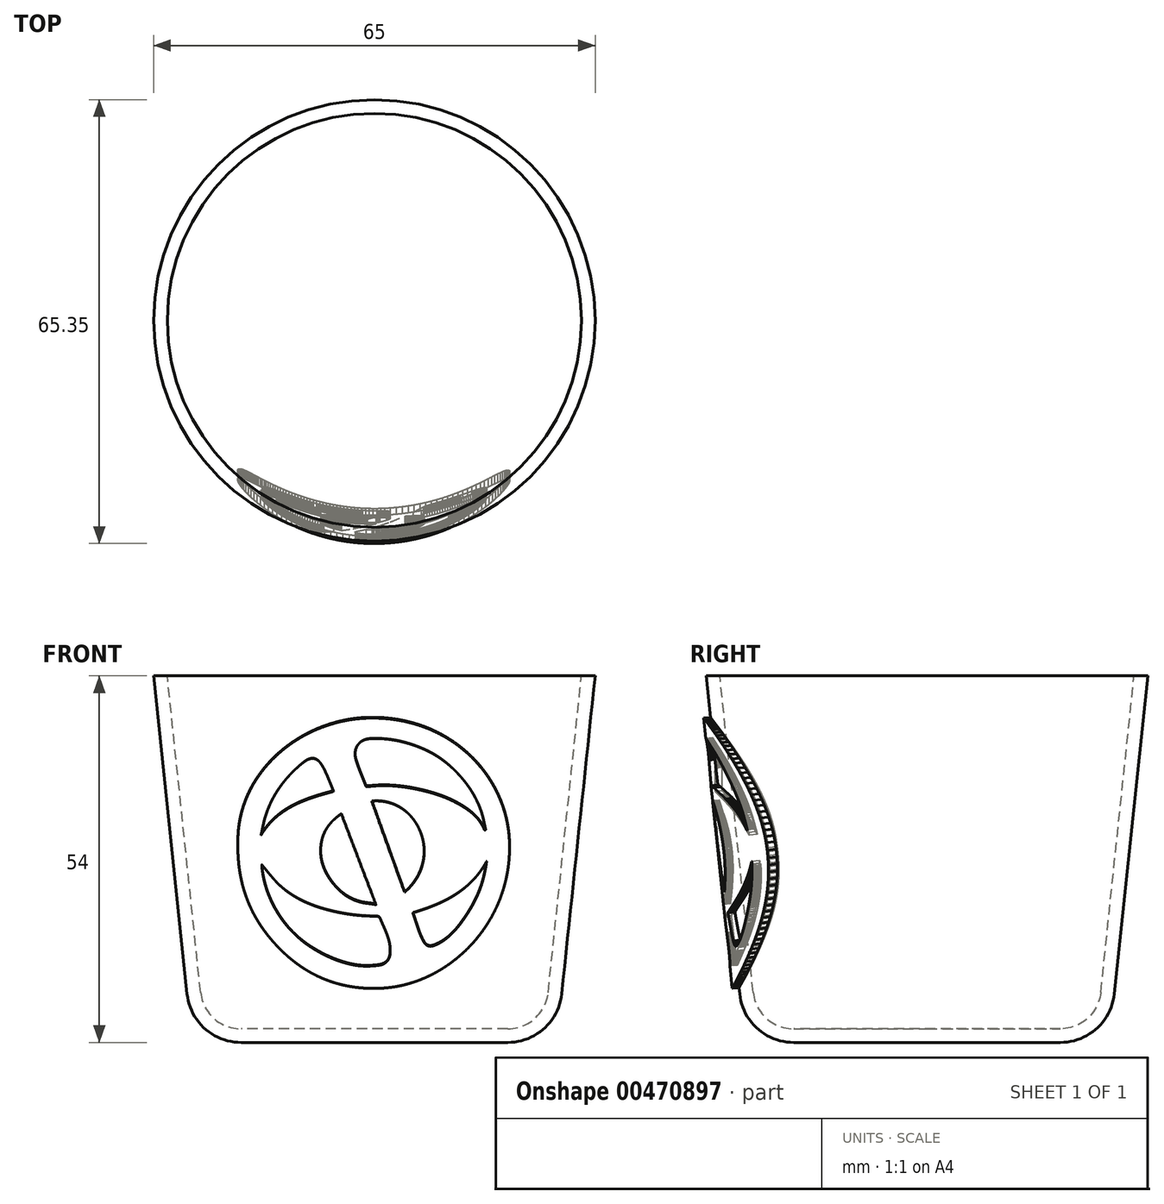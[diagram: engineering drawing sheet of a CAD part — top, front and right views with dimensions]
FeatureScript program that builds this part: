
annotation { "Feature Type Name" : "Feature", "Feature Type Description" : "" }
export const myFeature = defineFeature(function(context is Context, id is Id, definition is map)
    precondition{}
    {
        {
            var Q0;
            Q0=qCreatedBy(makeId("Front.planeOp"),FACE);
            var sketch = newSketch(context, id + "F0", { "sketchPlane" : qUnion([Q0])});
            skLineSegment(sketch, "E0", {"start": v(0, 0) * mm, "end": v(19.62, 0) * mm});
            skArc(sketch, "E1", {"start": v(19.62, 0) * mm, "mid": v(24.97, 2.05) * mm, "end": v(27.58, 7.16) * mm});
            skLineSegment(sketch, "E2", {"start": v(27.58, 7.16) * mm, "end": v(32.5, 54) * mm});
            skLineSegment(sketch, "E3.0", {"start": v(25.59, 7.37) * mm, "end": v(30.49, 54) * mm});
            skArc(sketch, "E3.1", {"start": v(19.62, 2) * mm, "mid": v(23.64, 3.54) * mm, "end": v(25.59, 7.37) * mm});
            skLineSegment(sketch, "E3.2", {"start": v(0, 2) * mm, "end": v(19.62, 2) * mm});
            skLineSegment(sketch, "E4", {"start": v(32.5, 54) * mm, "end": v(30.49, 54) * mm});
            skLineSegment(sketch, "E5", {"start": v(0, 2) * mm, "end": v(0, 0) * mm});
            skSolve(sketch);
        }
        {
            var Q0;
            Q0=makeQuery(id+"F0.imprint","IMPRINT",FACE,{"disambiguationData":[TD([[makeQuery(id+"F0.imprint","IMPRINT",EDGE,{"derivedFrom":sQuery(id+"F0.wireOp",EDGE,"E0")}),1.0]])]});
            var Q1;
            Q1=sQuery(id+"F0.wireOp",EDGE,"E5");
            revolve(context, id + "F1", {"entities" : qUnion([Q0]), "axis" : qUnion([Q1]), "revolveType" : RevolveType.FULL});
        }
        {
            var Q0;
            Q0=makeQuery(id+"F1.opRevolve","SWEPT_FACE",FACE,{"disambiguationData":[OSD([sQuery(id+"F0.wireOp",EDGE,"E4")])]});
            var sketch = newSketch(context, id + "F2", { "sketchPlane" : qUnion([Q0])});
            skCircle(sketch, "E6.0", {"center": v(0, 0) * mm, "radius": 30.49 * mm});
            skSolve(sketch);
        }
        {
            var Q0;
            Q0 = qSketchRegion(id + "F2", true);
            var Q1;
            Q1=makeQuery(id+"F1.opRevolve","SWEPT_FACE",FACE,{"disambiguationData":[OSD([sQuery(id+"F0.wireOp",EDGE,"E3.2")])]});
            extrude(context, id + "F3", {"entities" : qUnion([Q0]), "endBound" : BoundingType.UP_TO_SURFACE, "oppositeDirection" : true, "endBoundEntityFace" : qUnion([Q1]), "depth" : 10.6 * mm});
        }
        {
            var Q0;
            Q0=makeQuery(id+"F1.opRevolve","SWEPT_BODY",BODY,{"disambiguationData":[OSD([sQuery(id+"F0.wireOp",EDGE,"E0"),sQuery(id+"F0.wireOp",EDGE,"E1"),sQuery(id+"F0.wireOp",EDGE,"E2"),sQuery(id+"F0.wireOp",EDGE,"E3.0"),sQuery(id+"F0.wireOp",EDGE,"E3.1"),sQuery(id+"F0.wireOp",EDGE,"E3.2"),sQuery(id+"F0.wireOp",EDGE,"E4"),sQuery(id+"F0.wireOp",EDGE,"E5")])]});
            var Q1;
            Q1=makeQuery(id+"F3.opExtrude","SWEPT_BODY",BODY,{"disambiguationData":[OSD([sQuery(id+"F2.wireOp",EDGE,"E6.0")])]});
            booleanBodies(context, id + "F4", {"operationType" : BooleanOperationType.SUBTRACTION, "tools" : qUnion([Q0]), "targets" : qUnion([Q1]), "keepTools" : true});
        }
        {
            var Q0;
            Q0=makeQuery(id+"F4.opBoolean","SPLIT",BODY,{"disambiguationData":[OD(1.0)],"derivedFrom":makeQuery(id+"F3.opExtrude","SWEPT_BODY",BODY,{"disambiguationData":[OSD([sQuery(id+"F2.wireOp",EDGE,"E6.0")])]})});
            deleteBodies(context, id + "F5", {"entities" : qUnion([Q0])});
        }
        {
            var Q0;
            Q0=makeQuery(id+"F1.opRevolve","SWEPT_FACE",FACE,{"disambiguationData":[OSD([sQuery(id+"F0.wireOp",EDGE,"E4")])]});
            var sketch = newSketch(context, id + "F6", { "sketchPlane" : qUnion([Q0])});
            skPoint(sketch, "E7", {"position": v(0, -32.5) * mm});
            skLineSegment(sketch, "E8", {"start": v(36.98, -32.5) * mm, "end": v(-73.34, -32.5) * mm, "construction": true});
            skSolve(sketch);
        }
        {
            var Q0;
            Q0=qCreatedBy(makeId("Front.planeOp"),FACE);
            var Q1;
            Q1=sQuery(id+"F6.wireOp",VERTEX,"E7");
            cPlane(context, id + "F7", {"entities" : qUnion([Q0, Q1]), "cplaneType" : CPlaneType.PLANE_POINT, "offset" : 25 * mm, "width" : 150 * mm, "height" : 150 * mm});
        }
        {
            var Q0;
            Q0=qCreatedBy(id+"F7.planeOp",FACE);
            var Q1;
            Q1=sQuery(id+"F6.wireOp",EDGE,"E8");
            cPlane(context, id + "F8", {"entities" : qUnion([Q0, Q1]), "cplaneType" : CPlaneType.LINE_ANGLE, "offset" : 25 * mm, "angle" : 6 * degree, "oppositeDirection" : true, "width" : 150 * mm, "height" : 150 * mm});
        }
        {
            var Q0;
            Q0=qCreatedBy(id+"F8.planeOp",FACE);
            var sketch = newSketch(context, id + "F9", { "sketchPlane" : qUnion([Q0])});
            skLineSegment(sketch, "E9", {"start": v(20.1, 31.51) * mm, "end": v(20.1, 32.5) * mm});
            skLineSegment(sketch, "E10", {"start": v(20.1, 32.5) * mm, "end": v(20.03, 33.47) * mm});
            skLineSegment(sketch, "E11", {"start": v(20.03, 33.47) * mm, "end": v(19.91, 34.43) * mm});
            skLineSegment(sketch, "E12", {"start": v(19.91, 34.43) * mm, "end": v(19.75, 35.37) * mm});
            skLineSegment(sketch, "E13", {"start": v(19.75, 35.37) * mm, "end": v(19.53, 36.3) * mm});
            skLineSegment(sketch, "E14", {"start": v(19.53, 36.3) * mm, "end": v(19.27, 37.21) * mm});
            skLineSegment(sketch, "E15", {"start": v(19.27, 37.21) * mm, "end": v(18.96, 38.1) * mm});
            skLineSegment(sketch, "E16", {"start": v(18.96, 38.1) * mm, "end": v(18.6, 38.97) * mm});
            skLineSegment(sketch, "E17", {"start": v(18.6, 38.97) * mm, "end": v(18.21, 39.82) * mm});
            skLineSegment(sketch, "E18", {"start": v(18.21, 39.82) * mm, "end": v(17.78, 40.65) * mm});
            skLineSegment(sketch, "E19", {"start": v(17.78, 40.65) * mm, "end": v(17.3, 41.45) * mm});
            skLineSegment(sketch, "E20", {"start": v(17.3, 41.45) * mm, "end": v(16.79, 42.23) * mm});
            skLineSegment(sketch, "E21", {"start": v(16.79, 42.23) * mm, "end": v(16.23, 42.98) * mm});
            skLineSegment(sketch, "E22", {"start": v(16.23, 42.98) * mm, "end": v(15.65, 43.71) * mm});
            skLineSegment(sketch, "E23", {"start": v(15.65, 43.71) * mm, "end": v(15.03, 44.41) * mm});
            skLineSegment(sketch, "E24", {"start": v(15.03, 44.41) * mm, "end": v(14.38, 45.08) * mm});
            skLineSegment(sketch, "E25", {"start": v(14.38, 45.08) * mm, "end": v(13.7, 45.72) * mm});
            skLineSegment(sketch, "E26", {"start": v(13.7, 45.72) * mm, "end": v(12.99, 46.33) * mm});
            skLineSegment(sketch, "E27", {"start": v(12.99, 46.33) * mm, "end": v(12.25, 46.9) * mm});
            skLineSegment(sketch, "E28", {"start": v(12.25, 46.9) * mm, "end": v(11.49, 47.45) * mm});
            skLineSegment(sketch, "E29", {"start": v(11.49, 47.45) * mm, "end": v(10.7, 47.96) * mm});
            skLineSegment(sketch, "E30", {"start": v(10.7, 47.96) * mm, "end": v(9.9, 48.43) * mm});
            skLineSegment(sketch, "E31", {"start": v(9.9, 48.43) * mm, "end": v(9.07, 48.87) * mm});
            skLineSegment(sketch, "E32", {"start": v(9.07, 48.87) * mm, "end": v(8.22, 49.26) * mm});
            skLineSegment(sketch, "E33", {"start": v(8.22, 49.26) * mm, "end": v(7.35, 49.62) * mm});
            skLineSegment(sketch, "E34", {"start": v(7.35, 49.62) * mm, "end": v(6.47, 49.94) * mm});
            skLineSegment(sketch, "E35", {"start": v(6.47, 49.94) * mm, "end": v(5.58, 50.22) * mm});
            skLineSegment(sketch, "E36", {"start": v(5.58, 50.22) * mm, "end": v(4.67, 50.45) * mm});
            skLineSegment(sketch, "E37", {"start": v(4.67, 50.45) * mm, "end": v(3.75, 50.64) * mm});
            skLineSegment(sketch, "E38", {"start": v(3.75, 50.64) * mm, "end": v(2.82, 50.8) * mm});
            skLineSegment(sketch, "E39", {"start": v(2.82, 50.8) * mm, "end": v(1.88, 50.9) * mm});
            skLineSegment(sketch, "E40", {"start": v(1.88, 50.9) * mm, "end": v(0.94, 50.94) * mm});
            skLineSegment(sketch, "E41", {"start": v(0.94, 50.94) * mm, "end": v(-0.18, 50.95) * mm});
            skLineSegment(sketch, "E42", {"start": v(-0.18, 50.95) * mm, "end": v(-1.27, 50.9) * mm});
            skLineSegment(sketch, "E43", {"start": v(-1.27, 50.9) * mm, "end": v(-2.35, 50.8) * mm});
            skLineSegment(sketch, "E44", {"start": v(-2.35, 50.8) * mm, "end": v(-3.4, 50.64) * mm});
            skLineSegment(sketch, "E45", {"start": v(-3.4, 50.64) * mm, "end": v(-4.42, 50.43) * mm});
            skLineSegment(sketch, "E46", {"start": v(-4.42, 50.43) * mm, "end": v(-5.42, 50.17) * mm});
            skLineSegment(sketch, "E47", {"start": v(-5.42, 50.17) * mm, "end": v(-6.4, 49.86) * mm});
            skLineSegment(sketch, "E48", {"start": v(-6.4, 49.86) * mm, "end": v(-7.34, 49.51) * mm});
            skLineSegment(sketch, "E49", {"start": v(-7.34, 49.51) * mm, "end": v(-8.26, 49.12) * mm});
            skLineSegment(sketch, "E50", {"start": v(-8.26, 49.12) * mm, "end": v(-9.16, 48.68) * mm});
            skLineSegment(sketch, "E51", {"start": v(-9.16, 48.68) * mm, "end": v(-10.02, 48.2) * mm});
            skLineSegment(sketch, "E52", {"start": v(-10.02, 48.2) * mm, "end": v(-10.85, 47.68) * mm});
            skLineSegment(sketch, "E53", {"start": v(-10.85, 47.68) * mm, "end": v(-11.65, 47.12) * mm});
            skLineSegment(sketch, "E54", {"start": v(-11.65, 47.12) * mm, "end": v(-12.42, 46.53) * mm});
            skLineSegment(sketch, "E55", {"start": v(-12.42, 46.53) * mm, "end": v(-13.16, 45.9) * mm});
            skLineSegment(sketch, "E56", {"start": v(-13.16, 45.9) * mm, "end": v(-13.86, 45.24) * mm});
            skLineSegment(sketch, "E57", {"start": v(-13.86, 45.24) * mm, "end": v(-14.53, 44.56) * mm});
            skLineSegment(sketch, "E58", {"start": v(-14.53, 44.56) * mm, "end": v(-15.17, 43.84) * mm});
            skLineSegment(sketch, "E59", {"start": v(-15.17, 43.84) * mm, "end": v(-15.77, 43.1) * mm});
            skLineSegment(sketch, "E60", {"start": v(-15.77, 43.1) * mm, "end": v(-16.33, 42.32) * mm});
            skLineSegment(sketch, "E61", {"start": v(-16.33, 42.32) * mm, "end": v(-16.85, 41.53) * mm});
            skLineSegment(sketch, "E62", {"start": v(-16.85, 41.53) * mm, "end": v(-17.34, 40.72) * mm});
            skLineSegment(sketch, "E63", {"start": v(-17.34, 40.72) * mm, "end": v(-17.78, 39.88) * mm});
            skLineSegment(sketch, "E64", {"start": v(-17.78, 39.88) * mm, "end": v(-18.19, 39.03) * mm});
            skLineSegment(sketch, "E65", {"start": v(-18.19, 39.03) * mm, "end": v(-18.55, 38.16) * mm});
            skLineSegment(sketch, "E66", {"start": v(-18.55, 38.16) * mm, "end": v(-18.88, 37.27) * mm});
            skLineSegment(sketch, "E67", {"start": v(-18.88, 37.27) * mm, "end": v(-19.16, 36.37) * mm});
            skLineSegment(sketch, "E68", {"start": v(-19.16, 36.37) * mm, "end": v(-19.4, 35.47) * mm});
            skLineSegment(sketch, "E69", {"start": v(-19.4, 35.47) * mm, "end": v(-19.59, 34.55) * mm});
            skLineSegment(sketch, "E70", {"start": v(-19.59, 34.55) * mm, "end": v(-19.73, 33.62) * mm});
            skLineSegment(sketch, "E71", {"start": v(-19.73, 33.62) * mm, "end": v(-19.84, 32.69) * mm});
            skLineSegment(sketch, "E72", {"start": v(-19.84, 32.69) * mm, "end": v(-19.89, 31.75) * mm});
            skLineSegment(sketch, "E73", {"start": v(-19.89, 31.75) * mm, "end": v(-19.9, 30.63) * mm});
            skLineSegment(sketch, "E74", {"start": v(-19.9, 30.63) * mm, "end": v(-19.85, 29.53) * mm});
            skLineSegment(sketch, "E75", {"start": v(-19.85, 29.53) * mm, "end": v(-19.75, 28.46) * mm});
            skLineSegment(sketch, "E76", {"start": v(-19.75, 28.46) * mm, "end": v(-19.6, 27.4) * mm});
            skLineSegment(sketch, "E77", {"start": v(-19.6, 27.4) * mm, "end": v(-19.39, 26.39) * mm});
            skLineSegment(sketch, "E78", {"start": v(-19.39, 26.39) * mm, "end": v(-19.13, 25.4) * mm});
            skLineSegment(sketch, "E79", {"start": v(-19.13, 25.4) * mm, "end": v(-18.83, 24.42) * mm});
            skLineSegment(sketch, "E80", {"start": v(-18.83, 24.42) * mm, "end": v(-18.49, 23.49) * mm});
            skLineSegment(sketch, "E81", {"start": v(-18.49, 23.49) * mm, "end": v(-18.1, 22.57) * mm});
            skLineSegment(sketch, "E82", {"start": v(-18.1, 22.57) * mm, "end": v(-17.67, 21.7) * mm});
            skLineSegment(sketch, "E83", {"start": v(-17.67, 21.7) * mm, "end": v(-17.2, 20.84) * mm});
            skLineSegment(sketch, "E84", {"start": v(-17.2, 20.84) * mm, "end": v(-16.7, 20.02) * mm});
            skLineSegment(sketch, "E85", {"start": v(-16.7, 20.02) * mm, "end": v(-16.15, 19.23) * mm});
            skLineSegment(sketch, "E86", {"start": v(-16.15, 19.23) * mm, "end": v(-15.58, 18.47) * mm});
            skLineSegment(sketch, "E87", {"start": v(-15.58, 18.47) * mm, "end": v(-14.97, 17.74) * mm});
            skLineSegment(sketch, "E88", {"start": v(-14.97, 17.74) * mm, "end": v(-14.33, 17.05) * mm});
            skLineSegment(sketch, "E89", {"start": v(-14.33, 17.05) * mm, "end": v(-13.66, 16.4) * mm});
            skLineSegment(sketch, "E90", {"start": v(-13.66, 16.4) * mm, "end": v(-12.97, 15.77) * mm});
            skLineSegment(sketch, "E91", {"start": v(-12.97, 15.77) * mm, "end": v(-12.25, 15.18) * mm});
            skLineSegment(sketch, "E92", {"start": v(-12.25, 15.18) * mm, "end": v(-11.5, 14.62) * mm});
            skLineSegment(sketch, "E93", {"start": v(-11.5, 14.62) * mm, "end": v(-10.74, 14.1) * mm});
            skLineSegment(sketch, "E94", {"start": v(-10.74, 14.1) * mm, "end": v(-9.96, 13.62) * mm});
            skLineSegment(sketch, "E95", {"start": v(-9.96, 13.62) * mm, "end": v(-9.16, 13.18) * mm});
            skLineSegment(sketch, "E96", {"start": v(-9.16, 13.18) * mm, "end": v(-8.34, 12.77) * mm});
            skLineSegment(sketch, "E97", {"start": v(-8.34, 12.77) * mm, "end": v(-7.51, 12.4) * mm});
            skLineSegment(sketch, "E98", {"start": v(-7.51, 12.4) * mm, "end": v(-6.67, 12.07) * mm});
            skLineSegment(sketch, "E99", {"start": v(-6.67, 12.07) * mm, "end": v(-5.82, 11.78) * mm});
            skLineSegment(sketch, "E100", {"start": v(-5.82, 11.78) * mm, "end": v(-4.96, 11.53) * mm});
            skLineSegment(sketch, "E101", {"start": v(-4.96, 11.53) * mm, "end": v(-4.09, 11.33) * mm});
            skLineSegment(sketch, "E102", {"start": v(-4.09, 11.33) * mm, "end": v(-3.22, 11.16) * mm});
            skLineSegment(sketch, "E103", {"start": v(-3.22, 11.16) * mm, "end": v(-2.34, 11.04) * mm});
            skLineSegment(sketch, "E104", {"start": v(-2.34, 11.04) * mm, "end": v(-1.46, 10.96) * mm});
            skLineSegment(sketch, "E105", {"start": v(-1.46, 10.96) * mm, "end": v(-0.9, 10.93) * mm});
            skLineSegment(sketch, "E106", {"start": v(-0.9, 10.93) * mm, "end": v(-0.33, 10.91) * mm});
            skLineSegment(sketch, "E107", {"start": v(-0.33, 10.91) * mm, "end": v(0.23, 10.9) * mm});
            skLineSegment(sketch, "E108", {"start": v(0.23, 10.9) * mm, "end": v(0.79, 10.92) * mm});
            skLineSegment(sketch, "E109", {"start": v(0.79, 10.92) * mm, "end": v(1.34, 10.94) * mm});
            skLineSegment(sketch, "E110", {"start": v(1.34, 10.94) * mm, "end": v(1.89, 10.97) * mm});
            skLineSegment(sketch, "E111", {"start": v(1.89, 10.97) * mm, "end": v(2.43, 11.02) * mm});
            skLineSegment(sketch, "E112", {"start": v(2.43, 11.02) * mm, "end": v(2.97, 11.09) * mm});
            skLineSegment(sketch, "E113", {"start": v(2.97, 11.09) * mm, "end": v(3.5, 11.16) * mm});
            skLineSegment(sketch, "E114", {"start": v(3.5, 11.16) * mm, "end": v(4.03, 11.25) * mm});
            skLineSegment(sketch, "E115", {"start": v(4.03, 11.25) * mm, "end": v(4.55, 11.36) * mm});
            skLineSegment(sketch, "E116", {"start": v(4.55, 11.36) * mm, "end": v(5.07, 11.47) * mm});
            skLineSegment(sketch, "E117", {"start": v(5.07, 11.47) * mm, "end": v(5.58, 11.6) * mm});
            skLineSegment(sketch, "E118", {"start": v(5.58, 11.6) * mm, "end": v(6.09, 11.75) * mm});
            skLineSegment(sketch, "E119", {"start": v(6.09, 11.75) * mm, "end": v(6.59, 11.9) * mm});
            skLineSegment(sketch, "E120", {"start": v(6.59, 11.9) * mm, "end": v(7.08, 12.08) * mm});
            skLineSegment(sketch, "E121", {"start": v(7.08, 12.08) * mm, "end": v(7.58, 12.27) * mm});
            skLineSegment(sketch, "E122", {"start": v(7.58, 12.27) * mm, "end": v(8.06, 12.47) * mm});
            skLineSegment(sketch, "E123", {"start": v(8.06, 12.47) * mm, "end": v(8.54, 12.68) * mm});
            skLineSegment(sketch, "E124", {"start": v(8.54, 12.68) * mm, "end": v(9.02, 12.9) * mm});
            skLineSegment(sketch, "E125", {"start": v(9.02, 12.9) * mm, "end": v(9.49, 13.15) * mm});
            skLineSegment(sketch, "E126", {"start": v(9.49, 13.15) * mm, "end": v(9.95, 13.4) * mm});
            skLineSegment(sketch, "E127", {"start": v(9.95, 13.4) * mm, "end": v(10.41, 13.68) * mm});
            skLineSegment(sketch, "E128", {"start": v(10.41, 13.68) * mm, "end": v(10.87, 13.96) * mm});
            skLineSegment(sketch, "E129", {"start": v(10.87, 13.96) * mm, "end": v(11.31, 14.26) * mm});
            skLineSegment(sketch, "E130", {"start": v(11.31, 14.26) * mm, "end": v(11.76, 14.57) * mm});
            skLineSegment(sketch, "E131", {"start": v(11.76, 14.57) * mm, "end": v(12.2, 14.9) * mm});
            skLineSegment(sketch, "E132", {"start": v(12.2, 14.9) * mm, "end": v(12.62, 15.24) * mm});
            skLineSegment(sketch, "E133", {"start": v(12.62, 15.24) * mm, "end": v(13.05, 15.6) * mm});
            skLineSegment(sketch, "E134", {"start": v(13.05, 15.6) * mm, "end": v(13.47, 15.96) * mm});
            skLineSegment(sketch, "E135", {"start": v(13.47, 15.96) * mm, "end": v(13.88, 16.34) * mm});
            skLineSegment(sketch, "E136", {"start": v(13.88, 16.34) * mm, "end": v(14.29, 16.74) * mm});
            skLineSegment(sketch, "E137", {"start": v(14.29, 16.74) * mm, "end": v(14.64, 17.1) * mm});
            skLineSegment(sketch, "E138", {"start": v(14.64, 17.1) * mm, "end": v(14.99, 17.47) * mm});
            skLineSegment(sketch, "E139", {"start": v(14.99, 17.47) * mm, "end": v(15.32, 17.85) * mm});
            skLineSegment(sketch, "E140", {"start": v(15.32, 17.85) * mm, "end": v(15.65, 18.23) * mm});
            skLineSegment(sketch, "E141", {"start": v(15.65, 18.23) * mm, "end": v(15.96, 18.61) * mm});
            skLineSegment(sketch, "E142", {"start": v(15.96, 18.61) * mm, "end": v(16.26, 19) * mm});
            skLineSegment(sketch, "E143", {"start": v(16.26, 19) * mm, "end": v(16.55, 19.4) * mm});
            skLineSegment(sketch, "E144", {"start": v(16.55, 19.4) * mm, "end": v(16.83, 19.8) * mm});
            skLineSegment(sketch, "E145", {"start": v(16.83, 19.8) * mm, "end": v(17.1, 20.22) * mm});
            skLineSegment(sketch, "E146", {"start": v(17.1, 20.22) * mm, "end": v(17.36, 20.63) * mm});
            skLineSegment(sketch, "E147", {"start": v(17.36, 20.63) * mm, "end": v(17.6, 21.05) * mm});
            skLineSegment(sketch, "E148", {"start": v(17.6, 21.05) * mm, "end": v(17.84, 21.48) * mm});
            skLineSegment(sketch, "E149", {"start": v(17.84, 21.48) * mm, "end": v(18.07, 21.91) * mm});
            skLineSegment(sketch, "E150", {"start": v(18.07, 21.91) * mm, "end": v(18.28, 22.35) * mm});
            skLineSegment(sketch, "E151", {"start": v(18.28, 22.35) * mm, "end": v(18.48, 22.8) * mm});
            skLineSegment(sketch, "E152", {"start": v(18.48, 22.8) * mm, "end": v(18.67, 23.26) * mm});
            skLineSegment(sketch, "E153", {"start": v(18.67, 23.26) * mm, "end": v(18.85, 23.72) * mm});
            skLineSegment(sketch, "E154", {"start": v(18.85, 23.72) * mm, "end": v(19.02, 24.18) * mm});
            skLineSegment(sketch, "E155", {"start": v(19.02, 24.18) * mm, "end": v(19.17, 24.66) * mm});
            skLineSegment(sketch, "E156", {"start": v(19.17, 24.66) * mm, "end": v(19.32, 25.14) * mm});
            skLineSegment(sketch, "E157", {"start": v(19.32, 25.14) * mm, "end": v(19.45, 25.63) * mm});
            skLineSegment(sketch, "E158", {"start": v(19.45, 25.63) * mm, "end": v(19.57, 26.12) * mm});
            skLineSegment(sketch, "E159", {"start": v(19.57, 26.12) * mm, "end": v(19.68, 26.63) * mm});
            skLineSegment(sketch, "E160", {"start": v(19.68, 26.63) * mm, "end": v(19.77, 27.14) * mm});
            skLineSegment(sketch, "E161", {"start": v(19.77, 27.14) * mm, "end": v(19.86, 27.66) * mm});
            skLineSegment(sketch, "E162", {"start": v(19.86, 27.66) * mm, "end": v(19.93, 28.18) * mm});
            skLineSegment(sketch, "E163", {"start": v(19.93, 28.18) * mm, "end": v(19.99, 28.72) * mm});
            skLineSegment(sketch, "E164", {"start": v(19.99, 28.72) * mm, "end": v(20.04, 29.26) * mm});
            skLineSegment(sketch, "E165", {"start": v(20.04, 29.26) * mm, "end": v(20.07, 29.81) * mm});
            skLineSegment(sketch, "E166", {"start": v(20.07, 29.81) * mm, "end": v(20.1, 30.37) * mm});
            skLineSegment(sketch, "E167", {"start": v(20.1, 30.37) * mm, "end": v(20.1, 30.94) * mm});
            skLineSegment(sketch, "E168", {"start": v(20.1, 30.94) * mm, "end": v(20.1, 31.51) * mm});
            skLineSegment(sketch, "E169", {"start": v(18.1, 31.51) * mm, "end": v(18.1, 30.94) * mm});
            skLineSegment(sketch, "E170", {"start": v(20.1, 30.94) * mm, "end": v(20.1, 30.37) * mm});
            skLineSegment(sketch, "E171", {"start": v(20.1, 30.37) * mm, "end": v(20.07, 29.81) * mm});
            skLineSegment(sketch, "E172", {"start": v(20.07, 29.81) * mm, "end": v(20.04, 29.26) * mm});
            skLineSegment(sketch, "E173", {"start": v(20.04, 29.26) * mm, "end": v(19.99, 28.72) * mm});
            skLineSegment(sketch, "E174", {"start": v(19.99, 28.72) * mm, "end": v(19.93, 28.18) * mm});
            skLineSegment(sketch, "E175", {"start": v(19.93, 28.18) * mm, "end": v(19.86, 27.66) * mm});
            skLineSegment(sketch, "E176", {"start": v(19.86, 27.66) * mm, "end": v(19.77, 27.14) * mm});
            skLineSegment(sketch, "E177", {"start": v(19.77, 27.14) * mm, "end": v(19.68, 26.63) * mm});
            skLineSegment(sketch, "E178", {"start": v(19.68, 26.63) * mm, "end": v(19.57, 26.12) * mm});
            skLineSegment(sketch, "E179", {"start": v(19.57, 26.12) * mm, "end": v(19.45, 25.63) * mm});
            skLineSegment(sketch, "E180", {"start": v(19.45, 25.63) * mm, "end": v(19.32, 25.14) * mm});
            skLineSegment(sketch, "E181", {"start": v(19.32, 25.14) * mm, "end": v(19.17, 24.66) * mm});
            skLineSegment(sketch, "E182", {"start": v(19.17, 24.66) * mm, "end": v(19.02, 24.18) * mm});
            skLineSegment(sketch, "E183", {"start": v(19.02, 24.18) * mm, "end": v(18.85, 23.72) * mm});
            skLineSegment(sketch, "E184", {"start": v(18.85, 23.72) * mm, "end": v(18.67, 23.26) * mm});
            skLineSegment(sketch, "E185", {"start": v(18.67, 23.26) * mm, "end": v(18.48, 22.8) * mm});
            skLineSegment(sketch, "E186", {"start": v(18.48, 22.8) * mm, "end": v(18.28, 22.35) * mm});
            skLineSegment(sketch, "E187", {"start": v(18.28, 22.35) * mm, "end": v(18.07, 21.91) * mm});
            skLineSegment(sketch, "E188", {"start": v(18.07, 21.91) * mm, "end": v(17.84, 21.48) * mm});
            skLineSegment(sketch, "E189", {"start": v(17.84, 21.48) * mm, "end": v(17.6, 21.05) * mm});
            skLineSegment(sketch, "E190", {"start": v(17.6, 21.05) * mm, "end": v(17.36, 20.63) * mm});
            skLineSegment(sketch, "E191", {"start": v(17.36, 20.63) * mm, "end": v(17.1, 20.22) * mm});
            skLineSegment(sketch, "E192", {"start": v(17.1, 20.22) * mm, "end": v(16.83, 19.8) * mm});
            skLineSegment(sketch, "E193", {"start": v(16.83, 19.8) * mm, "end": v(16.55, 19.4) * mm});
            skLineSegment(sketch, "E194", {"start": v(16.55, 19.4) * mm, "end": v(16.26, 19) * mm});
            skLineSegment(sketch, "E195", {"start": v(16.26, 19) * mm, "end": v(15.96, 18.61) * mm});
            skLineSegment(sketch, "E196", {"start": v(15.96, 18.61) * mm, "end": v(15.65, 18.23) * mm});
            skLineSegment(sketch, "E197", {"start": v(15.65, 18.23) * mm, "end": v(15.32, 17.85) * mm});
            skLineSegment(sketch, "E198", {"start": v(15.32, 17.85) * mm, "end": v(14.99, 17.47) * mm});
            skLineSegment(sketch, "E199", {"start": v(14.99, 17.47) * mm, "end": v(14.64, 17.1) * mm});
            skLineSegment(sketch, "E200", {"start": v(14.64, 17.1) * mm, "end": v(14.29, 16.74) * mm});
            skLineSegment(sketch, "E201", {"start": v(14.29, 16.74) * mm, "end": v(13.88, 16.34) * mm});
            skLineSegment(sketch, "E202", {"start": v(13.88, 16.34) * mm, "end": v(13.47, 15.96) * mm});
            skLineSegment(sketch, "E203", {"start": v(13.47, 15.96) * mm, "end": v(13.05, 15.6) * mm});
            skLineSegment(sketch, "E204", {"start": v(13.05, 15.6) * mm, "end": v(12.62, 15.24) * mm});
            skLineSegment(sketch, "E205", {"start": v(12.62, 15.24) * mm, "end": v(12.2, 14.9) * mm});
            skLineSegment(sketch, "E206", {"start": v(12.2, 14.9) * mm, "end": v(11.76, 14.57) * mm});
            skLineSegment(sketch, "E207", {"start": v(11.76, 14.57) * mm, "end": v(11.31, 14.26) * mm});
            skLineSegment(sketch, "E208", {"start": v(11.31, 14.26) * mm, "end": v(10.87, 13.96) * mm});
            skLineSegment(sketch, "E209", {"start": v(10.87, 13.96) * mm, "end": v(10.41, 13.68) * mm});
            skLineSegment(sketch, "E210", {"start": v(10.41, 13.68) * mm, "end": v(9.95, 13.4) * mm});
            skLineSegment(sketch, "E211", {"start": v(9.95, 13.4) * mm, "end": v(9.49, 13.15) * mm});
            skLineSegment(sketch, "E212", {"start": v(9.49, 13.15) * mm, "end": v(9.02, 12.9) * mm});
            skLineSegment(sketch, "E213", {"start": v(9.02, 12.9) * mm, "end": v(8.54, 12.68) * mm});
            skLineSegment(sketch, "E214", {"start": v(8.54, 12.68) * mm, "end": v(8.06, 12.47) * mm});
            skLineSegment(sketch, "E215", {"start": v(8.06, 12.47) * mm, "end": v(7.58, 12.27) * mm});
            skLineSegment(sketch, "E216", {"start": v(7.58, 12.27) * mm, "end": v(7.08, 12.08) * mm});
            skLineSegment(sketch, "E217", {"start": v(7.08, 12.08) * mm, "end": v(6.59, 11.9) * mm});
            skLineSegment(sketch, "E218", {"start": v(6.59, 11.9) * mm, "end": v(6.09, 11.75) * mm});
            skLineSegment(sketch, "E219", {"start": v(6.09, 11.75) * mm, "end": v(5.58, 11.6) * mm});
            skLineSegment(sketch, "E220", {"start": v(5.58, 11.6) * mm, "end": v(5.07, 11.47) * mm});
            skLineSegment(sketch, "E221", {"start": v(5.07, 11.47) * mm, "end": v(4.55, 11.36) * mm});
            skLineSegment(sketch, "E222", {"start": v(4.55, 11.36) * mm, "end": v(4.03, 11.25) * mm});
            skLineSegment(sketch, "E223", {"start": v(4.03, 11.25) * mm, "end": v(3.5, 11.16) * mm});
            skLineSegment(sketch, "E224", {"start": v(3.5, 11.16) * mm, "end": v(2.97, 11.09) * mm});
            skLineSegment(sketch, "E225", {"start": v(2.97, 11.09) * mm, "end": v(2.43, 11.02) * mm});
            skLineSegment(sketch, "E226", {"start": v(2.43, 11.02) * mm, "end": v(1.89, 10.97) * mm});
            skLineSegment(sketch, "E227", {"start": v(1.89, 10.97) * mm, "end": v(1.34, 10.94) * mm});
            skLineSegment(sketch, "E228", {"start": v(1.34, 10.94) * mm, "end": v(0.79, 10.92) * mm});
            skLineSegment(sketch, "E229", {"start": v(0.79, 10.92) * mm, "end": v(0.23, 10.9) * mm});
            skLineSegment(sketch, "E230", {"start": v(0.23, 10.9) * mm, "end": v(-0.33, 10.91) * mm});
            skLineSegment(sketch, "E231", {"start": v(-0.33, 10.91) * mm, "end": v(-0.9, 10.93) * mm});
            skLineSegment(sketch, "E232", {"start": v(-0.9, 10.93) * mm, "end": v(-1.46, 10.96) * mm});
            skLineSegment(sketch, "E233", {"start": v(-1.46, 10.96) * mm, "end": v(-2.34, 11.04) * mm});
            skLineSegment(sketch, "E234", {"start": v(-2.34, 11.04) * mm, "end": v(-3.22, 11.16) * mm});
            skLineSegment(sketch, "E235", {"start": v(-3.22, 11.16) * mm, "end": v(-4.09, 11.33) * mm});
            skLineSegment(sketch, "E236", {"start": v(-4.09, 11.33) * mm, "end": v(-4.96, 11.53) * mm});
            skLineSegment(sketch, "E237", {"start": v(-4.96, 11.53) * mm, "end": v(-5.82, 11.78) * mm});
            skLineSegment(sketch, "E238", {"start": v(-5.82, 11.78) * mm, "end": v(-6.67, 12.07) * mm});
            skLineSegment(sketch, "E239", {"start": v(-6.67, 12.07) * mm, "end": v(-7.51, 12.4) * mm});
            skLineSegment(sketch, "E240", {"start": v(-7.51, 12.4) * mm, "end": v(-8.34, 12.77) * mm});
            skLineSegment(sketch, "E241", {"start": v(-8.34, 12.77) * mm, "end": v(-9.16, 13.18) * mm});
            skLineSegment(sketch, "E242", {"start": v(-9.16, 13.18) * mm, "end": v(-9.96, 13.62) * mm});
            skLineSegment(sketch, "E243", {"start": v(-9.96, 13.62) * mm, "end": v(-10.74, 14.1) * mm});
            skLineSegment(sketch, "E244", {"start": v(-10.74, 14.1) * mm, "end": v(-11.5, 14.62) * mm});
            skLineSegment(sketch, "E245", {"start": v(-11.5, 14.62) * mm, "end": v(-12.25, 15.18) * mm});
            skLineSegment(sketch, "E246", {"start": v(-12.25, 15.18) * mm, "end": v(-12.97, 15.77) * mm});
            skLineSegment(sketch, "E247", {"start": v(-12.97, 15.77) * mm, "end": v(-13.66, 16.4) * mm});
            skLineSegment(sketch, "E248", {"start": v(-13.66, 16.4) * mm, "end": v(-14.33, 17.05) * mm});
            skLineSegment(sketch, "E249", {"start": v(-14.33, 17.05) * mm, "end": v(-14.97, 17.74) * mm});
            skLineSegment(sketch, "E250", {"start": v(-14.97, 17.74) * mm, "end": v(-15.58, 18.47) * mm});
            skLineSegment(sketch, "E251", {"start": v(-15.58, 18.47) * mm, "end": v(-16.15, 19.23) * mm});
            skLineSegment(sketch, "E252", {"start": v(-16.15, 19.23) * mm, "end": v(-16.7, 20.02) * mm});
            skLineSegment(sketch, "E253", {"start": v(-16.7, 20.02) * mm, "end": v(-17.2, 20.84) * mm});
            skLineSegment(sketch, "E254", {"start": v(-17.2, 20.84) * mm, "end": v(-17.67, 21.7) * mm});
            skLineSegment(sketch, "E255", {"start": v(-17.67, 21.7) * mm, "end": v(-18.1, 22.57) * mm});
            skLineSegment(sketch, "E256", {"start": v(-18.1, 22.57) * mm, "end": v(-18.49, 23.49) * mm});
            skLineSegment(sketch, "E257", {"start": v(-18.49, 23.49) * mm, "end": v(-18.83, 24.42) * mm});
            skLineSegment(sketch, "E258", {"start": v(-18.83, 24.42) * mm, "end": v(-19.13, 25.4) * mm});
            skLineSegment(sketch, "E259", {"start": v(-19.13, 25.4) * mm, "end": v(-19.39, 26.39) * mm});
            skLineSegment(sketch, "E260", {"start": v(-19.39, 26.39) * mm, "end": v(-19.6, 27.4) * mm});
            skLineSegment(sketch, "E261", {"start": v(-19.6, 27.4) * mm, "end": v(-19.75, 28.46) * mm});
            skLineSegment(sketch, "E262", {"start": v(-19.75, 28.46) * mm, "end": v(-19.85, 29.53) * mm});
            skLineSegment(sketch, "E263", {"start": v(-19.85, 29.53) * mm, "end": v(-19.9, 30.63) * mm});
            skLineSegment(sketch, "E264", {"start": v(-19.9, 30.63) * mm, "end": v(-19.89, 31.75) * mm});
            skLineSegment(sketch, "E265", {"start": v(-19.89, 31.75) * mm, "end": v(-19.84, 32.69) * mm});
            skLineSegment(sketch, "E266", {"start": v(-19.84, 32.69) * mm, "end": v(-19.73, 33.62) * mm});
            skLineSegment(sketch, "E267", {"start": v(-19.73, 33.62) * mm, "end": v(-19.59, 34.55) * mm});
            skLineSegment(sketch, "E268", {"start": v(-19.59, 34.55) * mm, "end": v(-19.4, 35.47) * mm});
            skLineSegment(sketch, "E269", {"start": v(-19.4, 35.47) * mm, "end": v(-19.16, 36.37) * mm});
            skLineSegment(sketch, "E270", {"start": v(-19.16, 36.37) * mm, "end": v(-18.88, 37.27) * mm});
            skLineSegment(sketch, "E271", {"start": v(-18.88, 37.27) * mm, "end": v(-18.55, 38.16) * mm});
            skLineSegment(sketch, "E272", {"start": v(-18.55, 38.16) * mm, "end": v(-18.19, 39.03) * mm});
            skLineSegment(sketch, "E273", {"start": v(-18.19, 39.03) * mm, "end": v(-17.78, 39.88) * mm});
            skLineSegment(sketch, "E274", {"start": v(-17.78, 39.88) * mm, "end": v(-17.34, 40.72) * mm});
            skLineSegment(sketch, "E275", {"start": v(-17.34, 40.72) * mm, "end": v(-16.85, 41.53) * mm});
            skLineSegment(sketch, "E276", {"start": v(-16.85, 41.53) * mm, "end": v(-16.33, 42.32) * mm});
            skLineSegment(sketch, "E277", {"start": v(-16.33, 42.32) * mm, "end": v(-15.77, 43.1) * mm});
            skLineSegment(sketch, "E278", {"start": v(-15.77, 43.1) * mm, "end": v(-15.17, 43.84) * mm});
            skLineSegment(sketch, "E279", {"start": v(-15.17, 43.84) * mm, "end": v(-14.53, 44.56) * mm});
            skLineSegment(sketch, "E280", {"start": v(-14.53, 44.56) * mm, "end": v(-13.86, 45.24) * mm});
            skLineSegment(sketch, "E281", {"start": v(-13.86, 45.24) * mm, "end": v(-13.16, 45.9) * mm});
            skLineSegment(sketch, "E282", {"start": v(-13.16, 45.9) * mm, "end": v(-12.42, 46.53) * mm});
            skLineSegment(sketch, "E283", {"start": v(-12.42, 46.53) * mm, "end": v(-11.65, 47.12) * mm});
            skLineSegment(sketch, "E284", {"start": v(-11.65, 47.12) * mm, "end": v(-10.85, 47.68) * mm});
            skLineSegment(sketch, "E285", {"start": v(-10.85, 47.68) * mm, "end": v(-10.02, 48.2) * mm});
            skLineSegment(sketch, "E286", {"start": v(-10.02, 48.2) * mm, "end": v(-9.16, 48.68) * mm});
            skLineSegment(sketch, "E287", {"start": v(-9.16, 48.68) * mm, "end": v(-8.26, 49.12) * mm});
            skLineSegment(sketch, "E288", {"start": v(-8.26, 49.12) * mm, "end": v(-7.34, 49.51) * mm});
            skLineSegment(sketch, "E289", {"start": v(-7.34, 49.51) * mm, "end": v(-6.4, 49.86) * mm});
            skLineSegment(sketch, "E290", {"start": v(-6.4, 49.86) * mm, "end": v(-5.42, 50.17) * mm});
            skLineSegment(sketch, "E291", {"start": v(-5.42, 50.17) * mm, "end": v(-4.42, 50.43) * mm});
            skLineSegment(sketch, "E292", {"start": v(-4.42, 50.43) * mm, "end": v(-3.4, 50.64) * mm});
            skLineSegment(sketch, "E293", {"start": v(-3.4, 50.64) * mm, "end": v(-2.35, 50.8) * mm});
            skLineSegment(sketch, "E294", {"start": v(-2.35, 50.8) * mm, "end": v(-1.27, 50.9) * mm});
            skLineSegment(sketch, "E295", {"start": v(-1.27, 50.9) * mm, "end": v(-0.18, 50.95) * mm});
            skLineSegment(sketch, "E296", {"start": v(-0.18, 50.95) * mm, "end": v(0.94, 50.94) * mm});
            skLineSegment(sketch, "E297", {"start": v(0.94, 50.94) * mm, "end": v(1.88, 50.9) * mm});
            skLineSegment(sketch, "E298", {"start": v(1.88, 50.9) * mm, "end": v(2.82, 50.8) * mm});
            skLineSegment(sketch, "E299", {"start": v(2.82, 50.8) * mm, "end": v(3.75, 50.64) * mm});
            skLineSegment(sketch, "E300", {"start": v(3.75, 50.64) * mm, "end": v(4.67, 50.45) * mm});
            skLineSegment(sketch, "E301", {"start": v(4.67, 50.45) * mm, "end": v(5.58, 50.22) * mm});
            skLineSegment(sketch, "E302", {"start": v(5.58, 50.22) * mm, "end": v(6.47, 49.94) * mm});
            skLineSegment(sketch, "E303", {"start": v(6.47, 49.94) * mm, "end": v(7.35, 49.62) * mm});
            skLineSegment(sketch, "E304", {"start": v(7.35, 49.62) * mm, "end": v(8.22, 49.26) * mm});
            skLineSegment(sketch, "E305", {"start": v(8.22, 49.26) * mm, "end": v(9.07, 48.87) * mm});
            skLineSegment(sketch, "E306", {"start": v(9.07, 48.87) * mm, "end": v(9.9, 48.43) * mm});
            skLineSegment(sketch, "E307", {"start": v(9.9, 48.43) * mm, "end": v(10.7, 47.96) * mm});
            skLineSegment(sketch, "E308", {"start": v(10.7, 47.96) * mm, "end": v(11.49, 47.45) * mm});
            skLineSegment(sketch, "E309", {"start": v(11.49, 47.45) * mm, "end": v(12.25, 46.9) * mm});
            skLineSegment(sketch, "E310", {"start": v(12.25, 46.9) * mm, "end": v(12.99, 46.33) * mm});
            skLineSegment(sketch, "E311", {"start": v(12.99, 46.33) * mm, "end": v(13.7, 45.72) * mm});
            skLineSegment(sketch, "E312", {"start": v(13.7, 45.72) * mm, "end": v(14.38, 45.08) * mm});
            skLineSegment(sketch, "E313", {"start": v(14.38, 45.08) * mm, "end": v(15.03, 44.41) * mm});
            skLineSegment(sketch, "E314", {"start": v(15.03, 44.41) * mm, "end": v(15.65, 43.71) * mm});
            skLineSegment(sketch, "E315", {"start": v(15.65, 43.71) * mm, "end": v(16.23, 42.98) * mm});
            skLineSegment(sketch, "E316", {"start": v(16.23, 42.98) * mm, "end": v(16.79, 42.23) * mm});
            skLineSegment(sketch, "E317", {"start": v(16.79, 42.23) * mm, "end": v(17.3, 41.45) * mm});
            skLineSegment(sketch, "E318", {"start": v(17.3, 41.45) * mm, "end": v(17.78, 40.65) * mm});
            skLineSegment(sketch, "E319", {"start": v(17.78, 40.65) * mm, "end": v(18.21, 39.82) * mm});
            skLineSegment(sketch, "E320", {"start": v(18.21, 39.82) * mm, "end": v(18.6, 38.97) * mm});
            skLineSegment(sketch, "E321", {"start": v(18.6, 38.97) * mm, "end": v(18.96, 38.1) * mm});
            skLineSegment(sketch, "E322", {"start": v(18.96, 38.1) * mm, "end": v(19.27, 37.21) * mm});
            skLineSegment(sketch, "E323", {"start": v(19.27, 37.21) * mm, "end": v(19.53, 36.3) * mm});
            skLineSegment(sketch, "E324", {"start": v(19.53, 36.3) * mm, "end": v(19.75, 35.37) * mm});
            skLineSegment(sketch, "E325", {"start": v(19.75, 35.37) * mm, "end": v(19.91, 34.43) * mm});
            skLineSegment(sketch, "E326", {"start": v(19.91, 34.43) * mm, "end": v(20.03, 33.47) * mm});
            skLineSegment(sketch, "E327", {"start": v(20.03, 33.47) * mm, "end": v(20.1, 32.5) * mm});
            skLineSegment(sketch, "E328", {"start": v(20.1, 32.5) * mm, "end": v(20.1, 31.51) * mm});
            skLineSegment(sketch, "E329", {"start": v(16.58, 28.71) * mm, "end": v(16.5, 28.62) * mm});
            skLineSegment(sketch, "E330", {"start": v(16.5, 28.62) * mm, "end": v(16.41, 28.52) * mm});
            skLineSegment(sketch, "E331", {"start": v(16.41, 28.52) * mm, "end": v(16.32, 28.43) * mm});
            skLineSegment(sketch, "E332", {"start": v(16.32, 28.43) * mm, "end": v(16.24, 28.33) * mm});
            skLineSegment(sketch, "E333", {"start": v(16.24, 28.33) * mm, "end": v(16.15, 28.23) * mm});
            skLineSegment(sketch, "E334", {"start": v(16.15, 28.23) * mm, "end": v(16.07, 28.13) * mm});
            skLineSegment(sketch, "E335", {"start": v(16.07, 28.13) * mm, "end": v(15.98, 28.03) * mm});
            skLineSegment(sketch, "E336", {"start": v(15.98, 28.03) * mm, "end": v(15.9, 27.93) * mm});
            skLineSegment(sketch, "E337", {"start": v(15.9, 27.93) * mm, "end": v(15.8, 27.83) * mm});
            skLineSegment(sketch, "E338", {"start": v(15.8, 27.83) * mm, "end": v(15.72, 27.73) * mm});
            skLineSegment(sketch, "E339", {"start": v(15.72, 27.73) * mm, "end": v(15.63, 27.62) * mm});
            skLineSegment(sketch, "E340", {"start": v(15.63, 27.62) * mm, "end": v(15.55, 27.52) * mm});
            skLineSegment(sketch, "E341", {"start": v(15.55, 27.52) * mm, "end": v(15.46, 27.42) * mm});
            skLineSegment(sketch, "E342", {"start": v(15.46, 27.42) * mm, "end": v(15.37, 27.32) * mm});
            skLineSegment(sketch, "E343", {"start": v(15.37, 27.32) * mm, "end": v(15.28, 27.22) * mm});
            skLineSegment(sketch, "E344", {"start": v(15.28, 27.22) * mm, "end": v(15.2, 27.11) * mm});
            skLineSegment(sketch, "E345", {"start": v(15.2, 27.11) * mm, "end": v(15.1, 27.01) * mm});
            skLineSegment(sketch, "E346", {"start": v(15.1, 27.01) * mm, "end": v(15.02, 26.91) * mm});
            skLineSegment(sketch, "E347", {"start": v(15.02, 26.91) * mm, "end": v(14.93, 26.81) * mm});
            skLineSegment(sketch, "E348", {"start": v(14.93, 26.81) * mm, "end": v(14.83, 26.71) * mm});
            skLineSegment(sketch, "E349", {"start": v(14.83, 26.71) * mm, "end": v(14.74, 26.61) * mm});
            skLineSegment(sketch, "E350", {"start": v(14.74, 26.61) * mm, "end": v(14.65, 26.51) * mm});
            skLineSegment(sketch, "E351", {"start": v(14.65, 26.51) * mm, "end": v(14.55, 26.41) * mm});
            skLineSegment(sketch, "E352", {"start": v(14.55, 26.41) * mm, "end": v(14.46, 26.32) * mm});
            skLineSegment(sketch, "E353", {"start": v(14.46, 26.32) * mm, "end": v(14.36, 26.22) * mm});
            skLineSegment(sketch, "E354", {"start": v(14.36, 26.22) * mm, "end": v(14.27, 26.12) * mm});
            skLineSegment(sketch, "E355", {"start": v(14.27, 26.12) * mm, "end": v(14.17, 26.03) * mm});
            skLineSegment(sketch, "E356", {"start": v(14.17, 26.03) * mm, "end": v(14.07, 25.94) * mm});
            skLineSegment(sketch, "E357", {"start": v(14.07, 25.94) * mm, "end": v(13.97, 25.85) * mm});
            skLineSegment(sketch, "E358", {"start": v(13.97, 25.85) * mm, "end": v(13.87, 25.76) * mm});
            skLineSegment(sketch, "E359", {"start": v(13.87, 25.76) * mm, "end": v(13.77, 25.67) * mm});
            skLineSegment(sketch, "E360", {"start": v(13.77, 25.67) * mm, "end": v(13.66, 25.58) * mm});
            skLineSegment(sketch, "E361", {"start": v(13.66, 25.58) * mm, "end": v(13.47, 25.43) * mm});
            skLineSegment(sketch, "E362", {"start": v(13.47, 25.43) * mm, "end": v(13.28, 25.28) * mm});
            skLineSegment(sketch, "E363", {"start": v(13.28, 25.28) * mm, "end": v(13.1, 25.14) * mm});
            skLineSegment(sketch, "E364", {"start": v(13.1, 25.14) * mm, "end": v(12.9, 25) * mm});
            skLineSegment(sketch, "E365", {"start": v(12.9, 25) * mm, "end": v(12.7, 24.86) * mm});
            skLineSegment(sketch, "E366", {"start": v(12.7, 24.86) * mm, "end": v(12.5, 24.73) * mm});
            skLineSegment(sketch, "E367", {"start": v(12.5, 24.73) * mm, "end": v(12.3, 24.6) * mm});
            skLineSegment(sketch, "E368", {"start": v(12.3, 24.6) * mm, "end": v(12.1, 24.48) * mm});
            skLineSegment(sketch, "E369", {"start": v(12.1, 24.48) * mm, "end": v(11.9, 24.36) * mm});
            skLineSegment(sketch, "E370", {"start": v(11.9, 24.36) * mm, "end": v(11.68, 24.24) * mm});
            skLineSegment(sketch, "E371", {"start": v(11.68, 24.24) * mm, "end": v(11.48, 24.13) * mm});
            skLineSegment(sketch, "E372", {"start": v(11.48, 24.13) * mm, "end": v(11.26, 24.02) * mm});
            skLineSegment(sketch, "E373", {"start": v(11.26, 24.02) * mm, "end": v(11.05, 23.91) * mm});
            skLineSegment(sketch, "E374", {"start": v(11.05, 23.91) * mm, "end": v(10.84, 23.81) * mm});
            skLineSegment(sketch, "E375", {"start": v(10.84, 23.81) * mm, "end": v(10.62, 23.71) * mm});
            skLineSegment(sketch, "E376", {"start": v(10.62, 23.71) * mm, "end": v(10.4, 23.61) * mm});
            skLineSegment(sketch, "E377", {"start": v(10.4, 23.61) * mm, "end": v(10.19, 23.52) * mm});
            skLineSegment(sketch, "E378", {"start": v(10.19, 23.52) * mm, "end": v(9.97, 23.43) * mm});
            skLineSegment(sketch, "E379", {"start": v(9.97, 23.43) * mm, "end": v(9.75, 23.34) * mm});
            skLineSegment(sketch, "E380", {"start": v(9.75, 23.34) * mm, "end": v(9.53, 23.26) * mm});
            skLineSegment(sketch, "E381", {"start": v(9.53, 23.26) * mm, "end": v(9.3, 23.18) * mm});
            skLineSegment(sketch, "E382", {"start": v(9.3, 23.18) * mm, "end": v(9.08, 23.1) * mm});
            skLineSegment(sketch, "E383", {"start": v(9.08, 23.1) * mm, "end": v(8.85, 23.02) * mm});
            skLineSegment(sketch, "E384", {"start": v(8.85, 23.02) * mm, "end": v(8.62, 22.95) * mm});
            skLineSegment(sketch, "E385", {"start": v(8.62, 22.95) * mm, "end": v(8.4, 22.87) * mm});
            skLineSegment(sketch, "E386", {"start": v(8.4, 22.87) * mm, "end": v(8.17, 22.8) * mm});
            skLineSegment(sketch, "E387", {"start": v(8.17, 22.8) * mm, "end": v(7.94, 22.74) * mm});
            skLineSegment(sketch, "E388", {"start": v(7.94, 22.74) * mm, "end": v(7.7, 22.67) * mm});
            skLineSegment(sketch, "E389", {"start": v(7.7, 22.67) * mm, "end": v(7.48, 22.61) * mm});
            skLineSegment(sketch, "E390", {"start": v(7.48, 22.61) * mm, "end": v(7.24, 22.55) * mm});
            skLineSegment(sketch, "E391", {"start": v(7.24, 22.55) * mm, "end": v(7, 22.5) * mm});
            skLineSegment(sketch, "E392", {"start": v(7, 22.5) * mm, "end": v(6.78, 22.44) * mm});
            skLineSegment(sketch, "E393", {"start": v(6.78, 22.44) * mm, "end": v(6.56, 22.39) * mm});
            skLineSegment(sketch, "E394", {"start": v(6.56, 22.39) * mm, "end": v(6.35, 22.34) * mm});
            skLineSegment(sketch, "E395", {"start": v(6.35, 22.34) * mm, "end": v(6.13, 22.3) * mm});
            skLineSegment(sketch, "E396", {"start": v(6.13, 22.3) * mm, "end": v(5.92, 22.25) * mm});
            skLineSegment(sketch, "E397", {"start": v(5.92, 22.25) * mm, "end": v(5.7, 22.2) * mm});
            skLineSegment(sketch, "E398", {"start": v(5.7, 22.2) * mm, "end": v(5.49, 22.16) * mm});
            skLineSegment(sketch, "E399", {"start": v(5.49, 22.16) * mm, "end": v(5.27, 22.12) * mm});
            skLineSegment(sketch, "E400", {"start": v(5.27, 22.12) * mm, "end": v(5.06, 22.08) * mm});
            skLineSegment(sketch, "E401", {"start": v(5.06, 22.08) * mm, "end": v(4.84, 22.04) * mm});
            skLineSegment(sketch, "E402", {"start": v(4.84, 22.04) * mm, "end": v(4.62, 22) * mm});
            skLineSegment(sketch, "E403", {"start": v(4.62, 22) * mm, "end": v(4.4, 21.97) * mm});
            skLineSegment(sketch, "E404", {"start": v(4.4, 21.97) * mm, "end": v(4.2, 21.94) * mm});
            skLineSegment(sketch, "E405", {"start": v(4.2, 21.94) * mm, "end": v(3.97, 21.9) * mm});
            skLineSegment(sketch, "E406", {"start": v(3.97, 21.9) * mm, "end": v(3.76, 21.87) * mm});
            skLineSegment(sketch, "E407", {"start": v(3.76, 21.87) * mm, "end": v(3.54, 21.85) * mm});
            skLineSegment(sketch, "E408", {"start": v(3.54, 21.85) * mm, "end": v(3.32, 21.82) * mm});
            skLineSegment(sketch, "E409", {"start": v(3.32, 21.82) * mm, "end": v(3.1, 21.8) * mm});
            skLineSegment(sketch, "E410", {"start": v(3.1, 21.8) * mm, "end": v(2.89, 21.77) * mm});
            skLineSegment(sketch, "E411", {"start": v(2.89, 21.77) * mm, "end": v(2.67, 21.75) * mm});
            skLineSegment(sketch, "E412", {"start": v(2.67, 21.75) * mm, "end": v(2.45, 21.73) * mm});
            skLineSegment(sketch, "E413", {"start": v(2.45, 21.73) * mm, "end": v(2.23, 21.7) * mm});
            skLineSegment(sketch, "E414", {"start": v(2.23, 21.7) * mm, "end": v(2.01, 21.7) * mm});
            skLineSegment(sketch, "E415", {"start": v(2.01, 21.7) * mm, "end": v(1.8, 21.67) * mm});
            skLineSegment(sketch, "E416", {"start": v(1.8, 21.67) * mm, "end": v(1.58, 21.66) * mm});
            skLineSegment(sketch, "E417", {"start": v(1.58, 21.66) * mm, "end": v(1.36, 21.65) * mm});
            skLineSegment(sketch, "E418", {"start": v(1.36, 21.65) * mm, "end": v(1.14, 21.64) * mm});
            skLineSegment(sketch, "E419", {"start": v(1.14, 21.64) * mm, "end": v(0.92, 21.63) * mm});
            skLineSegment(sketch, "E420", {"start": v(0.92, 21.63) * mm, "end": v(0.7, 21.62) * mm});
            skLineSegment(sketch, "E421", {"start": v(0.7, 21.62) * mm, "end": v(0.48, 21.62) * mm});
            skLineSegment(sketch, "E422", {"start": v(0.48, 21.62) * mm, "end": v(0.26, 21.62) * mm});
            skLineSegment(sketch, "E423", {"start": v(0.26, 21.62) * mm, "end": v(0.04, 21.61) * mm});
            skLineSegment(sketch, "E424", {"start": v(0.04, 21.61) * mm, "end": v(-0.18, 21.61) * mm});
            skLineSegment(sketch, "E425", {"start": v(-0.18, 21.61) * mm, "end": v(-0.2, 21.61) * mm});
            skLineSegment(sketch, "E426", {"start": v(-0.2, 21.61) * mm, "end": v(-0.23, 21.61) * mm});
            skLineSegment(sketch, "E427", {"start": v(-0.23, 21.61) * mm, "end": v(-0.25, 21.61) * mm});
            skLineSegment(sketch, "E428", {"start": v(-0.25, 21.61) * mm, "end": v(-0.27, 21.61) * mm});
            skLineSegment(sketch, "E429", {"start": v(-0.27, 21.61) * mm, "end": v(-0.3, 21.6) * mm});
            skLineSegment(sketch, "E430", {"start": v(-0.3, 21.6) * mm, "end": v(-0.32, 21.6) * mm});
            skLineSegment(sketch, "E431", {"start": v(-0.32, 21.6) * mm, "end": v(-0.34, 21.6) * mm});
            skLineSegment(sketch, "E432", {"start": v(-0.34, 21.6) * mm, "end": v(-0.36, 21.6) * mm});
            skLineSegment(sketch, "E433", {"start": v(-0.36, 21.6) * mm, "end": v(-0.39, 21.6) * mm});
            skLineSegment(sketch, "E434", {"start": v(-0.39, 21.6) * mm, "end": v(-0.41, 21.6) * mm});
            skLineSegment(sketch, "E435", {"start": v(-0.41, 21.6) * mm, "end": v(-0.44, 21.59) * mm});
            skLineSegment(sketch, "E436", {"start": v(-0.44, 21.59) * mm, "end": v(-0.46, 21.58) * mm});
            skLineSegment(sketch, "E437", {"start": v(-0.46, 21.58) * mm, "end": v(-0.48, 21.58) * mm});
            skLineSegment(sketch, "E438", {"start": v(-0.48, 21.58) * mm, "end": v(-0.5, 21.57) * mm});
            skLineSegment(sketch, "E439", {"start": v(-0.5, 21.57) * mm, "end": v(-0.53, 21.56) * mm});
            skLineSegment(sketch, "E440", {"start": v(-0.53, 21.56) * mm, "end": v(-0.55, 21.56) * mm});
            skLineSegment(sketch, "E441", {"start": v(-0.55, 21.56) * mm, "end": v(-0.58, 21.55) * mm});
            skLineSegment(sketch, "E442", {"start": v(-0.58, 21.55) * mm, "end": v(-0.6, 21.54) * mm});
            skLineSegment(sketch, "E443", {"start": v(-0.6, 21.54) * mm, "end": v(-0.62, 21.53) * mm});
            skLineSegment(sketch, "E444", {"start": v(-0.62, 21.53) * mm, "end": v(-0.64, 21.52) * mm});
            skLineSegment(sketch, "E445", {"start": v(-0.64, 21.52) * mm, "end": v(-0.66, 21.52) * mm});
            skLineSegment(sketch, "E446", {"start": v(-0.66, 21.52) * mm, "end": v(-0.68, 21.5) * mm});
            skLineSegment(sketch, "E447", {"start": v(-0.68, 21.5) * mm, "end": v(-0.7, 21.5) * mm});
            skLineSegment(sketch, "E448", {"start": v(-0.7, 21.5) * mm, "end": v(-0.71, 21.49) * mm});
            skLineSegment(sketch, "E449", {"start": v(-0.71, 21.49) * mm, "end": v(-0.73, 21.48) * mm});
            skLineSegment(sketch, "E450", {"start": v(-0.73, 21.48) * mm, "end": v(-0.74, 21.47) * mm});
            skLineSegment(sketch, "E451", {"start": v(-0.74, 21.47) * mm, "end": v(-0.76, 21.45) * mm});
            skLineSegment(sketch, "E452", {"start": v(-0.76, 21.45) * mm, "end": v(-0.77, 21.44) * mm});
            skLineSegment(sketch, "E453", {"start": v(-0.77, 21.44) * mm, "end": v(-0.78, 21.43) * mm});
            skLineSegment(sketch, "E454", {"start": v(-0.78, 21.43) * mm, "end": v(-0.79, 21.42) * mm});
            skLineSegment(sketch, "E455", {"start": v(-0.79, 21.42) * mm, "end": v(-0.8, 21.4) * mm});
            skLineSegment(sketch, "E456", {"start": v(-0.8, 21.4) * mm, "end": v(-0.8, 21.4) * mm});
            skLineSegment(sketch, "E457", {"start": v(-0.8, 21.4) * mm, "end": v(-0.86, 21.25) * mm});
            skLineSegment(sketch, "E458", {"start": v(-0.86, 21.25) * mm, "end": v(-0.92, 21.11) * mm});
            skLineSegment(sketch, "E459", {"start": v(-0.92, 21.11) * mm, "end": v(-0.98, 20.97) * mm});
            skLineSegment(sketch, "E460", {"start": v(-0.98, 20.97) * mm, "end": v(-1.04, 20.83) * mm});
            skLineSegment(sketch, "E461", {"start": v(-1.04, 20.83) * mm, "end": v(-1.1, 20.7) * mm});
            skLineSegment(sketch, "E462", {"start": v(-1.1, 20.7) * mm, "end": v(-1.16, 20.55) * mm});
            skLineSegment(sketch, "E463", {"start": v(-1.16, 20.55) * mm, "end": v(-1.22, 20.41) * mm});
            skLineSegment(sketch, "E464", {"start": v(-1.22, 20.41) * mm, "end": v(-1.28, 20.28) * mm});
            skLineSegment(sketch, "E465", {"start": v(-1.28, 20.28) * mm, "end": v(-1.34, 20.14) * mm});
            skLineSegment(sketch, "E466", {"start": v(-1.34, 20.14) * mm, "end": v(-1.4, 20) * mm});
            skLineSegment(sketch, "E467", {"start": v(-1.4, 20) * mm, "end": v(-1.46, 19.86) * mm});
            skLineSegment(sketch, "E468", {"start": v(-1.46, 19.86) * mm, "end": v(-1.52, 19.72) * mm});
            skLineSegment(sketch, "E469", {"start": v(-1.52, 19.72) * mm, "end": v(-1.58, 19.58) * mm});
            skLineSegment(sketch, "E470", {"start": v(-1.58, 19.58) * mm, "end": v(-1.64, 19.44) * mm});
            skLineSegment(sketch, "E471", {"start": v(-1.64, 19.44) * mm, "end": v(-1.7, 19.3) * mm});
            skLineSegment(sketch, "E472", {"start": v(-1.7, 19.3) * mm, "end": v(-1.75, 19.16) * mm});
            skLineSegment(sketch, "E473", {"start": v(-1.75, 19.16) * mm, "end": v(-1.8, 19.01) * mm});
            skLineSegment(sketch, "E474", {"start": v(-1.8, 19.01) * mm, "end": v(-1.86, 18.87) * mm});
            skLineSegment(sketch, "E475", {"start": v(-1.86, 18.87) * mm, "end": v(-1.91, 18.73) * mm});
            skLineSegment(sketch, "E476", {"start": v(-1.91, 18.73) * mm, "end": v(-1.96, 18.58) * mm});
            skLineSegment(sketch, "E477", {"start": v(-1.96, 18.58) * mm, "end": v(-2, 18.44) * mm});
            skLineSegment(sketch, "E478", {"start": v(-2, 18.44) * mm, "end": v(-2.05, 18.3) * mm});
            skLineSegment(sketch, "E479", {"start": v(-2.05, 18.3) * mm, "end": v(-2.1, 18.15) * mm});
            skLineSegment(sketch, "E480", {"start": v(-2.1, 18.15) * mm, "end": v(-2.13, 18) * mm});
            skLineSegment(sketch, "E481", {"start": v(-2.13, 18) * mm, "end": v(-2.17, 17.85) * mm});
            skLineSegment(sketch, "E482", {"start": v(-2.17, 17.85) * mm, "end": v(-2.2, 17.7) * mm});
            skLineSegment(sketch, "E483", {"start": v(-2.2, 17.7) * mm, "end": v(-2.23, 17.55) * mm});
            skLineSegment(sketch, "E484", {"start": v(-2.23, 17.55) * mm, "end": v(-2.26, 17.4) * mm});
            skLineSegment(sketch, "E485", {"start": v(-2.26, 17.4) * mm, "end": v(-2.28, 17.25) * mm});
            skLineSegment(sketch, "E486", {"start": v(-2.28, 17.25) * mm, "end": v(-2.3, 17.1) * mm});
            skLineSegment(sketch, "E487", {"start": v(-2.3, 17.1) * mm, "end": v(-2.32, 16.94) * mm});
            skLineSegment(sketch, "E488", {"start": v(-2.32, 16.94) * mm, "end": v(-2.33, 16.78) * mm});
            skLineSegment(sketch, "E489", {"start": v(-2.33, 16.78) * mm, "end": v(-2.34, 16.65) * mm});
            skLineSegment(sketch, "E490", {"start": v(-2.34, 16.65) * mm, "end": v(-2.34, 16.52) * mm});
            skLineSegment(sketch, "E491", {"start": v(-2.34, 16.52) * mm, "end": v(-2.34, 16.4) * mm});
            skLineSegment(sketch, "E492", {"start": v(-2.34, 16.4) * mm, "end": v(-2.34, 16.28) * mm});
            skLineSegment(sketch, "E493", {"start": v(-2.34, 16.28) * mm, "end": v(-2.33, 16.17) * mm});
            skLineSegment(sketch, "E494", {"start": v(-2.33, 16.17) * mm, "end": v(-2.32, 16.05) * mm});
            skLineSegment(sketch, "E495", {"start": v(-2.32, 16.05) * mm, "end": v(-2.3, 15.94) * mm});
            skLineSegment(sketch, "E496", {"start": v(-2.3, 15.94) * mm, "end": v(-2.28, 15.83) * mm});
            skLineSegment(sketch, "E497", {"start": v(-2.28, 15.83) * mm, "end": v(-2.26, 15.73) * mm});
            skLineSegment(sketch, "E498", {"start": v(-2.26, 15.73) * mm, "end": v(-2.24, 15.63) * mm});
            skLineSegment(sketch, "E499", {"start": v(-2.24, 15.63) * mm, "end": v(-2.2, 15.53) * mm});
            skLineSegment(sketch, "E500", {"start": v(-2.2, 15.53) * mm, "end": v(-2.17, 15.44) * mm});
            skLineSegment(sketch, "E501", {"start": v(-2.17, 15.44) * mm, "end": v(-2.14, 15.35) * mm});
            skLineSegment(sketch, "E502", {"start": v(-2.14, 15.35) * mm, "end": v(-2.1, 15.26) * mm});
            skLineSegment(sketch, "E503", {"start": v(-2.1, 15.26) * mm, "end": v(-2.05, 15.17) * mm});
            skLineSegment(sketch, "E504", {"start": v(-2.05, 15.17) * mm, "end": v(-2, 15.1) * mm});
            skLineSegment(sketch, "E505", {"start": v(-2, 15.1) * mm, "end": v(-1.94, 15.02) * mm});
            skLineSegment(sketch, "E506", {"start": v(-1.94, 15.02) * mm, "end": v(-1.89, 14.94) * mm});
            skLineSegment(sketch, "E507", {"start": v(-1.89, 14.94) * mm, "end": v(-1.82, 14.87) * mm});
            skLineSegment(sketch, "E508", {"start": v(-1.82, 14.87) * mm, "end": v(-1.76, 14.8) * mm});
            skLineSegment(sketch, "E509", {"start": v(-1.76, 14.8) * mm, "end": v(-1.68, 14.74) * mm});
            skLineSegment(sketch, "E510", {"start": v(-1.68, 14.74) * mm, "end": v(-1.6, 14.69) * mm});
            skLineSegment(sketch, "E511", {"start": v(-1.6, 14.69) * mm, "end": v(-1.53, 14.63) * mm});
            skLineSegment(sketch, "E512", {"start": v(-1.53, 14.63) * mm, "end": v(-1.44, 14.58) * mm});
            skLineSegment(sketch, "E513", {"start": v(-1.44, 14.58) * mm, "end": v(-1.35, 14.53) * mm});
            skLineSegment(sketch, "E514", {"start": v(-1.35, 14.53) * mm, "end": v(-1.25, 14.5) * mm});
            skLineSegment(sketch, "E515", {"start": v(-1.25, 14.5) * mm, "end": v(-1.15, 14.45) * mm});
            skLineSegment(sketch, "E516", {"start": v(-1.15, 14.45) * mm, "end": v(-1.05, 14.42) * mm});
            skLineSegment(sketch, "E517", {"start": v(-1.05, 14.42) * mm, "end": v(-0.93, 14.39) * mm});
            skLineSegment(sketch, "E518", {"start": v(-0.93, 14.39) * mm, "end": v(-0.82, 14.36) * mm});
            skLineSegment(sketch, "E519", {"start": v(-0.82, 14.36) * mm, "end": v(-0.7, 14.34) * mm});
            skLineSegment(sketch, "E520", {"start": v(-0.7, 14.34) * mm, "end": v(-0.57, 14.32) * mm});
            skLineSegment(sketch, "E521", {"start": v(-0.57, 14.32) * mm, "end": v(-0.46, 14.3) * mm});
            skLineSegment(sketch, "E522", {"start": v(-0.46, 14.3) * mm, "end": v(-0.35, 14.3) * mm});
            skLineSegment(sketch, "E523", {"start": v(-0.35, 14.3) * mm, "end": v(-0.24, 14.28) * mm});
            skLineSegment(sketch, "E524", {"start": v(-0.24, 14.28) * mm, "end": v(-0.13, 14.27) * mm});
            skLineSegment(sketch, "E525", {"start": v(-0.13, 14.27) * mm, "end": v(-0.02, 14.26) * mm});
            skLineSegment(sketch, "E526", {"start": v(-0.02, 14.26) * mm, "end": v(0.09, 14.25) * mm});
            skLineSegment(sketch, "E527", {"start": v(0.09, 14.25) * mm, "end": v(0.2, 14.24) * mm});
            skLineSegment(sketch, "E528", {"start": v(0.2, 14.24) * mm, "end": v(0.3, 14.23) * mm});
            skLineSegment(sketch, "E529", {"start": v(0.3, 14.23) * mm, "end": v(0.42, 14.23) * mm});
            skLineSegment(sketch, "E530", {"start": v(0.42, 14.23) * mm, "end": v(0.53, 14.22) * mm});
            skLineSegment(sketch, "E531", {"start": v(0.53, 14.22) * mm, "end": v(0.64, 14.22) * mm});
            skLineSegment(sketch, "E532", {"start": v(0.64, 14.22) * mm, "end": v(0.75, 14.21) * mm});
            skLineSegment(sketch, "E533", {"start": v(0.75, 14.21) * mm, "end": v(0.86, 14.2) * mm});
            skLineSegment(sketch, "E534", {"start": v(0.86, 14.2) * mm, "end": v(0.97, 14.2) * mm});
            skLineSegment(sketch, "E535", {"start": v(0.97, 14.2) * mm, "end": v(1.09, 14.2) * mm});
            skLineSegment(sketch, "E536", {"start": v(1.09, 14.2) * mm, "end": v(1.2, 14.2) * mm});
            skLineSegment(sketch, "E537", {"start": v(1.2, 14.2) * mm, "end": v(1.3, 14.2) * mm});
            skLineSegment(sketch, "E538", {"start": v(1.3, 14.2) * mm, "end": v(1.42, 14.2) * mm});
            skLineSegment(sketch, "E539", {"start": v(1.42, 14.2) * mm, "end": v(1.53, 14.21) * mm});
            skLineSegment(sketch, "E540", {"start": v(1.53, 14.21) * mm, "end": v(1.64, 14.21) * mm});
            skLineSegment(sketch, "E541", {"start": v(1.64, 14.21) * mm, "end": v(1.75, 14.22) * mm});
            skLineSegment(sketch, "E542", {"start": v(1.75, 14.22) * mm, "end": v(1.86, 14.23) * mm});
            skLineSegment(sketch, "E543", {"start": v(1.86, 14.23) * mm, "end": v(1.97, 14.23) * mm});
            skLineSegment(sketch, "E544", {"start": v(1.97, 14.23) * mm, "end": v(2.08, 14.24) * mm});
            skLineSegment(sketch, "E545", {"start": v(2.08, 14.24) * mm, "end": v(2.2, 14.25) * mm});
            skLineSegment(sketch, "E546", {"start": v(2.2, 14.25) * mm, "end": v(2.3, 14.26) * mm});
            skLineSegment(sketch, "E547", {"start": v(2.3, 14.26) * mm, "end": v(2.41, 14.27) * mm});
            skLineSegment(sketch, "E548", {"start": v(2.41, 14.27) * mm, "end": v(2.52, 14.29) * mm});
            skLineSegment(sketch, "E549", {"start": v(2.52, 14.29) * mm, "end": v(2.63, 14.3) * mm});
            skLineSegment(sketch, "E550", {"start": v(2.63, 14.3) * mm, "end": v(2.74, 14.32) * mm});
            skLineSegment(sketch, "E551", {"start": v(2.74, 14.32) * mm, "end": v(2.85, 14.33) * mm});
            skLineSegment(sketch, "E552", {"start": v(2.85, 14.33) * mm, "end": v(2.95, 14.35) * mm});
            skLineSegment(sketch, "E553", {"start": v(2.95, 14.35) * mm, "end": v(3.16, 14.4) * mm});
            skLineSegment(sketch, "E554", {"start": v(3.16, 14.4) * mm, "end": v(3.37, 14.43) * mm});
            skLineSegment(sketch, "E555", {"start": v(3.37, 14.43) * mm, "end": v(3.58, 14.48) * mm});
            skLineSegment(sketch, "E556", {"start": v(3.58, 14.48) * mm, "end": v(3.79, 14.52) * mm});
            skLineSegment(sketch, "E557", {"start": v(3.79, 14.52) * mm, "end": v(4, 14.57) * mm});
            skLineSegment(sketch, "E558", {"start": v(4, 14.57) * mm, "end": v(4.2, 14.62) * mm});
            skLineSegment(sketch, "E559", {"start": v(4.2, 14.62) * mm, "end": v(4.4, 14.68) * mm});
            skLineSegment(sketch, "E560", {"start": v(4.4, 14.68) * mm, "end": v(4.6, 14.73) * mm});
            skLineSegment(sketch, "E561", {"start": v(4.6, 14.73) * mm, "end": v(4.8, 14.8) * mm});
            skLineSegment(sketch, "E562", {"start": v(4.8, 14.8) * mm, "end": v(5, 14.86) * mm});
            skLineSegment(sketch, "E563", {"start": v(5, 14.86) * mm, "end": v(5.2, 14.92) * mm});
            skLineSegment(sketch, "E564", {"start": v(5.2, 14.92) * mm, "end": v(5.4, 14.99) * mm});
            skLineSegment(sketch, "E565", {"start": v(5.4, 14.99) * mm, "end": v(5.6, 15.06) * mm});
            skLineSegment(sketch, "E566", {"start": v(5.6, 15.06) * mm, "end": v(5.8, 15.13) * mm});
            skLineSegment(sketch, "E567", {"start": v(5.8, 15.13) * mm, "end": v(6, 15.2) * mm});
            skLineSegment(sketch, "E568", {"start": v(6, 15.2) * mm, "end": v(6.2, 15.28) * mm});
            skLineSegment(sketch, "E569", {"start": v(6.2, 15.28) * mm, "end": v(6.4, 15.36) * mm});
            skLineSegment(sketch, "E570", {"start": v(6.4, 15.36) * mm, "end": v(6.6, 15.44) * mm});
            skLineSegment(sketch, "E571", {"start": v(6.6, 15.44) * mm, "end": v(6.79, 15.52) * mm});
            skLineSegment(sketch, "E572", {"start": v(6.79, 15.52) * mm, "end": v(6.98, 15.6) * mm});
            skLineSegment(sketch, "E573", {"start": v(6.98, 15.6) * mm, "end": v(7.17, 15.7) * mm});
            skLineSegment(sketch, "E574", {"start": v(7.17, 15.7) * mm, "end": v(7.36, 15.78) * mm});
            skLineSegment(sketch, "E575", {"start": v(7.36, 15.78) * mm, "end": v(7.55, 15.88) * mm});
            skLineSegment(sketch, "E576", {"start": v(7.55, 15.88) * mm, "end": v(7.74, 15.97) * mm});
            skLineSegment(sketch, "E577", {"start": v(7.74, 15.97) * mm, "end": v(7.93, 16.07) * mm});
            skLineSegment(sketch, "E578", {"start": v(7.93, 16.07) * mm, "end": v(8.12, 16.16) * mm});
            skLineSegment(sketch, "E579", {"start": v(8.12, 16.16) * mm, "end": v(8.3, 16.26) * mm});
            skLineSegment(sketch, "E580", {"start": v(8.3, 16.26) * mm, "end": v(8.5, 16.37) * mm});
            skLineSegment(sketch, "E581", {"start": v(8.5, 16.37) * mm, "end": v(8.68, 16.47) * mm});
            skLineSegment(sketch, "E582", {"start": v(8.68, 16.47) * mm, "end": v(8.87, 16.58) * mm});
            skLineSegment(sketch, "E583", {"start": v(8.87, 16.58) * mm, "end": v(9.05, 16.69) * mm});
            skLineSegment(sketch, "E584", {"start": v(9.05, 16.69) * mm, "end": v(9.24, 16.8) * mm});
            skLineSegment(sketch, "E585", {"start": v(9.24, 16.8) * mm, "end": v(9.46, 16.93) * mm});
            skLineSegment(sketch, "E586", {"start": v(9.46, 16.93) * mm, "end": v(9.68, 17.07) * mm});
            skLineSegment(sketch, "E587", {"start": v(9.68, 17.07) * mm, "end": v(9.9, 17.21) * mm});
            skLineSegment(sketch, "E588", {"start": v(9.9, 17.21) * mm, "end": v(10.1, 17.36) * mm});
            skLineSegment(sketch, "E589", {"start": v(10.1, 17.36) * mm, "end": v(10.31, 17.5) * mm});
            skLineSegment(sketch, "E590", {"start": v(10.31, 17.5) * mm, "end": v(10.52, 17.66) * mm});
            skLineSegment(sketch, "E591", {"start": v(10.52, 17.66) * mm, "end": v(10.72, 17.81) * mm});
            skLineSegment(sketch, "E592", {"start": v(10.72, 17.81) * mm, "end": v(10.92, 17.97) * mm});
            skLineSegment(sketch, "E593", {"start": v(10.92, 17.97) * mm, "end": v(11.11, 18.13) * mm});
            skLineSegment(sketch, "E594", {"start": v(11.11, 18.13) * mm, "end": v(11.3, 18.3) * mm});
            skLineSegment(sketch, "E595", {"start": v(11.3, 18.3) * mm, "end": v(11.5, 18.46) * mm});
            skLineSegment(sketch, "E596", {"start": v(11.5, 18.46) * mm, "end": v(11.68, 18.63) * mm});
            skLineSegment(sketch, "E597", {"start": v(11.68, 18.63) * mm, "end": v(11.87, 18.8) * mm});
            skLineSegment(sketch, "E598", {"start": v(11.87, 18.8) * mm, "end": v(12.05, 18.97) * mm});
            skLineSegment(sketch, "E599", {"start": v(12.05, 18.97) * mm, "end": v(12.23, 19.15) * mm});
            skLineSegment(sketch, "E600", {"start": v(12.23, 19.15) * mm, "end": v(12.4, 19.33) * mm});
            skLineSegment(sketch, "E601", {"start": v(12.4, 19.33) * mm, "end": v(12.57, 19.51) * mm});
            skLineSegment(sketch, "E602", {"start": v(12.57, 19.51) * mm, "end": v(12.74, 19.7) * mm});
            skLineSegment(sketch, "E603", {"start": v(12.74, 19.7) * mm, "end": v(12.9, 19.89) * mm});
            skLineSegment(sketch, "E604", {"start": v(12.9, 19.89) * mm, "end": v(13.07, 20.08) * mm});
            skLineSegment(sketch, "E605", {"start": v(13.07, 20.08) * mm, "end": v(13.23, 20.27) * mm});
            skLineSegment(sketch, "E606", {"start": v(13.23, 20.27) * mm, "end": v(13.38, 20.47) * mm});
            skLineSegment(sketch, "E607", {"start": v(13.38, 20.47) * mm, "end": v(13.54, 20.67) * mm});
            skLineSegment(sketch, "E608", {"start": v(13.54, 20.67) * mm, "end": v(13.69, 20.88) * mm});
            skLineSegment(sketch, "E609", {"start": v(13.69, 20.88) * mm, "end": v(13.83, 21.08) * mm});
            skLineSegment(sketch, "E610", {"start": v(13.83, 21.08) * mm, "end": v(13.98, 21.3) * mm});
            skLineSegment(sketch, "E611", {"start": v(13.98, 21.3) * mm, "end": v(14.12, 21.5) * mm});
            skLineSegment(sketch, "E612", {"start": v(14.12, 21.5) * mm, "end": v(14.26, 21.72) * mm});
            skLineSegment(sketch, "E613", {"start": v(14.26, 21.72) * mm, "end": v(14.4, 21.94) * mm});
            skLineSegment(sketch, "E614", {"start": v(14.4, 21.94) * mm, "end": v(14.52, 22.16) * mm});
            skLineSegment(sketch, "E615", {"start": v(14.52, 22.16) * mm, "end": v(14.65, 22.38) * mm});
            skLineSegment(sketch, "E616", {"start": v(14.65, 22.38) * mm, "end": v(14.78, 22.61) * mm});
            skLineSegment(sketch, "E617", {"start": v(14.78, 22.61) * mm, "end": v(14.88, 22.8) * mm});
            skLineSegment(sketch, "E618", {"start": v(14.88, 22.8) * mm, "end": v(14.97, 22.98) * mm});
            skLineSegment(sketch, "E619", {"start": v(14.97, 22.98) * mm, "end": v(15.07, 23.16) * mm});
            skLineSegment(sketch, "E620", {"start": v(15.07, 23.16) * mm, "end": v(15.16, 23.35) * mm});
            skLineSegment(sketch, "E621", {"start": v(15.16, 23.35) * mm, "end": v(15.24, 23.54) * mm});
            skLineSegment(sketch, "E622", {"start": v(15.24, 23.54) * mm, "end": v(15.33, 23.72) * mm});
            skLineSegment(sketch, "E623", {"start": v(15.33, 23.72) * mm, "end": v(15.41, 23.91) * mm});
            skLineSegment(sketch, "E624", {"start": v(15.41, 23.91) * mm, "end": v(15.5, 24.1) * mm});
            skLineSegment(sketch, "E625", {"start": v(15.5, 24.1) * mm, "end": v(15.57, 24.29) * mm});
            skLineSegment(sketch, "E626", {"start": v(15.57, 24.29) * mm, "end": v(15.64, 24.48) * mm});
            skLineSegment(sketch, "E627", {"start": v(15.64, 24.48) * mm, "end": v(15.71, 24.67) * mm});
            skLineSegment(sketch, "E628", {"start": v(15.71, 24.67) * mm, "end": v(15.78, 24.86) * mm});
            skLineSegment(sketch, "E629", {"start": v(15.78, 24.86) * mm, "end": v(15.85, 25.05) * mm});
            skLineSegment(sketch, "E630", {"start": v(15.85, 25.05) * mm, "end": v(15.91, 25.24) * mm});
            skLineSegment(sketch, "E631", {"start": v(15.91, 25.24) * mm, "end": v(15.97, 25.43) * mm});
            skLineSegment(sketch, "E632", {"start": v(15.97, 25.43) * mm, "end": v(16.03, 25.62) * mm});
            skLineSegment(sketch, "E633", {"start": v(16.03, 25.62) * mm, "end": v(16.08, 25.82) * mm});
            skLineSegment(sketch, "E634", {"start": v(16.08, 25.82) * mm, "end": v(16.14, 26) * mm});
            skLineSegment(sketch, "E635", {"start": v(16.14, 26) * mm, "end": v(16.19, 26.2) * mm});
            skLineSegment(sketch, "E636", {"start": v(16.19, 26.2) * mm, "end": v(16.23, 26.4) * mm});
            skLineSegment(sketch, "E637", {"start": v(16.23, 26.4) * mm, "end": v(16.28, 26.59) * mm});
            skLineSegment(sketch, "E638", {"start": v(16.28, 26.59) * mm, "end": v(16.32, 26.78) * mm});
            skLineSegment(sketch, "E639", {"start": v(16.32, 26.78) * mm, "end": v(16.36, 26.97) * mm});
            skLineSegment(sketch, "E640", {"start": v(16.36, 26.97) * mm, "end": v(16.4, 27.17) * mm});
            skLineSegment(sketch, "E641", {"start": v(16.4, 27.17) * mm, "end": v(16.43, 27.36) * mm});
            skLineSegment(sketch, "E642", {"start": v(16.43, 27.36) * mm, "end": v(16.46, 27.55) * mm});
            skLineSegment(sketch, "E643", {"start": v(16.46, 27.55) * mm, "end": v(16.49, 27.75) * mm});
            skLineSegment(sketch, "E644", {"start": v(16.49, 27.75) * mm, "end": v(16.51, 27.94) * mm});
            skLineSegment(sketch, "E645", {"start": v(16.51, 27.94) * mm, "end": v(16.53, 28.13) * mm});
            skLineSegment(sketch, "E646", {"start": v(16.53, 28.13) * mm, "end": v(16.55, 28.33) * mm});
            skLineSegment(sketch, "E647", {"start": v(16.55, 28.33) * mm, "end": v(16.57, 28.52) * mm});
            skLineSegment(sketch, "E648", {"start": v(16.57, 28.52) * mm, "end": v(16.58, 28.71) * mm});
            skLineSegment(sketch, "E649", {"start": v(1.22, 40.8) * mm, "end": v(1.27, 40.92) * mm});
            skLineSegment(sketch, "E650", {"start": v(1.27, 40.92) * mm, "end": v(1.32, 41.04) * mm});
            skLineSegment(sketch, "E651", {"start": v(1.32, 41.04) * mm, "end": v(1.37, 41.16) * mm});
            skLineSegment(sketch, "E652", {"start": v(1.37, 41.16) * mm, "end": v(1.42, 41.29) * mm});
            skLineSegment(sketch, "E653", {"start": v(1.42, 41.29) * mm, "end": v(1.46, 41.4) * mm});
            skLineSegment(sketch, "E654", {"start": v(1.46, 41.4) * mm, "end": v(1.51, 41.53) * mm});
            skLineSegment(sketch, "E655", {"start": v(1.51, 41.53) * mm, "end": v(1.56, 41.65) * mm});
            skLineSegment(sketch, "E656", {"start": v(1.56, 41.65) * mm, "end": v(1.61, 41.78) * mm});
            skLineSegment(sketch, "E657", {"start": v(1.61, 41.78) * mm, "end": v(1.66, 41.9) * mm});
            skLineSegment(sketch, "E658", {"start": v(1.66, 41.9) * mm, "end": v(1.7, 42.02) * mm});
            skLineSegment(sketch, "E659", {"start": v(1.7, 42.02) * mm, "end": v(1.76, 42.14) * mm});
            skLineSegment(sketch, "E660", {"start": v(1.76, 42.14) * mm, "end": v(1.8, 42.27) * mm});
            skLineSegment(sketch, "E661", {"start": v(1.8, 42.27) * mm, "end": v(1.86, 42.39) * mm});
            skLineSegment(sketch, "E662", {"start": v(1.86, 42.39) * mm, "end": v(1.9, 42.5) * mm});
            skLineSegment(sketch, "E663", {"start": v(1.9, 42.5) * mm, "end": v(1.95, 42.63) * mm});
            skLineSegment(sketch, "E664", {"start": v(1.95, 42.63) * mm, "end": v(2, 42.75) * mm});
            skLineSegment(sketch, "E665", {"start": v(2, 42.75) * mm, "end": v(2.05, 42.87) * mm});
            skLineSegment(sketch, "E666", {"start": v(2.05, 42.87) * mm, "end": v(2.1, 43) * mm});
            skLineSegment(sketch, "E667", {"start": v(2.1, 43) * mm, "end": v(2.14, 43.12) * mm});
            skLineSegment(sketch, "E668", {"start": v(2.14, 43.12) * mm, "end": v(2.19, 43.24) * mm});
            skLineSegment(sketch, "E669", {"start": v(2.19, 43.24) * mm, "end": v(2.23, 43.36) * mm});
            skLineSegment(sketch, "E670", {"start": v(2.23, 43.36) * mm, "end": v(2.28, 43.48) * mm});
            skLineSegment(sketch, "E671", {"start": v(2.28, 43.48) * mm, "end": v(2.33, 43.6) * mm});
            skLineSegment(sketch, "E672", {"start": v(2.33, 43.6) * mm, "end": v(2.37, 43.73) * mm});
            skLineSegment(sketch, "E673", {"start": v(2.37, 43.73) * mm, "end": v(2.41, 43.85) * mm});
            skLineSegment(sketch, "E674", {"start": v(2.41, 43.85) * mm, "end": v(2.46, 43.97) * mm});
            skLineSegment(sketch, "E675", {"start": v(2.46, 43.97) * mm, "end": v(2.5, 44.1) * mm});
            skLineSegment(sketch, "E676", {"start": v(2.5, 44.1) * mm, "end": v(2.54, 44.22) * mm});
            skLineSegment(sketch, "E677", {"start": v(2.54, 44.22) * mm, "end": v(2.58, 44.34) * mm});
            skLineSegment(sketch, "E678", {"start": v(2.58, 44.34) * mm, "end": v(2.62, 44.46) * mm});
            skLineSegment(sketch, "E679", {"start": v(2.62, 44.46) * mm, "end": v(2.66, 44.59) * mm});
            skLineSegment(sketch, "E680", {"start": v(2.66, 44.59) * mm, "end": v(2.7, 44.71) * mm});
            skLineSegment(sketch, "E681", {"start": v(2.7, 44.71) * mm, "end": v(2.74, 44.87) * mm});
            skLineSegment(sketch, "E682", {"start": v(2.74, 44.87) * mm, "end": v(2.78, 45.03) * mm});
            skLineSegment(sketch, "E683", {"start": v(2.78, 45.03) * mm, "end": v(2.8, 45.18) * mm});
            skLineSegment(sketch, "E684", {"start": v(2.8, 45.18) * mm, "end": v(2.83, 45.34) * mm});
            skLineSegment(sketch, "E685", {"start": v(2.83, 45.34) * mm, "end": v(2.84, 45.49) * mm});
            skLineSegment(sketch, "E686", {"start": v(2.84, 45.49) * mm, "end": v(2.84, 45.63) * mm});
            skLineSegment(sketch, "E687", {"start": v(2.84, 45.63) * mm, "end": v(2.84, 45.78) * mm});
            skLineSegment(sketch, "E688", {"start": v(2.84, 45.78) * mm, "end": v(2.83, 45.92) * mm});
            skLineSegment(sketch, "E689", {"start": v(2.83, 45.92) * mm, "end": v(2.8, 46.06) * mm});
            skLineSegment(sketch, "E690", {"start": v(2.8, 46.06) * mm, "end": v(2.78, 46.2) * mm});
            skLineSegment(sketch, "E691", {"start": v(2.78, 46.2) * mm, "end": v(2.75, 46.32) * mm});
            skLineSegment(sketch, "E692", {"start": v(2.75, 46.32) * mm, "end": v(2.7, 46.45) * mm});
            skLineSegment(sketch, "E693", {"start": v(2.7, 46.45) * mm, "end": v(2.66, 46.57) * mm});
            skLineSegment(sketch, "E694", {"start": v(2.66, 46.57) * mm, "end": v(2.6, 46.69) * mm});
            skLineSegment(sketch, "E695", {"start": v(2.6, 46.69) * mm, "end": v(2.54, 46.8) * mm});
            skLineSegment(sketch, "E696", {"start": v(2.54, 46.8) * mm, "end": v(2.47, 46.91) * mm});
            skLineSegment(sketch, "E697", {"start": v(2.47, 46.91) * mm, "end": v(2.4, 47.02) * mm});
            skLineSegment(sketch, "E698", {"start": v(2.4, 47.02) * mm, "end": v(2.32, 47.11) * mm});
            skLineSegment(sketch, "E699", {"start": v(2.32, 47.11) * mm, "end": v(2.23, 47.2) * mm});
            skLineSegment(sketch, "E700", {"start": v(2.23, 47.2) * mm, "end": v(2.14, 47.3) * mm});
            skLineSegment(sketch, "E701", {"start": v(2.14, 47.3) * mm, "end": v(2.04, 47.38) * mm});
            skLineSegment(sketch, "E702", {"start": v(2.04, 47.38) * mm, "end": v(1.94, 47.46) * mm});
            skLineSegment(sketch, "E703", {"start": v(1.94, 47.46) * mm, "end": v(1.83, 47.53) * mm});
            skLineSegment(sketch, "E704", {"start": v(1.83, 47.53) * mm, "end": v(1.72, 47.6) * mm});
            skLineSegment(sketch, "E705", {"start": v(1.72, 47.6) * mm, "end": v(1.6, 47.66) * mm});
            skLineSegment(sketch, "E706", {"start": v(1.6, 47.66) * mm, "end": v(1.47, 47.71) * mm});
            skLineSegment(sketch, "E707", {"start": v(1.47, 47.71) * mm, "end": v(1.34, 47.76) * mm});
            skLineSegment(sketch, "E708", {"start": v(1.34, 47.76) * mm, "end": v(1.2, 47.8) * mm});
            skLineSegment(sketch, "E709", {"start": v(1.2, 47.8) * mm, "end": v(1.07, 47.83) * mm});
            skLineSegment(sketch, "E710", {"start": v(1.07, 47.83) * mm, "end": v(0.93, 47.86) * mm});
            skLineSegment(sketch, "E711", {"start": v(0.93, 47.86) * mm, "end": v(0.78, 47.88) * mm});
            skLineSegment(sketch, "E712", {"start": v(0.78, 47.88) * mm, "end": v(0.63, 47.9) * mm});
            skLineSegment(sketch, "E713", {"start": v(0.63, 47.9) * mm, "end": v(0.37, 47.9) * mm});
            skLineSegment(sketch, "E714", {"start": v(0.37, 47.9) * mm, "end": v(0.1, 47.91) * mm});
            skLineSegment(sketch, "E715", {"start": v(0.1, 47.91) * mm, "end": v(-0.15, 47.91) * mm});
            skLineSegment(sketch, "E716", {"start": v(-0.15, 47.91) * mm, "end": v(-0.41, 47.91) * mm});
            skLineSegment(sketch, "E717", {"start": v(-0.41, 47.91) * mm, "end": v(-0.67, 47.9) * mm});
            skLineSegment(sketch, "E718", {"start": v(-0.67, 47.9) * mm, "end": v(-0.93, 47.9) * mm});
            skLineSegment(sketch, "E719", {"start": v(-0.93, 47.9) * mm, "end": v(-1.18, 47.88) * mm});
            skLineSegment(sketch, "E720", {"start": v(-1.18, 47.88) * mm, "end": v(-1.44, 47.86) * mm});
            skLineSegment(sketch, "E721", {"start": v(-1.44, 47.86) * mm, "end": v(-1.7, 47.84) * mm});
            skLineSegment(sketch, "E722", {"start": v(-1.7, 47.84) * mm, "end": v(-1.94, 47.81) * mm});
            skLineSegment(sketch, "E723", {"start": v(-1.94, 47.81) * mm, "end": v(-2.2, 47.78) * mm});
            skLineSegment(sketch, "E724", {"start": v(-2.2, 47.78) * mm, "end": v(-2.45, 47.75) * mm});
            skLineSegment(sketch, "E725", {"start": v(-2.45, 47.75) * mm, "end": v(-2.7, 47.7) * mm});
            skLineSegment(sketch, "E726", {"start": v(-2.7, 47.7) * mm, "end": v(-2.95, 47.66) * mm});
            skLineSegment(sketch, "E727", {"start": v(-2.95, 47.66) * mm, "end": v(-3.2, 47.62) * mm});
            skLineSegment(sketch, "E728", {"start": v(-3.2, 47.62) * mm, "end": v(-3.45, 47.56) * mm});
            skLineSegment(sketch, "E729", {"start": v(-3.45, 47.56) * mm, "end": v(-3.7, 47.5) * mm});
            skLineSegment(sketch, "E730", {"start": v(-3.7, 47.5) * mm, "end": v(-3.94, 47.45) * mm});
            skLineSegment(sketch, "E731", {"start": v(-3.94, 47.45) * mm, "end": v(-4.19, 47.39) * mm});
            skLineSegment(sketch, "E732", {"start": v(-4.19, 47.39) * mm, "end": v(-4.43, 47.32) * mm});
            skLineSegment(sketch, "E733", {"start": v(-4.43, 47.32) * mm, "end": v(-4.67, 47.25) * mm});
            skLineSegment(sketch, "E734", {"start": v(-4.67, 47.25) * mm, "end": v(-4.92, 47.18) * mm});
            skLineSegment(sketch, "E735", {"start": v(-4.92, 47.18) * mm, "end": v(-5.16, 47.1) * mm});
            skLineSegment(sketch, "E736", {"start": v(-5.16, 47.1) * mm, "end": v(-5.4, 47.02) * mm});
            skLineSegment(sketch, "E737", {"start": v(-5.4, 47.02) * mm, "end": v(-5.64, 46.93) * mm});
            skLineSegment(sketch, "E738", {"start": v(-5.64, 46.93) * mm, "end": v(-5.88, 46.84) * mm});
            skLineSegment(sketch, "E739", {"start": v(-5.88, 46.84) * mm, "end": v(-6.12, 46.75) * mm});
            skLineSegment(sketch, "E740", {"start": v(-6.12, 46.75) * mm, "end": v(-6.36, 46.66) * mm});
            skLineSegment(sketch, "E741", {"start": v(-6.36, 46.66) * mm, "end": v(-6.6, 46.56) * mm});
            skLineSegment(sketch, "E742", {"start": v(-6.6, 46.56) * mm, "end": v(-6.83, 46.46) * mm});
            skLineSegment(sketch, "E743", {"start": v(-6.83, 46.46) * mm, "end": v(-7.07, 46.35) * mm});
            skLineSegment(sketch, "E744", {"start": v(-7.07, 46.35) * mm, "end": v(-7.3, 46.25) * mm});
            skLineSegment(sketch, "E745", {"start": v(-7.3, 46.25) * mm, "end": v(-7.5, 46.15) * mm});
            skLineSegment(sketch, "E746", {"start": v(-7.5, 46.15) * mm, "end": v(-7.7, 46.05) * mm});
            skLineSegment(sketch, "E747", {"start": v(-7.7, 46.05) * mm, "end": v(-7.9, 45.95) * mm});
            skLineSegment(sketch, "E748", {"start": v(-7.9, 45.95) * mm, "end": v(-8.09, 45.85) * mm});
            skLineSegment(sketch, "E749", {"start": v(-8.09, 45.85) * mm, "end": v(-8.28, 45.75) * mm});
            skLineSegment(sketch, "E750", {"start": v(-8.28, 45.75) * mm, "end": v(-8.46, 45.64) * mm});
            skLineSegment(sketch, "E751", {"start": v(-8.46, 45.64) * mm, "end": v(-8.65, 45.53) * mm});
            skLineSegment(sketch, "E752", {"start": v(-8.65, 45.53) * mm, "end": v(-8.83, 45.41) * mm});
            skLineSegment(sketch, "E753", {"start": v(-8.83, 45.41) * mm, "end": v(-9.02, 45.3) * mm});
            skLineSegment(sketch, "E754", {"start": v(-9.02, 45.3) * mm, "end": v(-9.2, 45.18) * mm});
            skLineSegment(sketch, "E755", {"start": v(-9.2, 45.18) * mm, "end": v(-9.38, 45.06) * mm});
            skLineSegment(sketch, "E756", {"start": v(-9.38, 45.06) * mm, "end": v(-9.55, 44.93) * mm});
            skLineSegment(sketch, "E757", {"start": v(-9.55, 44.93) * mm, "end": v(-9.73, 44.8) * mm});
            skLineSegment(sketch, "E758", {"start": v(-9.73, 44.8) * mm, "end": v(-9.9, 44.68) * mm});
            skLineSegment(sketch, "E759", {"start": v(-9.9, 44.68) * mm, "end": v(-10.07, 44.54) * mm});
            skLineSegment(sketch, "E760", {"start": v(-10.07, 44.54) * mm, "end": v(-10.24, 44.41) * mm});
            skLineSegment(sketch, "E761", {"start": v(-10.24, 44.41) * mm, "end": v(-10.4, 44.27) * mm});
            skLineSegment(sketch, "E762", {"start": v(-10.4, 44.27) * mm, "end": v(-10.57, 44.14) * mm});
            skLineSegment(sketch, "E763", {"start": v(-10.57, 44.14) * mm, "end": v(-10.74, 44) * mm});
            skLineSegment(sketch, "E764", {"start": v(-10.74, 44) * mm, "end": v(-10.9, 43.85) * mm});
            skLineSegment(sketch, "E765", {"start": v(-10.9, 43.85) * mm, "end": v(-11.06, 43.7) * mm});
            skLineSegment(sketch, "E766", {"start": v(-11.06, 43.7) * mm, "end": v(-11.22, 43.56) * mm});
            skLineSegment(sketch, "E767", {"start": v(-11.22, 43.56) * mm, "end": v(-11.38, 43.4) * mm});
            skLineSegment(sketch, "E768", {"start": v(-11.38, 43.4) * mm, "end": v(-11.53, 43.26) * mm});
            skLineSegment(sketch, "E769", {"start": v(-11.53, 43.26) * mm, "end": v(-11.68, 43.1) * mm});
            skLineSegment(sketch, "E770", {"start": v(-11.68, 43.1) * mm, "end": v(-11.84, 42.95) * mm});
            skLineSegment(sketch, "E771", {"start": v(-11.84, 42.95) * mm, "end": v(-11.99, 42.79) * mm});
            skLineSegment(sketch, "E772", {"start": v(-11.99, 42.79) * mm, "end": v(-12.14, 42.63) * mm});
            skLineSegment(sketch, "E773", {"start": v(-12.14, 42.63) * mm, "end": v(-12.29, 42.47) * mm});
            skLineSegment(sketch, "E774", {"start": v(-12.29, 42.47) * mm, "end": v(-12.43, 42.3) * mm});
            skLineSegment(sketch, "E775", {"start": v(-12.43, 42.3) * mm, "end": v(-12.58, 42.13) * mm});
            skLineSegment(sketch, "E776", {"start": v(-12.58, 42.13) * mm, "end": v(-12.72, 41.97) * mm});
            skLineSegment(sketch, "E777", {"start": v(-12.72, 41.97) * mm, "end": v(-12.85, 41.81) * mm});
            skLineSegment(sketch, "E778", {"start": v(-12.85, 41.81) * mm, "end": v(-12.98, 41.66) * mm});
            skLineSegment(sketch, "E779", {"start": v(-12.98, 41.66) * mm, "end": v(-13.1, 41.5) * mm});
            skLineSegment(sketch, "E780", {"start": v(-13.1, 41.5) * mm, "end": v(-13.22, 41.34) * mm});
            skLineSegment(sketch, "E781", {"start": v(-13.22, 41.34) * mm, "end": v(-13.34, 41.18) * mm});
            skLineSegment(sketch, "E782", {"start": v(-13.34, 41.18) * mm, "end": v(-13.46, 41.02) * mm});
            skLineSegment(sketch, "E783", {"start": v(-13.46, 41.02) * mm, "end": v(-13.58, 40.86) * mm});
            skLineSegment(sketch, "E784", {"start": v(-13.58, 40.86) * mm, "end": v(-13.7, 40.7) * mm});
            skLineSegment(sketch, "E785", {"start": v(-13.7, 40.7) * mm, "end": v(-13.8, 40.54) * mm});
            skLineSegment(sketch, "E786", {"start": v(-13.8, 40.54) * mm, "end": v(-13.92, 40.38) * mm});
            skLineSegment(sketch, "E787", {"start": v(-13.92, 40.38) * mm, "end": v(-14.03, 40.21) * mm});
            skLineSegment(sketch, "E788", {"start": v(-14.03, 40.21) * mm, "end": v(-14.13, 40.05) * mm});
            skLineSegment(sketch, "E789", {"start": v(-14.13, 40.05) * mm, "end": v(-14.24, 39.88) * mm});
            skLineSegment(sketch, "E790", {"start": v(-14.24, 39.88) * mm, "end": v(-14.34, 39.71) * mm});
            skLineSegment(sketch, "E791", {"start": v(-14.34, 39.71) * mm, "end": v(-14.44, 39.54) * mm});
            skLineSegment(sketch, "E792", {"start": v(-14.44, 39.54) * mm, "end": v(-14.53, 39.37) * mm});
            skLineSegment(sketch, "E793", {"start": v(-14.53, 39.37) * mm, "end": v(-14.63, 39.2) * mm});
            skLineSegment(sketch, "E794", {"start": v(-14.63, 39.2) * mm, "end": v(-14.72, 39.03) * mm});
            skLineSegment(sketch, "E795", {"start": v(-14.72, 39.03) * mm, "end": v(-14.81, 38.85) * mm});
            skLineSegment(sketch, "E796", {"start": v(-14.81, 38.85) * mm, "end": v(-14.9, 38.68) * mm});
            skLineSegment(sketch, "E797", {"start": v(-14.9, 38.68) * mm, "end": v(-14.99, 38.5) * mm});
            skLineSegment(sketch, "E798", {"start": v(-14.99, 38.5) * mm, "end": v(-15.07, 38.32) * mm});
            skLineSegment(sketch, "E799", {"start": v(-15.07, 38.32) * mm, "end": v(-15.16, 38.15) * mm});
            skLineSegment(sketch, "E800", {"start": v(-15.16, 38.15) * mm, "end": v(-15.23, 37.97) * mm});
            skLineSegment(sketch, "E801", {"start": v(-15.23, 37.97) * mm, "end": v(-15.31, 37.78) * mm});
            skLineSegment(sketch, "E802", {"start": v(-15.31, 37.78) * mm, "end": v(-15.39, 37.6) * mm});
            skLineSegment(sketch, "E803", {"start": v(-15.39, 37.6) * mm, "end": v(-15.46, 37.42) * mm});
            skLineSegment(sketch, "E804", {"start": v(-15.46, 37.42) * mm, "end": v(-15.53, 37.23) * mm});
            skLineSegment(sketch, "E805", {"start": v(-15.53, 37.23) * mm, "end": v(-15.6, 37.05) * mm});
            skLineSegment(sketch, "E806", {"start": v(-15.6, 37.05) * mm, "end": v(-15.66, 36.86) * mm});
            skLineSegment(sketch, "E807", {"start": v(-15.66, 36.86) * mm, "end": v(-15.73, 36.67) * mm});
            skLineSegment(sketch, "E808", {"start": v(-15.73, 36.67) * mm, "end": v(-15.79, 36.48) * mm});
            skLineSegment(sketch, "E809", {"start": v(-15.79, 36.48) * mm, "end": v(-15.81, 36.4) * mm});
            skLineSegment(sketch, "E810", {"start": v(-15.81, 36.4) * mm, "end": v(-15.83, 36.32) * mm});
            skLineSegment(sketch, "E811", {"start": v(-15.83, 36.32) * mm, "end": v(-15.86, 36.24) * mm});
            skLineSegment(sketch, "E812", {"start": v(-15.86, 36.24) * mm, "end": v(-15.88, 36.16) * mm});
            skLineSegment(sketch, "E813", {"start": v(-15.88, 36.16) * mm, "end": v(-15.9, 36.09) * mm});
            skLineSegment(sketch, "E814", {"start": v(-15.9, 36.09) * mm, "end": v(-15.92, 36) * mm});
            skLineSegment(sketch, "E815", {"start": v(-15.92, 36) * mm, "end": v(-15.94, 35.93) * mm});
            skLineSegment(sketch, "E816", {"start": v(-15.94, 35.93) * mm, "end": v(-15.96, 35.85) * mm});
            skLineSegment(sketch, "E817", {"start": v(-15.96, 35.85) * mm, "end": v(-15.98, 35.77) * mm});
            skLineSegment(sketch, "E818", {"start": v(-15.98, 35.77) * mm, "end": v(-16, 35.69) * mm});
            skLineSegment(sketch, "E819", {"start": v(-16, 35.69) * mm, "end": v(-16.02, 35.6) * mm});
            skLineSegment(sketch, "E820", {"start": v(-16.02, 35.6) * mm, "end": v(-16.04, 35.53) * mm});
            skLineSegment(sketch, "E821", {"start": v(-16.04, 35.53) * mm, "end": v(-16.06, 35.45) * mm});
            skLineSegment(sketch, "E822", {"start": v(-16.06, 35.45) * mm, "end": v(-16.08, 35.37) * mm});
            skLineSegment(sketch, "E823", {"start": v(-16.08, 35.37) * mm, "end": v(-16.1, 35.29) * mm});
            skLineSegment(sketch, "E824", {"start": v(-16.1, 35.29) * mm, "end": v(-16.11, 35.2) * mm});
            skLineSegment(sketch, "E825", {"start": v(-16.11, 35.2) * mm, "end": v(-16.13, 35.13) * mm});
            skLineSegment(sketch, "E826", {"start": v(-16.13, 35.13) * mm, "end": v(-16.14, 35.05) * mm});
            skLineSegment(sketch, "E827", {"start": v(-16.14, 35.05) * mm, "end": v(-16.16, 34.97) * mm});
            skLineSegment(sketch, "E828", {"start": v(-16.16, 34.97) * mm, "end": v(-16.18, 34.89) * mm});
            skLineSegment(sketch, "E829", {"start": v(-16.18, 34.89) * mm, "end": v(-16.2, 34.8) * mm});
            skLineSegment(sketch, "E830", {"start": v(-16.2, 34.8) * mm, "end": v(-16.21, 34.73) * mm});
            skLineSegment(sketch, "E831", {"start": v(-16.21, 34.73) * mm, "end": v(-16.23, 34.65) * mm});
            skLineSegment(sketch, "E832", {"start": v(-16.23, 34.65) * mm, "end": v(-16.25, 34.57) * mm});
            skLineSegment(sketch, "E833", {"start": v(-16.25, 34.57) * mm, "end": v(-16.26, 34.48) * mm});
            skLineSegment(sketch, "E834", {"start": v(-16.26, 34.48) * mm, "end": v(-16.28, 34.4) * mm});
            skLineSegment(sketch, "E835", {"start": v(-16.28, 34.4) * mm, "end": v(-16.3, 34.32) * mm});
            skLineSegment(sketch, "E836", {"start": v(-16.3, 34.32) * mm, "end": v(-16.31, 34.24) * mm});
            skLineSegment(sketch, "E837", {"start": v(-16.31, 34.24) * mm, "end": v(-16.33, 34.16) * mm});
            skLineSegment(sketch, "E838", {"start": v(-16.33, 34.16) * mm, "end": v(-16.35, 34.08) * mm});
            skLineSegment(sketch, "E839", {"start": v(-16.35, 34.08) * mm, "end": v(-16.37, 34) * mm});
            skLineSegment(sketch, "E840", {"start": v(-16.37, 34) * mm, "end": v(-16.38, 33.92) * mm});
            skLineSegment(sketch, "E841", {"start": v(-16.38, 33.92) * mm, "end": v(-16.38, 33.92) * mm});
            skLineSegment(sketch, "E842", {"start": v(-16.38, 33.92) * mm, "end": v(-16.37, 33.92) * mm});
            skLineSegment(sketch, "E843", {"start": v(-16.37, 33.92) * mm, "end": v(-16.37, 33.92) * mm});
            skLineSegment(sketch, "E844", {"start": v(-16.37, 33.92) * mm, "end": v(-16.36, 33.92) * mm});
            skLineSegment(sketch, "E845", {"start": v(-16.36, 33.92) * mm, "end": v(-16.36, 33.92) * mm});
            skLineSegment(sketch, "E846", {"start": v(-16.36, 33.92) * mm, "end": v(-16.35, 33.92) * mm});
            skLineSegment(sketch, "E847", {"start": v(-16.35, 33.92) * mm, "end": v(-16.35, 33.91) * mm});
            skLineSegment(sketch, "E848", {"start": v(-16.35, 33.91) * mm, "end": v(-16.34, 33.91) * mm});
            skLineSegment(sketch, "E849", {"start": v(-16.34, 33.91) * mm, "end": v(-16.34, 33.91) * mm});
            skLineSegment(sketch, "E850", {"start": v(-16.34, 33.91) * mm, "end": v(-16.33, 33.9) * mm});
            skLineSegment(sketch, "E851", {"start": v(-16.33, 33.9) * mm, "end": v(-16.32, 33.9) * mm});
            skLineSegment(sketch, "E852", {"start": v(-16.32, 33.9) * mm, "end": v(-16.32, 33.9) * mm});
            skLineSegment(sketch, "E853", {"start": v(-16.32, 33.9) * mm, "end": v(-16.31, 33.9) * mm});
            skLineSegment(sketch, "E854", {"start": v(-16.31, 33.9) * mm, "end": v(-16.3, 33.9) * mm});
            skLineSegment(sketch, "E855", {"start": v(-16.3, 33.9) * mm, "end": v(-16.3, 33.9) * mm});
            skLineSegment(sketch, "E856", {"start": v(-16.3, 33.9) * mm, "end": v(-16.29, 33.9) * mm});
            skLineSegment(sketch, "E857", {"start": v(-16.29, 33.9) * mm, "end": v(-16.28, 33.9) * mm});
            skLineSegment(sketch, "E858", {"start": v(-16.28, 33.9) * mm, "end": v(-16.28, 33.9) * mm});
            skLineSegment(sketch, "E859", {"start": v(-16.28, 33.9) * mm, "end": v(-16.27, 33.9) * mm});
            skLineSegment(sketch, "E860", {"start": v(-16.27, 33.9) * mm, "end": v(-16.27, 33.9) * mm});
            skLineSegment(sketch, "E861", {"start": v(-16.27, 33.9) * mm, "end": v(-16.26, 33.9) * mm});
            skLineSegment(sketch, "E862", {"start": v(-16.26, 33.9) * mm, "end": v(-16.25, 33.9) * mm});
            skLineSegment(sketch, "E863", {"start": v(-16.25, 33.9) * mm, "end": v(-16.25, 33.9) * mm});
            skLineSegment(sketch, "E864", {"start": v(-16.25, 33.9) * mm, "end": v(-16.24, 33.89) * mm});
            skLineSegment(sketch, "E865", {"start": v(-16.24, 33.89) * mm, "end": v(-16.24, 33.89) * mm});
            skLineSegment(sketch, "E866", {"start": v(-16.24, 33.89) * mm, "end": v(-16.23, 33.89) * mm});
            skLineSegment(sketch, "E867", {"start": v(-16.23, 33.89) * mm, "end": v(-16.23, 33.89) * mm});
            skLineSegment(sketch, "E868", {"start": v(-16.23, 33.89) * mm, "end": v(-16.22, 33.88) * mm});
            skLineSegment(sketch, "E869", {"start": v(-16.22, 33.88) * mm, "end": v(-16.22, 33.88) * mm});
            skLineSegment(sketch, "E870", {"start": v(-16.22, 33.88) * mm, "end": v(-16.21, 33.88) * mm});
            skLineSegment(sketch, "E871", {"start": v(-16.21, 33.88) * mm, "end": v(-16.16, 34.01) * mm});
            skLineSegment(sketch, "E872", {"start": v(-16.16, 34.01) * mm, "end": v(-16.1, 34.14) * mm});
            skLineSegment(sketch, "E873", {"start": v(-16.1, 34.14) * mm, "end": v(-16.05, 34.26) * mm});
            skLineSegment(sketch, "E874", {"start": v(-16.05, 34.26) * mm, "end": v(-16, 34.39) * mm});
            skLineSegment(sketch, "E875", {"start": v(-16, 34.39) * mm, "end": v(-15.93, 34.51) * mm});
            skLineSegment(sketch, "E876", {"start": v(-15.93, 34.51) * mm, "end": v(-15.87, 34.63) * mm});
            skLineSegment(sketch, "E877", {"start": v(-15.87, 34.63) * mm, "end": v(-15.8, 34.75) * mm});
            skLineSegment(sketch, "E878", {"start": v(-15.8, 34.75) * mm, "end": v(-15.73, 34.87) * mm});
            skLineSegment(sketch, "E879", {"start": v(-15.73, 34.87) * mm, "end": v(-15.66, 34.98) * mm});
            skLineSegment(sketch, "E880", {"start": v(-15.66, 34.98) * mm, "end": v(-15.59, 35.1) * mm});
            skLineSegment(sketch, "E881", {"start": v(-15.59, 35.1) * mm, "end": v(-15.51, 35.2) * mm});
            skLineSegment(sketch, "E882", {"start": v(-15.51, 35.2) * mm, "end": v(-15.44, 35.32) * mm});
            skLineSegment(sketch, "E883", {"start": v(-15.44, 35.32) * mm, "end": v(-15.36, 35.42) * mm});
            skLineSegment(sketch, "E884", {"start": v(-15.36, 35.42) * mm, "end": v(-15.28, 35.53) * mm});
            skLineSegment(sketch, "E885", {"start": v(-15.28, 35.53) * mm, "end": v(-15.2, 35.63) * mm});
            skLineSegment(sketch, "E886", {"start": v(-15.2, 35.63) * mm, "end": v(-15.1, 35.74) * mm});
            skLineSegment(sketch, "E887", {"start": v(-15.1, 35.74) * mm, "end": v(-15.02, 35.84) * mm});
            skLineSegment(sketch, "E888", {"start": v(-15.02, 35.84) * mm, "end": v(-14.93, 35.94) * mm});
            skLineSegment(sketch, "E889", {"start": v(-14.93, 35.94) * mm, "end": v(-14.84, 36.04) * mm});
            skLineSegment(sketch, "E890", {"start": v(-14.84, 36.04) * mm, "end": v(-14.75, 36.13) * mm});
            skLineSegment(sketch, "E891", {"start": v(-14.75, 36.13) * mm, "end": v(-14.66, 36.23) * mm});
            skLineSegment(sketch, "E892", {"start": v(-14.66, 36.23) * mm, "end": v(-14.56, 36.32) * mm});
            skLineSegment(sketch, "E893", {"start": v(-14.56, 36.32) * mm, "end": v(-14.47, 36.42) * mm});
            skLineSegment(sketch, "E894", {"start": v(-14.47, 36.42) * mm, "end": v(-14.37, 36.5) * mm});
            skLineSegment(sketch, "E895", {"start": v(-14.37, 36.5) * mm, "end": v(-14.27, 36.6) * mm});
            skLineSegment(sketch, "E896", {"start": v(-14.27, 36.6) * mm, "end": v(-14.17, 36.69) * mm});
            skLineSegment(sketch, "E897", {"start": v(-14.17, 36.69) * mm, "end": v(-14.07, 36.77) * mm});
            skLineSegment(sketch, "E898", {"start": v(-14.07, 36.77) * mm, "end": v(-13.96, 36.86) * mm});
            skLineSegment(sketch, "E899", {"start": v(-13.96, 36.86) * mm, "end": v(-13.86, 36.94) * mm});
            skLineSegment(sketch, "E900", {"start": v(-13.86, 36.94) * mm, "end": v(-13.75, 37.03) * mm});
            skLineSegment(sketch, "E901", {"start": v(-13.75, 37.03) * mm, "end": v(-13.64, 37.1) * mm});
            skLineSegment(sketch, "E902", {"start": v(-13.64, 37.1) * mm, "end": v(-13.54, 37.19) * mm});
            skLineSegment(sketch, "E903", {"start": v(-13.54, 37.19) * mm, "end": v(-13.4, 37.3) * mm});
            skLineSegment(sketch, "E904", {"start": v(-13.4, 37.3) * mm, "end": v(-13.25, 37.4) * mm});
            skLineSegment(sketch, "E905", {"start": v(-13.25, 37.4) * mm, "end": v(-13.11, 37.49) * mm});
            skLineSegment(sketch, "E906", {"start": v(-13.11, 37.49) * mm, "end": v(-12.97, 37.59) * mm});
            skLineSegment(sketch, "E907", {"start": v(-12.97, 37.59) * mm, "end": v(-12.83, 37.68) * mm});
            skLineSegment(sketch, "E908", {"start": v(-12.83, 37.68) * mm, "end": v(-12.68, 37.78) * mm});
            skLineSegment(sketch, "E909", {"start": v(-12.68, 37.78) * mm, "end": v(-12.54, 37.87) * mm});
            skLineSegment(sketch, "E910", {"start": v(-12.54, 37.87) * mm, "end": v(-12.39, 37.96) * mm});
            skLineSegment(sketch, "E911", {"start": v(-12.39, 37.96) * mm, "end": v(-12.24, 38.05) * mm});
            skLineSegment(sketch, "E912", {"start": v(-12.24, 38.05) * mm, "end": v(-12.1, 38.14) * mm});
            skLineSegment(sketch, "E913", {"start": v(-12.1, 38.14) * mm, "end": v(-11.94, 38.22) * mm});
            skLineSegment(sketch, "E914", {"start": v(-11.94, 38.22) * mm, "end": v(-11.8, 38.3) * mm});
            skLineSegment(sketch, "E915", {"start": v(-11.8, 38.3) * mm, "end": v(-11.64, 38.39) * mm});
            skLineSegment(sketch, "E916", {"start": v(-11.64, 38.39) * mm, "end": v(-11.5, 38.47) * mm});
            skLineSegment(sketch, "E917", {"start": v(-11.5, 38.47) * mm, "end": v(-11.34, 38.55) * mm});
            skLineSegment(sketch, "E918", {"start": v(-11.34, 38.55) * mm, "end": v(-11.19, 38.63) * mm});
            skLineSegment(sketch, "E919", {"start": v(-11.19, 38.63) * mm, "end": v(-11.03, 38.7) * mm});
            skLineSegment(sketch, "E920", {"start": v(-11.03, 38.7) * mm, "end": v(-10.88, 38.78) * mm});
            skLineSegment(sketch, "E921", {"start": v(-10.88, 38.78) * mm, "end": v(-10.72, 38.85) * mm});
            skLineSegment(sketch, "E922", {"start": v(-10.72, 38.85) * mm, "end": v(-10.57, 38.93) * mm});
            skLineSegment(sketch, "E923", {"start": v(-10.57, 38.93) * mm, "end": v(-10.4, 39) * mm});
            skLineSegment(sketch, "E924", {"start": v(-10.4, 39) * mm, "end": v(-10.25, 39.07) * mm});
            skLineSegment(sketch, "E925", {"start": v(-10.25, 39.07) * mm, "end": v(-10.1, 39.13) * mm});
            skLineSegment(sketch, "E926", {"start": v(-10.1, 39.13) * mm, "end": v(-9.93, 39.2) * mm});
            skLineSegment(sketch, "E927", {"start": v(-9.93, 39.2) * mm, "end": v(-9.77, 39.27) * mm});
            skLineSegment(sketch, "E928", {"start": v(-9.77, 39.27) * mm, "end": v(-9.6, 39.33) * mm});
            skLineSegment(sketch, "E929", {"start": v(-9.6, 39.33) * mm, "end": v(-9.45, 39.4) * mm});
            skLineSegment(sketch, "E930", {"start": v(-9.45, 39.4) * mm, "end": v(-9.28, 39.45) * mm});
            skLineSegment(sketch, "E931", {"start": v(-9.28, 39.45) * mm, "end": v(-9.12, 39.51) * mm});
            skLineSegment(sketch, "E932", {"start": v(-9.12, 39.51) * mm, "end": v(-8.95, 39.57) * mm});
            skLineSegment(sketch, "E933", {"start": v(-8.95, 39.57) * mm, "end": v(-8.79, 39.62) * mm});
            skLineSegment(sketch, "E934", {"start": v(-8.79, 39.62) * mm, "end": v(-8.62, 39.68) * mm});
            skLineSegment(sketch, "E935", {"start": v(-8.62, 39.68) * mm, "end": v(-8.39, 39.75) * mm});
            skLineSegment(sketch, "E936", {"start": v(-8.39, 39.75) * mm, "end": v(-8.16, 39.82) * mm});
            skLineSegment(sketch, "E937", {"start": v(-8.16, 39.82) * mm, "end": v(-7.93, 39.9) * mm});
            skLineSegment(sketch, "E938", {"start": v(-7.93, 39.9) * mm, "end": v(-7.7, 39.96) * mm});
            skLineSegment(sketch, "E939", {"start": v(-7.7, 39.96) * mm, "end": v(-7.47, 40.03) * mm});
            skLineSegment(sketch, "E940", {"start": v(-7.47, 40.03) * mm, "end": v(-7.24, 40.1) * mm});
            skLineSegment(sketch, "E941", {"start": v(-7.24, 40.1) * mm, "end": v(-7, 40.15) * mm});
            skLineSegment(sketch, "E942", {"start": v(-7, 40.15) * mm, "end": v(-6.77, 40.21) * mm});
            skLineSegment(sketch, "E943", {"start": v(-6.77, 40.21) * mm, "end": v(-6.54, 40.27) * mm});
            skLineSegment(sketch, "E944", {"start": v(-6.54, 40.27) * mm, "end": v(-6.31, 40.33) * mm});
            skLineSegment(sketch, "E945", {"start": v(-6.31, 40.33) * mm, "end": v(-6.08, 40.38) * mm});
            skLineSegment(sketch, "E946", {"start": v(-6.08, 40.38) * mm, "end": v(-5.85, 40.43) * mm});
            skLineSegment(sketch, "E947", {"start": v(-5.85, 40.43) * mm, "end": v(-5.61, 40.48) * mm});
            skLineSegment(sketch, "E948", {"start": v(-5.61, 40.48) * mm, "end": v(-5.38, 40.53) * mm});
            skLineSegment(sketch, "E949", {"start": v(-5.38, 40.53) * mm, "end": v(-5.15, 40.57) * mm});
            skLineSegment(sketch, "E950", {"start": v(-5.15, 40.57) * mm, "end": v(-4.91, 40.62) * mm});
            skLineSegment(sketch, "E951", {"start": v(-4.91, 40.62) * mm, "end": v(-4.68, 40.66) * mm});
            skLineSegment(sketch, "E952", {"start": v(-4.68, 40.66) * mm, "end": v(-4.44, 40.7) * mm});
            skLineSegment(sketch, "E953", {"start": v(-4.44, 40.7) * mm, "end": v(-4.2, 40.73) * mm});
            skLineSegment(sketch, "E954", {"start": v(-4.2, 40.73) * mm, "end": v(-3.97, 40.76) * mm});
            skLineSegment(sketch, "E955", {"start": v(-3.97, 40.76) * mm, "end": v(-3.74, 40.8) * mm});
            skLineSegment(sketch, "E956", {"start": v(-3.74, 40.8) * mm, "end": v(-3.5, 40.82) * mm});
            skLineSegment(sketch, "E957", {"start": v(-3.5, 40.82) * mm, "end": v(-3.26, 40.84) * mm});
            skLineSegment(sketch, "E958", {"start": v(-3.26, 40.84) * mm, "end": v(-3.02, 40.87) * mm});
            skLineSegment(sketch, "E959", {"start": v(-3.02, 40.87) * mm, "end": v(-2.79, 40.89) * mm});
            skLineSegment(sketch, "E960", {"start": v(-2.79, 40.89) * mm, "end": v(-2.55, 40.9) * mm});
            skLineSegment(sketch, "E961", {"start": v(-2.55, 40.9) * mm, "end": v(-2.31, 40.92) * mm});
            skLineSegment(sketch, "E962", {"start": v(-2.31, 40.92) * mm, "end": v(-2.07, 40.93) * mm});
            skLineSegment(sketch, "E963", {"start": v(-2.07, 40.93) * mm, "end": v(-1.83, 40.94) * mm});
            skLineSegment(sketch, "E964", {"start": v(-1.83, 40.94) * mm, "end": v(-1.6, 40.94) * mm});
            skLineSegment(sketch, "E965", {"start": v(-1.6, 40.94) * mm, "end": v(-1.35, 40.94) * mm});
            skLineSegment(sketch, "E966", {"start": v(-1.35, 40.94) * mm, "end": v(-1.1, 40.94) * mm});
            skLineSegment(sketch, "E967", {"start": v(-1.1, 40.94) * mm, "end": v(-1.04, 40.94) * mm});
            skLineSegment(sketch, "E968", {"start": v(-1.04, 40.94) * mm, "end": v(-0.97, 40.94) * mm});
            skLineSegment(sketch, "E969", {"start": v(-0.97, 40.94) * mm, "end": v(-0.9, 40.94) * mm});
            skLineSegment(sketch, "E970", {"start": v(-0.9, 40.94) * mm, "end": v(-0.84, 40.94) * mm});
            skLineSegment(sketch, "E971", {"start": v(-0.84, 40.94) * mm, "end": v(-0.77, 40.94) * mm});
            skLineSegment(sketch, "E972", {"start": v(-0.77, 40.94) * mm, "end": v(-0.7, 40.93) * mm});
            skLineSegment(sketch, "E973", {"start": v(-0.7, 40.93) * mm, "end": v(-0.63, 40.93) * mm});
            skLineSegment(sketch, "E974", {"start": v(-0.63, 40.93) * mm, "end": v(-0.56, 40.93) * mm});
            skLineSegment(sketch, "E975", {"start": v(-0.56, 40.93) * mm, "end": v(-0.5, 40.92) * mm});
            skLineSegment(sketch, "E976", {"start": v(-0.5, 40.92) * mm, "end": v(-0.43, 40.92) * mm});
            skLineSegment(sketch, "E977", {"start": v(-0.43, 40.92) * mm, "end": v(-0.36, 40.91) * mm});
            skLineSegment(sketch, "E978", {"start": v(-0.36, 40.91) * mm, "end": v(-0.29, 40.9) * mm});
            skLineSegment(sketch, "E979", {"start": v(-0.29, 40.9) * mm, "end": v(-0.22, 40.9) * mm});
            skLineSegment(sketch, "E980", {"start": v(-0.22, 40.9) * mm, "end": v(-0.15, 40.9) * mm});
            skLineSegment(sketch, "E981", {"start": v(-0.15, 40.9) * mm, "end": v(-0.08, 40.9) * mm});
            skLineSegment(sketch, "E982", {"start": v(-0.08, 40.9) * mm, "end": v(0, 40.89) * mm});
            skLineSegment(sketch, "E983", {"start": v(0, 40.89) * mm, "end": v(0.07, 40.88) * mm});
            skLineSegment(sketch, "E984", {"start": v(0.07, 40.88) * mm, "end": v(0.14, 40.88) * mm});
            skLineSegment(sketch, "E985", {"start": v(0.14, 40.88) * mm, "end": v(0.21, 40.87) * mm});
            skLineSegment(sketch, "E986", {"start": v(0.21, 40.87) * mm, "end": v(0.29, 40.87) * mm});
            skLineSegment(sketch, "E987", {"start": v(0.29, 40.87) * mm, "end": v(0.36, 40.86) * mm});
            skLineSegment(sketch, "E988", {"start": v(0.36, 40.86) * mm, "end": v(0.43, 40.85) * mm});
            skLineSegment(sketch, "E989", {"start": v(0.43, 40.85) * mm, "end": v(0.5, 40.85) * mm});
            skLineSegment(sketch, "E990", {"start": v(0.5, 40.85) * mm, "end": v(0.59, 40.84) * mm});
            skLineSegment(sketch, "E991", {"start": v(0.59, 40.84) * mm, "end": v(0.66, 40.84) * mm});
            skLineSegment(sketch, "E992", {"start": v(0.66, 40.84) * mm, "end": v(0.74, 40.83) * mm});
            skLineSegment(sketch, "E993", {"start": v(0.74, 40.83) * mm, "end": v(0.82, 40.82) * mm});
            skLineSegment(sketch, "E994", {"start": v(0.82, 40.82) * mm, "end": v(0.9, 40.82) * mm});
            skLineSegment(sketch, "E995", {"start": v(0.9, 40.82) * mm, "end": v(0.98, 40.81) * mm});
            skLineSegment(sketch, "E996", {"start": v(0.98, 40.81) * mm, "end": v(1.06, 40.8) * mm});
            skLineSegment(sketch, "E997", {"start": v(1.06, 40.8) * mm, "end": v(1.14, 40.8) * mm});
            skLineSegment(sketch, "E998", {"start": v(1.14, 40.8) * mm, "end": v(1.22, 40.8) * mm});
            skLineSegment(sketch, "E999", {"start": v(-0.24, 23.31) * mm, "end": v(-0.2, 23.32) * mm});
            skLineSegment(sketch, "E1000", {"start": v(-0.2, 23.32) * mm, "end": v(-0.15, 23.33) * mm});
            skLineSegment(sketch, "E1001", {"start": v(-0.15, 23.33) * mm, "end": v(-0.11, 23.33) * mm});
            skLineSegment(sketch, "E1002", {"start": v(-0.11, 23.33) * mm, "end": v(-0.07, 23.34) * mm});
            skLineSegment(sketch, "E1003", {"start": v(-0.07, 23.34) * mm, "end": v(-0.03, 23.34) * mm});
            skLineSegment(sketch, "E1004", {"start": v(-0.03, 23.34) * mm, "end": v(0, 23.35) * mm});
            skLineSegment(sketch, "E1005", {"start": v(0, 23.35) * mm, "end": v(0.04, 23.36) * mm});
            skLineSegment(sketch, "E1006", {"start": v(0.04, 23.36) * mm, "end": v(0.08, 23.36) * mm});
            skLineSegment(sketch, "E1007", {"start": v(0.08, 23.36) * mm, "end": v(0.12, 23.37) * mm});
            skLineSegment(sketch, "E1008", {"start": v(0.12, 23.37) * mm, "end": v(0.15, 23.38) * mm});
            skLineSegment(sketch, "E1009", {"start": v(0.15, 23.38) * mm, "end": v(0.19, 23.38) * mm});
            skLineSegment(sketch, "E1010", {"start": v(0.19, 23.38) * mm, "end": v(0.22, 23.39) * mm});
            skLineSegment(sketch, "E1011", {"start": v(0.22, 23.39) * mm, "end": v(0.26, 23.4) * mm});
            skLineSegment(sketch, "E1012", {"start": v(0.26, 23.4) * mm, "end": v(0.3, 23.4) * mm});
            skLineSegment(sketch, "E1013", {"start": v(0.3, 23.4) * mm, "end": v(0.33, 23.4) * mm});
            skLineSegment(sketch, "E1014", {"start": v(0.33, 23.4) * mm, "end": v(0.36, 23.41) * mm});
            skLineSegment(sketch, "E1015", {"start": v(0.36, 23.41) * mm, "end": v(0.4, 23.42) * mm});
            skLineSegment(sketch, "E1016", {"start": v(0.4, 23.42) * mm, "end": v(0.43, 23.42) * mm});
            skLineSegment(sketch, "E1017", {"start": v(0.43, 23.42) * mm, "end": v(0.46, 23.43) * mm});
            skLineSegment(sketch, "E1018", {"start": v(0.46, 23.43) * mm, "end": v(0.5, 23.43) * mm});
            skLineSegment(sketch, "E1019", {"start": v(0.5, 23.43) * mm, "end": v(0.53, 23.44) * mm});
            skLineSegment(sketch, "E1020", {"start": v(0.53, 23.44) * mm, "end": v(0.56, 23.44) * mm});
            skLineSegment(sketch, "E1021", {"start": v(0.56, 23.44) * mm, "end": v(0.6, 23.45) * mm});
            skLineSegment(sketch, "E1022", {"start": v(0.6, 23.45) * mm, "end": v(0.62, 23.45) * mm});
            skLineSegment(sketch, "E1023", {"start": v(0.62, 23.45) * mm, "end": v(0.66, 23.46) * mm});
            skLineSegment(sketch, "E1024", {"start": v(0.66, 23.46) * mm, "end": v(0.69, 23.46) * mm});
            skLineSegment(sketch, "E1025", {"start": v(0.69, 23.46) * mm, "end": v(0.72, 23.46) * mm});
            skLineSegment(sketch, "E1026", {"start": v(0.72, 23.46) * mm, "end": v(0.75, 23.47) * mm});
            skLineSegment(sketch, "E1027", {"start": v(0.75, 23.47) * mm, "end": v(0.78, 23.47) * mm});
            skLineSegment(sketch, "E1028", {"start": v(0.78, 23.47) * mm, "end": v(0.81, 23.48) * mm});
            skLineSegment(sketch, "E1029", {"start": v(0.81, 23.48) * mm, "end": v(0.85, 23.48) * mm});
            skLineSegment(sketch, "E1030", {"start": v(0.85, 23.48) * mm, "end": v(0.88, 23.48) * mm});
            skLineSegment(sketch, "E1031", {"start": v(0.88, 23.48) * mm, "end": v(1.07, 23.5) * mm});
            skLineSegment(sketch, "E1032", {"start": v(1.07, 23.5) * mm, "end": v(1.25, 23.53) * mm});
            skLineSegment(sketch, "E1033", {"start": v(1.25, 23.53) * mm, "end": v(1.44, 23.55) * mm});
            skLineSegment(sketch, "E1034", {"start": v(1.44, 23.55) * mm, "end": v(1.62, 23.59) * mm});
            skLineSegment(sketch, "E1035", {"start": v(1.62, 23.59) * mm, "end": v(1.8, 23.62) * mm});
            skLineSegment(sketch, "E1036", {"start": v(1.8, 23.62) * mm, "end": v(1.98, 23.66) * mm});
            skLineSegment(sketch, "E1037", {"start": v(1.98, 23.66) * mm, "end": v(2.15, 23.7) * mm});
            skLineSegment(sketch, "E1038", {"start": v(2.15, 23.7) * mm, "end": v(2.33, 23.76) * mm});
            skLineSegment(sketch, "E1039", {"start": v(2.33, 23.76) * mm, "end": v(2.5, 23.8) * mm});
            skLineSegment(sketch, "E1040", {"start": v(2.5, 23.8) * mm, "end": v(2.67, 23.87) * mm});
            skLineSegment(sketch, "E1041", {"start": v(2.67, 23.87) * mm, "end": v(2.83, 23.93) * mm});
            skLineSegment(sketch, "E1042", {"start": v(2.83, 23.93) * mm, "end": v(3, 24) * mm});
            skLineSegment(sketch, "E1043", {"start": v(3, 24) * mm, "end": v(3.16, 24.06) * mm});
            skLineSegment(sketch, "E1044", {"start": v(3.16, 24.06) * mm, "end": v(3.32, 24.13) * mm});
            skLineSegment(sketch, "E1045", {"start": v(3.32, 24.13) * mm, "end": v(3.48, 24.21) * mm});
            skLineSegment(sketch, "E1046", {"start": v(3.48, 24.21) * mm, "end": v(3.64, 24.3) * mm});
            skLineSegment(sketch, "E1047", {"start": v(3.64, 24.3) * mm, "end": v(3.8, 24.38) * mm});
            skLineSegment(sketch, "E1048", {"start": v(3.8, 24.38) * mm, "end": v(3.94, 24.47) * mm});
            skLineSegment(sketch, "E1049", {"start": v(3.94, 24.47) * mm, "end": v(4.1, 24.56) * mm});
            skLineSegment(sketch, "E1050", {"start": v(4.1, 24.56) * mm, "end": v(4.24, 24.66) * mm});
            skLineSegment(sketch, "E1051", {"start": v(4.24, 24.66) * mm, "end": v(4.39, 24.76) * mm});
            skLineSegment(sketch, "E1052", {"start": v(4.39, 24.76) * mm, "end": v(4.53, 24.86) * mm});
            skLineSegment(sketch, "E1053", {"start": v(4.53, 24.86) * mm, "end": v(4.67, 24.97) * mm});
            skLineSegment(sketch, "E1054", {"start": v(4.67, 24.97) * mm, "end": v(4.81, 25.08) * mm});
            skLineSegment(sketch, "E1055", {"start": v(4.81, 25.08) * mm, "end": v(4.95, 25.2) * mm});
            skLineSegment(sketch, "E1056", {"start": v(4.95, 25.2) * mm, "end": v(5.09, 25.32) * mm});
            skLineSegment(sketch, "E1057", {"start": v(5.09, 25.32) * mm, "end": v(5.22, 25.44) * mm});
            skLineSegment(sketch, "E1058", {"start": v(5.22, 25.44) * mm, "end": v(5.36, 25.57) * mm});
            skLineSegment(sketch, "E1059", {"start": v(5.36, 25.57) * mm, "end": v(5.49, 25.7) * mm});
            skLineSegment(sketch, "E1060", {"start": v(5.49, 25.7) * mm, "end": v(5.61, 25.84) * mm});
            skLineSegment(sketch, "E1061", {"start": v(5.61, 25.84) * mm, "end": v(5.74, 25.97) * mm});
            skLineSegment(sketch, "E1062", {"start": v(5.74, 25.97) * mm, "end": v(5.87, 26.12) * mm});
            skLineSegment(sketch, "E1063", {"start": v(5.87, 26.12) * mm, "end": v(6, 26.28) * mm});
            skLineSegment(sketch, "E1064", {"start": v(6, 26.28) * mm, "end": v(6.14, 26.45) * mm});
            skLineSegment(sketch, "E1065", {"start": v(6.14, 26.45) * mm, "end": v(6.27, 26.62) * mm});
            skLineSegment(sketch, "E1066", {"start": v(6.27, 26.62) * mm, "end": v(6.4, 26.79) * mm});
            skLineSegment(sketch, "E1067", {"start": v(6.4, 26.79) * mm, "end": v(6.52, 26.96) * mm});
            skLineSegment(sketch, "E1068", {"start": v(6.52, 26.96) * mm, "end": v(6.64, 27.13) * mm});
            skLineSegment(sketch, "E1069", {"start": v(6.64, 27.13) * mm, "end": v(6.75, 27.3) * mm});
            skLineSegment(sketch, "E1070", {"start": v(6.75, 27.3) * mm, "end": v(6.86, 27.48) * mm});
            skLineSegment(sketch, "E1071", {"start": v(6.86, 27.48) * mm, "end": v(6.97, 27.66) * mm});
            skLineSegment(sketch, "E1072", {"start": v(6.97, 27.66) * mm, "end": v(7.06, 27.84) * mm});
            skLineSegment(sketch, "E1073", {"start": v(7.06, 27.84) * mm, "end": v(7.16, 28.02) * mm});
            skLineSegment(sketch, "E1074", {"start": v(7.16, 28.02) * mm, "end": v(7.25, 28.2) * mm});
            skLineSegment(sketch, "E1075", {"start": v(7.25, 28.2) * mm, "end": v(7.33, 28.39) * mm});
            skLineSegment(sketch, "E1076", {"start": v(7.33, 28.39) * mm, "end": v(7.4, 28.57) * mm});
            skLineSegment(sketch, "E1077", {"start": v(7.4, 28.57) * mm, "end": v(7.48, 28.76) * mm});
            skLineSegment(sketch, "E1078", {"start": v(7.48, 28.76) * mm, "end": v(7.55, 28.95) * mm});
            skLineSegment(sketch, "E1079", {"start": v(7.55, 28.95) * mm, "end": v(7.61, 29.14) * mm});
            skLineSegment(sketch, "E1080", {"start": v(7.61, 29.14) * mm, "end": v(7.67, 29.33) * mm});
            skLineSegment(sketch, "E1081", {"start": v(7.67, 29.33) * mm, "end": v(7.72, 29.53) * mm});
            skLineSegment(sketch, "E1082", {"start": v(7.72, 29.53) * mm, "end": v(7.76, 29.72) * mm});
            skLineSegment(sketch, "E1083", {"start": v(7.76, 29.72) * mm, "end": v(7.8, 29.92) * mm});
            skLineSegment(sketch, "E1084", {"start": v(7.8, 29.92) * mm, "end": v(7.84, 30.12) * mm});
            skLineSegment(sketch, "E1085", {"start": v(7.84, 30.12) * mm, "end": v(7.86, 30.32) * mm});
            skLineSegment(sketch, "E1086", {"start": v(7.86, 30.32) * mm, "end": v(7.89, 30.53) * mm});
            skLineSegment(sketch, "E1087", {"start": v(7.89, 30.53) * mm, "end": v(7.9, 30.73) * mm});
            skLineSegment(sketch, "E1088", {"start": v(7.9, 30.73) * mm, "end": v(7.91, 30.94) * mm});
            skLineSegment(sketch, "E1089", {"start": v(7.91, 30.94) * mm, "end": v(7.92, 31.15) * mm});
            skLineSegment(sketch, "E1090", {"start": v(7.92, 31.15) * mm, "end": v(7.91, 31.36) * mm});
            skLineSegment(sketch, "E1091", {"start": v(7.91, 31.36) * mm, "end": v(7.9, 31.58) * mm});
            skLineSegment(sketch, "E1092", {"start": v(7.9, 31.58) * mm, "end": v(7.89, 31.8) * mm});
            skLineSegment(sketch, "E1093", {"start": v(7.89, 31.8) * mm, "end": v(7.87, 32.01) * mm});
            skLineSegment(sketch, "E1094", {"start": v(7.87, 32.01) * mm, "end": v(7.84, 32.23) * mm});
            skLineSegment(sketch, "E1095", {"start": v(7.84, 32.23) * mm, "end": v(7.8, 32.42) * mm});
            skLineSegment(sketch, "E1096", {"start": v(7.8, 32.42) * mm, "end": v(7.78, 32.6) * mm});
            skLineSegment(sketch, "E1097", {"start": v(7.78, 32.6) * mm, "end": v(7.74, 32.78) * mm});
            skLineSegment(sketch, "E1098", {"start": v(7.74, 32.78) * mm, "end": v(7.7, 32.95) * mm});
            skLineSegment(sketch, "E1099", {"start": v(7.7, 32.95) * mm, "end": v(7.65, 33.12) * mm});
            skLineSegment(sketch, "E1100", {"start": v(7.65, 33.12) * mm, "end": v(7.6, 33.29) * mm});
            skLineSegment(sketch, "E1101", {"start": v(7.6, 33.29) * mm, "end": v(7.54, 33.45) * mm});
            skLineSegment(sketch, "E1102", {"start": v(7.54, 33.45) * mm, "end": v(7.48, 33.61) * mm});
            skLineSegment(sketch, "E1103", {"start": v(7.48, 33.61) * mm, "end": v(7.41, 33.77) * mm});
            skLineSegment(sketch, "E1104", {"start": v(7.41, 33.77) * mm, "end": v(7.34, 33.93) * mm});
            skLineSegment(sketch, "E1105", {"start": v(7.34, 33.93) * mm, "end": v(7.27, 34.08) * mm});
            skLineSegment(sketch, "E1106", {"start": v(7.27, 34.08) * mm, "end": v(7.2, 34.23) * mm});
            skLineSegment(sketch, "E1107", {"start": v(7.2, 34.23) * mm, "end": v(7.11, 34.38) * mm});
            skLineSegment(sketch, "E1108", {"start": v(7.11, 34.38) * mm, "end": v(7.03, 34.52) * mm});
            skLineSegment(sketch, "E1109", {"start": v(7.03, 34.52) * mm, "end": v(6.94, 34.66) * mm});
            skLineSegment(sketch, "E1110", {"start": v(6.94, 34.66) * mm, "end": v(6.84, 34.8) * mm});
            skLineSegment(sketch, "E1111", {"start": v(6.84, 34.8) * mm, "end": v(6.75, 34.94) * mm});
            skLineSegment(sketch, "E1112", {"start": v(6.75, 34.94) * mm, "end": v(6.64, 35.07) * mm});
            skLineSegment(sketch, "E1113", {"start": v(6.64, 35.07) * mm, "end": v(6.54, 35.2) * mm});
            skLineSegment(sketch, "E1114", {"start": v(6.54, 35.2) * mm, "end": v(6.43, 35.33) * mm});
            skLineSegment(sketch, "E1115", {"start": v(6.43, 35.33) * mm, "end": v(6.32, 35.46) * mm});
            skLineSegment(sketch, "E1116", {"start": v(6.32, 35.46) * mm, "end": v(6.2, 35.59) * mm});
            skLineSegment(sketch, "E1117", {"start": v(6.2, 35.59) * mm, "end": v(6.08, 35.7) * mm});
            skLineSegment(sketch, "E1118", {"start": v(6.08, 35.7) * mm, "end": v(5.96, 35.83) * mm});
            skLineSegment(sketch, "E1119", {"start": v(5.96, 35.83) * mm, "end": v(5.84, 35.95) * mm});
            skLineSegment(sketch, "E1120", {"start": v(5.84, 35.95) * mm, "end": v(5.7, 36.07) * mm});
            skLineSegment(sketch, "E1121", {"start": v(5.7, 36.07) * mm, "end": v(5.57, 36.18) * mm});
            skLineSegment(sketch, "E1122", {"start": v(5.57, 36.18) * mm, "end": v(5.44, 36.3) * mm});
            skLineSegment(sketch, "E1123", {"start": v(5.44, 36.3) * mm, "end": v(5.3, 36.4) * mm});
            skLineSegment(sketch, "E1124", {"start": v(5.3, 36.4) * mm, "end": v(5.16, 36.51) * mm});
            skLineSegment(sketch, "E1125", {"start": v(5.16, 36.51) * mm, "end": v(5.01, 36.62) * mm});
            skLineSegment(sketch, "E1126", {"start": v(5.01, 36.62) * mm, "end": v(4.86, 36.73) * mm});
            skLineSegment(sketch, "E1127", {"start": v(4.86, 36.73) * mm, "end": v(4.7, 36.3) * mm});
            skLineSegment(sketch, "E1128", {"start": v(4.7, 36.3) * mm, "end": v(4.55, 35.89) * mm});
            skLineSegment(sketch, "E1129", {"start": v(4.55, 35.89) * mm, "end": v(4.39, 35.47) * mm});
            skLineSegment(sketch, "E1130", {"start": v(4.39, 35.47) * mm, "end": v(4.23, 35.05) * mm});
            skLineSegment(sketch, "E1131", {"start": v(4.23, 35.05) * mm, "end": v(4.07, 34.64) * mm});
            skLineSegment(sketch, "E1132", {"start": v(4.07, 34.64) * mm, "end": v(3.91, 34.22) * mm});
            skLineSegment(sketch, "E1133", {"start": v(3.91, 34.22) * mm, "end": v(3.75, 33.8) * mm});
            skLineSegment(sketch, "E1134", {"start": v(3.75, 33.8) * mm, "end": v(3.6, 33.38) * mm});
            skLineSegment(sketch, "E1135", {"start": v(3.6, 33.38) * mm, "end": v(3.44, 32.97) * mm});
            skLineSegment(sketch, "E1136", {"start": v(3.44, 32.97) * mm, "end": v(3.28, 32.55) * mm});
            skLineSegment(sketch, "E1137", {"start": v(3.28, 32.55) * mm, "end": v(3.12, 32.13) * mm});
            skLineSegment(sketch, "E1138", {"start": v(3.12, 32.13) * mm, "end": v(2.96, 31.72) * mm});
            skLineSegment(sketch, "E1139", {"start": v(2.96, 31.72) * mm, "end": v(2.8, 31.3) * mm});
            skLineSegment(sketch, "E1140", {"start": v(2.8, 31.3) * mm, "end": v(2.64, 30.88) * mm});
            skLineSegment(sketch, "E1141", {"start": v(2.64, 30.88) * mm, "end": v(2.48, 30.46) * mm});
            skLineSegment(sketch, "E1142", {"start": v(2.48, 30.46) * mm, "end": v(2.32, 30.05) * mm});
            skLineSegment(sketch, "E1143", {"start": v(2.32, 30.05) * mm, "end": v(2.17, 29.63) * mm});
            skLineSegment(sketch, "E1144", {"start": v(2.17, 29.63) * mm, "end": v(2, 29.2) * mm});
            skLineSegment(sketch, "E1145", {"start": v(2, 29.2) * mm, "end": v(1.85, 28.8) * mm});
            skLineSegment(sketch, "E1146", {"start": v(1.85, 28.8) * mm, "end": v(1.69, 28.37) * mm});
            skLineSegment(sketch, "E1147", {"start": v(1.69, 28.37) * mm, "end": v(1.53, 27.95) * mm});
            skLineSegment(sketch, "E1148", {"start": v(1.53, 27.95) * mm, "end": v(1.37, 27.53) * mm});
            skLineSegment(sketch, "E1149", {"start": v(1.37, 27.53) * mm, "end": v(1.21, 27.11) * mm});
            skLineSegment(sketch, "E1150", {"start": v(1.21, 27.11) * mm, "end": v(1.05, 26.7) * mm});
            skLineSegment(sketch, "E1151", {"start": v(1.05, 26.7) * mm, "end": v(0.9, 26.27) * mm});
            skLineSegment(sketch, "E1152", {"start": v(0.9, 26.27) * mm, "end": v(0.73, 25.85) * mm});
            skLineSegment(sketch, "E1153", {"start": v(0.73, 25.85) * mm, "end": v(0.57, 25.43) * mm});
            skLineSegment(sketch, "E1154", {"start": v(0.57, 25.43) * mm, "end": v(0.4, 25) * mm});
            skLineSegment(sketch, "E1155", {"start": v(0.4, 25) * mm, "end": v(0.25, 24.59) * mm});
            skLineSegment(sketch, "E1156", {"start": v(0.25, 24.59) * mm, "end": v(0.09, 24.16) * mm});
            skLineSegment(sketch, "E1157", {"start": v(0.09, 24.16) * mm, "end": v(-0.07, 23.74) * mm});
            skLineSegment(sketch, "E1158", {"start": v(-0.07, 23.74) * mm, "end": v(-0.24, 23.31) * mm});
            skLineSegment(sketch, "E1159", {"start": v(-4.45, 25.1) * mm, "end": v(-4.3, 25.53) * mm});
            skLineSegment(sketch, "E1160", {"start": v(-4.3, 25.53) * mm, "end": v(-4.14, 25.95) * mm});
            skLineSegment(sketch, "E1161", {"start": v(-4.14, 25.95) * mm, "end": v(-4, 26.38) * mm});
            skLineSegment(sketch, "E1162", {"start": v(-4, 26.38) * mm, "end": v(-3.84, 26.8) * mm});
            skLineSegment(sketch, "E1163", {"start": v(-3.84, 26.8) * mm, "end": v(-3.7, 27.22) * mm});
            skLineSegment(sketch, "E1164", {"start": v(-3.7, 27.22) * mm, "end": v(-3.54, 27.65) * mm});
            skLineSegment(sketch, "E1165", {"start": v(-3.54, 27.65) * mm, "end": v(-3.39, 28.07) * mm});
            skLineSegment(sketch, "E1166", {"start": v(-3.39, 28.07) * mm, "end": v(-3.24, 28.5) * mm});
            skLineSegment(sketch, "E1167", {"start": v(-3.24, 28.5) * mm, "end": v(-3.09, 28.92) * mm});
            skLineSegment(sketch, "E1168", {"start": v(-3.09, 28.92) * mm, "end": v(-2.94, 29.34) * mm});
            skLineSegment(sketch, "E1169", {"start": v(-2.94, 29.34) * mm, "end": v(-2.78, 29.76) * mm});
            skLineSegment(sketch, "E1170", {"start": v(-2.78, 29.76) * mm, "end": v(-2.63, 30.18) * mm});
            skLineSegment(sketch, "E1171", {"start": v(-2.63, 30.18) * mm, "end": v(-2.48, 30.6) * mm});
            skLineSegment(sketch, "E1172", {"start": v(-2.48, 30.6) * mm, "end": v(-2.33, 31.03) * mm});
            skLineSegment(sketch, "E1173", {"start": v(-2.33, 31.03) * mm, "end": v(-2.18, 31.45) * mm});
            skLineSegment(sketch, "E1174", {"start": v(-2.18, 31.45) * mm, "end": v(-2.03, 31.87) * mm});
            skLineSegment(sketch, "E1175", {"start": v(-2.03, 31.87) * mm, "end": v(-1.88, 32.3) * mm});
            skLineSegment(sketch, "E1176", {"start": v(-1.88, 32.3) * mm, "end": v(-1.73, 32.72) * mm});
            skLineSegment(sketch, "E1177", {"start": v(-1.73, 32.72) * mm, "end": v(-1.58, 33.14) * mm});
            skLineSegment(sketch, "E1178", {"start": v(-1.58, 33.14) * mm, "end": v(-1.42, 33.57) * mm});
            skLineSegment(sketch, "E1179", {"start": v(-1.42, 33.57) * mm, "end": v(-1.27, 33.99) * mm});
            skLineSegment(sketch, "E1180", {"start": v(-1.27, 33.99) * mm, "end": v(-1.12, 34.41) * mm});
            skLineSegment(sketch, "E1181", {"start": v(-1.12, 34.41) * mm, "end": v(-0.97, 34.83) * mm});
            skLineSegment(sketch, "E1182", {"start": v(-0.97, 34.83) * mm, "end": v(-0.82, 35.26) * mm});
            skLineSegment(sketch, "E1183", {"start": v(-0.82, 35.26) * mm, "end": v(-0.67, 35.68) * mm});
            skLineSegment(sketch, "E1184", {"start": v(-0.67, 35.68) * mm, "end": v(-0.52, 36.1) * mm});
            skLineSegment(sketch, "E1185", {"start": v(-0.52, 36.1) * mm, "end": v(-0.37, 36.52) * mm});
            skLineSegment(sketch, "E1186", {"start": v(-0.37, 36.52) * mm, "end": v(-0.22, 36.95) * mm});
            skLineSegment(sketch, "E1187", {"start": v(-0.22, 36.95) * mm, "end": v(-0.07, 37.37) * mm});
            skLineSegment(sketch, "E1188", {"start": v(-0.07, 37.37) * mm, "end": v(0.09, 37.8) * mm});
            skLineSegment(sketch, "E1189", {"start": v(0.09, 37.8) * mm, "end": v(0.24, 38.22) * mm});
            skLineSegment(sketch, "E1190", {"start": v(0.24, 38.22) * mm, "end": v(0.39, 38.64) * mm});
            skLineSegment(sketch, "E1191", {"start": v(0.39, 38.64) * mm, "end": v(0.1, 38.67) * mm});
            skLineSegment(sketch, "E1192", {"start": v(0.1, 38.67) * mm, "end": v(-0.18, 38.68) * mm});
            skLineSegment(sketch, "E1193", {"start": v(-0.18, 38.68) * mm, "end": v(-0.47, 38.68) * mm});
            skLineSegment(sketch, "E1194", {"start": v(-0.47, 38.68) * mm, "end": v(-0.75, 38.67) * mm});
            skLineSegment(sketch, "E1195", {"start": v(-0.75, 38.67) * mm, "end": v(-1.03, 38.64) * mm});
            skLineSegment(sketch, "E1196", {"start": v(-1.03, 38.64) * mm, "end": v(-1.3, 38.6) * mm});
            skLineSegment(sketch, "E1197", {"start": v(-1.3, 38.6) * mm, "end": v(-1.58, 38.56) * mm});
            skLineSegment(sketch, "E1198", {"start": v(-1.58, 38.56) * mm, "end": v(-1.85, 38.5) * mm});
            skLineSegment(sketch, "E1199", {"start": v(-1.85, 38.5) * mm, "end": v(-2.12, 38.43) * mm});
            skLineSegment(sketch, "E1200", {"start": v(-2.12, 38.43) * mm, "end": v(-2.38, 38.35) * mm});
            skLineSegment(sketch, "E1201", {"start": v(-2.38, 38.35) * mm, "end": v(-2.64, 38.26) * mm});
            skLineSegment(sketch, "E1202", {"start": v(-2.64, 38.26) * mm, "end": v(-2.9, 38.16) * mm});
            skLineSegment(sketch, "E1203", {"start": v(-2.9, 38.16) * mm, "end": v(-3.15, 38.04) * mm});
            skLineSegment(sketch, "E1204", {"start": v(-3.15, 38.04) * mm, "end": v(-3.4, 37.92) * mm});
            skLineSegment(sketch, "E1205", {"start": v(-3.4, 37.92) * mm, "end": v(-3.64, 37.78) * mm});
            skLineSegment(sketch, "E1206", {"start": v(-3.64, 37.78) * mm, "end": v(-3.88, 37.64) * mm});
            skLineSegment(sketch, "E1207", {"start": v(-3.88, 37.64) * mm, "end": v(-4.1, 37.48) * mm});
            skLineSegment(sketch, "E1208", {"start": v(-4.1, 37.48) * mm, "end": v(-4.33, 37.32) * mm});
            skLineSegment(sketch, "E1209", {"start": v(-4.33, 37.32) * mm, "end": v(-4.55, 37.14) * mm});
            skLineSegment(sketch, "E1210", {"start": v(-4.55, 37.14) * mm, "end": v(-4.77, 36.96) * mm});
            skLineSegment(sketch, "E1211", {"start": v(-4.77, 36.96) * mm, "end": v(-4.98, 36.76) * mm});
            skLineSegment(sketch, "E1212", {"start": v(-4.98, 36.76) * mm, "end": v(-5.18, 36.56) * mm});
            skLineSegment(sketch, "E1213", {"start": v(-5.18, 36.56) * mm, "end": v(-5.37, 36.35) * mm});
            skLineSegment(sketch, "E1214", {"start": v(-5.37, 36.35) * mm, "end": v(-5.56, 36.12) * mm});
            skLineSegment(sketch, "E1215", {"start": v(-5.56, 36.12) * mm, "end": v(-5.74, 35.9) * mm});
            skLineSegment(sketch, "E1216", {"start": v(-5.74, 35.9) * mm, "end": v(-5.91, 35.65) * mm});
            skLineSegment(sketch, "E1217", {"start": v(-5.91, 35.65) * mm, "end": v(-6.08, 35.4) * mm});
            skLineSegment(sketch, "E1218", {"start": v(-6.08, 35.4) * mm, "end": v(-6.24, 35.14) * mm});
            skLineSegment(sketch, "E1219", {"start": v(-6.24, 35.14) * mm, "end": v(-6.38, 34.87) * mm});
            skLineSegment(sketch, "E1220", {"start": v(-6.38, 34.87) * mm, "end": v(-6.52, 34.6) * mm});
            skLineSegment(sketch, "E1221", {"start": v(-6.52, 34.6) * mm, "end": v(-6.65, 34.31) * mm});
            skLineSegment(sketch, "E1222", {"start": v(-6.65, 34.31) * mm, "end": v(-6.78, 34.02) * mm});
            skLineSegment(sketch, "E1223", {"start": v(-6.78, 34.02) * mm, "end": v(-6.89, 33.72) * mm});
            skLineSegment(sketch, "E1224", {"start": v(-6.89, 33.72) * mm, "end": v(-6.99, 33.42) * mm});
            skLineSegment(sketch, "E1225", {"start": v(-6.99, 33.42) * mm, "end": v(-7.07, 33.11) * mm});
            skLineSegment(sketch, "E1226", {"start": v(-7.07, 33.11) * mm, "end": v(-7.15, 32.8) * mm});
            skLineSegment(sketch, "E1227", {"start": v(-7.15, 32.8) * mm, "end": v(-7.2, 32.5) * mm});
            skLineSegment(sketch, "E1228", {"start": v(-7.2, 32.5) * mm, "end": v(-7.26, 32.2) * mm});
            skLineSegment(sketch, "E1229", {"start": v(-7.26, 32.2) * mm, "end": v(-7.3, 31.89) * mm});
            skLineSegment(sketch, "E1230", {"start": v(-7.3, 31.89) * mm, "end": v(-7.32, 31.58) * mm});
            skLineSegment(sketch, "E1231", {"start": v(-7.32, 31.58) * mm, "end": v(-7.33, 31.27) * mm});
            skLineSegment(sketch, "E1232", {"start": v(-7.33, 31.27) * mm, "end": v(-7.33, 30.97) * mm});
            skLineSegment(sketch, "E1233", {"start": v(-7.33, 30.97) * mm, "end": v(-7.32, 30.67) * mm});
            skLineSegment(sketch, "E1234", {"start": v(-7.32, 30.67) * mm, "end": v(-7.3, 30.36) * mm});
            skLineSegment(sketch, "E1235", {"start": v(-7.3, 30.36) * mm, "end": v(-7.26, 30.06) * mm});
            skLineSegment(sketch, "E1236", {"start": v(-7.26, 30.06) * mm, "end": v(-7.21, 29.76) * mm});
            skLineSegment(sketch, "E1237", {"start": v(-7.21, 29.76) * mm, "end": v(-7.15, 29.47) * mm});
            skLineSegment(sketch, "E1238", {"start": v(-7.15, 29.47) * mm, "end": v(-7.08, 29.17) * mm});
            skLineSegment(sketch, "E1239", {"start": v(-7.08, 29.17) * mm, "end": v(-7, 28.88) * mm});
            skLineSegment(sketch, "E1240", {"start": v(-7, 28.88) * mm, "end": v(-6.9, 28.6) * mm});
            skLineSegment(sketch, "E1241", {"start": v(-6.9, 28.6) * mm, "end": v(-6.8, 28.31) * mm});
            skLineSegment(sketch, "E1242", {"start": v(-6.8, 28.31) * mm, "end": v(-6.69, 28.03) * mm});
            skLineSegment(sketch, "E1243", {"start": v(-6.69, 28.03) * mm, "end": v(-6.56, 27.76) * mm});
            skLineSegment(sketch, "E1244", {"start": v(-6.56, 27.76) * mm, "end": v(-6.42, 27.49) * mm});
            skLineSegment(sketch, "E1245", {"start": v(-6.42, 27.49) * mm, "end": v(-6.27, 27.22) * mm});
            skLineSegment(sketch, "E1246", {"start": v(-6.27, 27.22) * mm, "end": v(-6.11, 26.96) * mm});
            skLineSegment(sketch, "E1247", {"start": v(-6.11, 26.96) * mm, "end": v(-5.94, 26.7) * mm});
            skLineSegment(sketch, "E1248", {"start": v(-5.94, 26.7) * mm, "end": v(-5.76, 26.46) * mm});
            skLineSegment(sketch, "E1249", {"start": v(-5.76, 26.46) * mm, "end": v(-5.57, 26.22) * mm});
            skLineSegment(sketch, "E1250", {"start": v(-5.57, 26.22) * mm, "end": v(-5.36, 25.98) * mm});
            skLineSegment(sketch, "E1251", {"start": v(-5.36, 25.98) * mm, "end": v(-5.15, 25.75) * mm});
            skLineSegment(sketch, "E1252", {"start": v(-5.15, 25.75) * mm, "end": v(-4.93, 25.53) * mm});
            skLineSegment(sketch, "E1253", {"start": v(-4.93, 25.53) * mm, "end": v(-4.7, 25.31) * mm});
            skLineSegment(sketch, "E1254", {"start": v(-4.7, 25.31) * mm, "end": v(-4.45, 25.1) * mm});
            skLineSegment(sketch, "E1255", {"start": v(-5.66, 22.05) * mm, "end": v(-6.07, 22.17) * mm});
            skLineSegment(sketch, "E1256", {"start": v(-6.07, 22.17) * mm, "end": v(-6.48, 22.29) * mm});
            skLineSegment(sketch, "E1257", {"start": v(-6.48, 22.29) * mm, "end": v(-6.89, 22.4) * mm});
            skLineSegment(sketch, "E1258", {"start": v(-6.89, 22.4) * mm, "end": v(-7.29, 22.54) * mm});
            skLineSegment(sketch, "E1259", {"start": v(-7.29, 22.54) * mm, "end": v(-7.69, 22.67) * mm});
            skLineSegment(sketch, "E1260", {"start": v(-7.69, 22.67) * mm, "end": v(-8.09, 22.8) * mm});
            skLineSegment(sketch, "E1261", {"start": v(-8.09, 22.8) * mm, "end": v(-8.48, 22.94) * mm});
            skLineSegment(sketch, "E1262", {"start": v(-8.48, 22.94) * mm, "end": v(-8.87, 23.09) * mm});
            skLineSegment(sketch, "E1263", {"start": v(-8.87, 23.09) * mm, "end": v(-9.26, 23.24) * mm});
            skLineSegment(sketch, "E1264", {"start": v(-9.26, 23.24) * mm, "end": v(-9.64, 23.4) * mm});
            skLineSegment(sketch, "E1265", {"start": v(-9.64, 23.4) * mm, "end": v(-10.02, 23.56) * mm});
            skLineSegment(sketch, "E1266", {"start": v(-10.02, 23.56) * mm, "end": v(-10.39, 23.73) * mm});
            skLineSegment(sketch, "E1267", {"start": v(-10.39, 23.73) * mm, "end": v(-10.76, 23.9) * mm});
            skLineSegment(sketch, "E1268", {"start": v(-10.76, 23.9) * mm, "end": v(-11.12, 24.1) * mm});
            skLineSegment(sketch, "E1269", {"start": v(-11.12, 24.1) * mm, "end": v(-11.48, 24.29) * mm});
            skLineSegment(sketch, "E1270", {"start": v(-11.48, 24.29) * mm, "end": v(-11.83, 24.49) * mm});
            skLineSegment(sketch, "E1271", {"start": v(-11.83, 24.49) * mm, "end": v(-12.18, 24.7) * mm});
            skLineSegment(sketch, "E1272", {"start": v(-12.18, 24.7) * mm, "end": v(-12.52, 24.92) * mm});
            skLineSegment(sketch, "E1273", {"start": v(-12.52, 24.92) * mm, "end": v(-12.86, 25.15) * mm});
            skLineSegment(sketch, "E1274", {"start": v(-12.86, 25.15) * mm, "end": v(-13.18, 25.4) * mm});
            skLineSegment(sketch, "E1275", {"start": v(-13.18, 25.4) * mm, "end": v(-13.5, 25.64) * mm});
            skLineSegment(sketch, "E1276", {"start": v(-13.5, 25.64) * mm, "end": v(-13.82, 25.9) * mm});
            skLineSegment(sketch, "E1277", {"start": v(-13.82, 25.9) * mm, "end": v(-14.13, 26.18) * mm});
            skLineSegment(sketch, "E1278", {"start": v(-14.13, 26.18) * mm, "end": v(-14.42, 26.46) * mm});
            skLineSegment(sketch, "E1279", {"start": v(-14.42, 26.46) * mm, "end": v(-14.72, 26.76) * mm});
            skLineSegment(sketch, "E1280", {"start": v(-14.72, 26.76) * mm, "end": v(-15, 27.07) * mm});
            skLineSegment(sketch, "E1281", {"start": v(-15, 27.07) * mm, "end": v(-15.27, 27.39) * mm});
            skLineSegment(sketch, "E1282", {"start": v(-15.27, 27.39) * mm, "end": v(-15.54, 27.72) * mm});
            skLineSegment(sketch, "E1283", {"start": v(-15.54, 27.72) * mm, "end": v(-15.8, 28.07) * mm});
            skLineSegment(sketch, "E1284", {"start": v(-15.8, 28.07) * mm, "end": v(-16.05, 28.43) * mm});
            skLineSegment(sketch, "E1285", {"start": v(-16.05, 28.43) * mm, "end": v(-16.28, 28.81) * mm});
            skLineSegment(sketch, "E1286", {"start": v(-16.28, 28.81) * mm, "end": v(-16.51, 29.2) * mm});
            skLineSegment(sketch, "E1287", {"start": v(-16.51, 29.2) * mm, "end": v(-16.5, 29.12) * mm});
            skLineSegment(sketch, "E1288", {"start": v(-16.5, 29.12) * mm, "end": v(-16.5, 29.04) * mm});
            skLineSegment(sketch, "E1289", {"start": v(-16.5, 29.04) * mm, "end": v(-16.48, 28.96) * mm});
            skLineSegment(sketch, "E1290", {"start": v(-16.48, 28.96) * mm, "end": v(-16.47, 28.88) * mm});
            skLineSegment(sketch, "E1291", {"start": v(-16.47, 28.88) * mm, "end": v(-16.46, 28.8) * mm});
            skLineSegment(sketch, "E1292", {"start": v(-16.46, 28.8) * mm, "end": v(-16.45, 28.72) * mm});
            skLineSegment(sketch, "E1293", {"start": v(-16.45, 28.72) * mm, "end": v(-16.43, 28.64) * mm});
            skLineSegment(sketch, "E1294", {"start": v(-16.43, 28.64) * mm, "end": v(-16.42, 28.56) * mm});
            skLineSegment(sketch, "E1295", {"start": v(-16.42, 28.56) * mm, "end": v(-16.4, 28.49) * mm});
            skLineSegment(sketch, "E1296", {"start": v(-16.4, 28.49) * mm, "end": v(-16.4, 28.4) * mm});
            skLineSegment(sketch, "E1297", {"start": v(-16.4, 28.4) * mm, "end": v(-16.38, 28.33) * mm});
            skLineSegment(sketch, "E1298", {"start": v(-16.38, 28.33) * mm, "end": v(-16.37, 28.25) * mm});
            skLineSegment(sketch, "E1299", {"start": v(-16.37, 28.25) * mm, "end": v(-16.36, 28.18) * mm});
            skLineSegment(sketch, "E1300", {"start": v(-16.36, 28.18) * mm, "end": v(-16.34, 28.1) * mm});
            skLineSegment(sketch, "E1301", {"start": v(-16.34, 28.1) * mm, "end": v(-16.33, 28.02) * mm});
            skLineSegment(sketch, "E1302", {"start": v(-16.33, 28.02) * mm, "end": v(-16.31, 27.94) * mm});
            skLineSegment(sketch, "E1303", {"start": v(-16.31, 27.94) * mm, "end": v(-16.3, 27.87) * mm});
            skLineSegment(sketch, "E1304", {"start": v(-16.3, 27.87) * mm, "end": v(-16.28, 27.8) * mm});
            skLineSegment(sketch, "E1305", {"start": v(-16.28, 27.8) * mm, "end": v(-16.27, 27.72) * mm});
            skLineSegment(sketch, "E1306", {"start": v(-16.27, 27.72) * mm, "end": v(-16.25, 27.64) * mm});
            skLineSegment(sketch, "E1307", {"start": v(-16.25, 27.64) * mm, "end": v(-16.24, 27.56) * mm});
            skLineSegment(sketch, "E1308", {"start": v(-16.24, 27.56) * mm, "end": v(-16.22, 27.49) * mm});
            skLineSegment(sketch, "E1309", {"start": v(-16.22, 27.49) * mm, "end": v(-16.2, 27.41) * mm});
            skLineSegment(sketch, "E1310", {"start": v(-16.2, 27.41) * mm, "end": v(-16.19, 27.34) * mm});
            skLineSegment(sketch, "E1311", {"start": v(-16.19, 27.34) * mm, "end": v(-16.17, 27.26) * mm});
            skLineSegment(sketch, "E1312", {"start": v(-16.17, 27.26) * mm, "end": v(-16.16, 27.19) * mm});
            skLineSegment(sketch, "E1313", {"start": v(-16.16, 27.19) * mm, "end": v(-16.14, 27.11) * mm});
            skLineSegment(sketch, "E1314", {"start": v(-16.14, 27.11) * mm, "end": v(-16.12, 27.04) * mm});
            skLineSegment(sketch, "E1315", {"start": v(-16.12, 27.04) * mm, "end": v(-16.1, 26.96) * mm});
            skLineSegment(sketch, "E1316", {"start": v(-16.1, 26.96) * mm, "end": v(-16.08, 26.89) * mm});
            skLineSegment(sketch, "E1317", {"start": v(-16.08, 26.89) * mm, "end": v(-16.07, 26.81) * mm});
            skLineSegment(sketch, "E1318", {"start": v(-16.07, 26.81) * mm, "end": v(-16.05, 26.74) * mm});
            skLineSegment(sketch, "E1319", {"start": v(-16.05, 26.74) * mm, "end": v(-16, 26.55) * mm});
            skLineSegment(sketch, "E1320", {"start": v(-16, 26.55) * mm, "end": v(-15.95, 26.37) * mm});
            skLineSegment(sketch, "E1321", {"start": v(-15.95, 26.37) * mm, "end": v(-15.9, 26.18) * mm});
            skLineSegment(sketch, "E1322", {"start": v(-15.9, 26.18) * mm, "end": v(-15.84, 26) * mm});
            skLineSegment(sketch, "E1323", {"start": v(-15.84, 26) * mm, "end": v(-15.78, 25.81) * mm});
            skLineSegment(sketch, "E1324", {"start": v(-15.78, 25.81) * mm, "end": v(-15.72, 25.63) * mm});
            skLineSegment(sketch, "E1325", {"start": v(-15.72, 25.63) * mm, "end": v(-15.65, 25.45) * mm});
            skLineSegment(sketch, "E1326", {"start": v(-15.65, 25.45) * mm, "end": v(-15.59, 25.27) * mm});
            skLineSegment(sketch, "E1327", {"start": v(-15.59, 25.27) * mm, "end": v(-15.52, 25.1) * mm});
            skLineSegment(sketch, "E1328", {"start": v(-15.52, 25.1) * mm, "end": v(-15.45, 24.91) * mm});
            skLineSegment(sketch, "E1329", {"start": v(-15.45, 24.91) * mm, "end": v(-15.38, 24.74) * mm});
            skLineSegment(sketch, "E1330", {"start": v(-15.38, 24.74) * mm, "end": v(-15.3, 24.56) * mm});
            skLineSegment(sketch, "E1331", {"start": v(-15.3, 24.56) * mm, "end": v(-15.23, 24.39) * mm});
            skLineSegment(sketch, "E1332", {"start": v(-15.23, 24.39) * mm, "end": v(-15.15, 24.21) * mm});
            skLineSegment(sketch, "E1333", {"start": v(-15.15, 24.21) * mm, "end": v(-15.07, 24.04) * mm});
            skLineSegment(sketch, "E1334", {"start": v(-15.07, 24.04) * mm, "end": v(-14.98, 23.87) * mm});
            skLineSegment(sketch, "E1335", {"start": v(-14.98, 23.87) * mm, "end": v(-14.9, 23.7) * mm});
            skLineSegment(sketch, "E1336", {"start": v(-14.9, 23.7) * mm, "end": v(-14.81, 23.53) * mm});
            skLineSegment(sketch, "E1337", {"start": v(-14.81, 23.53) * mm, "end": v(-14.73, 23.36) * mm});
            skLineSegment(sketch, "E1338", {"start": v(-14.73, 23.36) * mm, "end": v(-14.64, 23.19) * mm});
            skLineSegment(sketch, "E1339", {"start": v(-14.64, 23.19) * mm, "end": v(-14.55, 23.02) * mm});
            skLineSegment(sketch, "E1340", {"start": v(-14.55, 23.02) * mm, "end": v(-14.45, 22.85) * mm});
            skLineSegment(sketch, "E1341", {"start": v(-14.45, 22.85) * mm, "end": v(-14.36, 22.69) * mm});
            skLineSegment(sketch, "E1342", {"start": v(-14.36, 22.69) * mm, "end": v(-14.26, 22.52) * mm});
            skLineSegment(sketch, "E1343", {"start": v(-14.26, 22.52) * mm, "end": v(-14.16, 22.36) * mm});
            skLineSegment(sketch, "E1344", {"start": v(-14.16, 22.36) * mm, "end": v(-14.06, 22.2) * mm});
            skLineSegment(sketch, "E1345", {"start": v(-14.06, 22.2) * mm, "end": v(-13.96, 22.03) * mm});
            skLineSegment(sketch, "E1346", {"start": v(-13.96, 22.03) * mm, "end": v(-13.86, 21.87) * mm});
            skLineSegment(sketch, "E1347", {"start": v(-13.86, 21.87) * mm, "end": v(-13.75, 21.71) * mm});
            skLineSegment(sketch, "E1348", {"start": v(-13.75, 21.71) * mm, "end": v(-13.65, 21.55) * mm});
            skLineSegment(sketch, "E1349", {"start": v(-13.65, 21.55) * mm, "end": v(-13.54, 21.4) * mm});
            skLineSegment(sketch, "E1350", {"start": v(-13.54, 21.4) * mm, "end": v(-13.43, 21.23) * mm});
            skLineSegment(sketch, "E1351", {"start": v(-13.43, 21.23) * mm, "end": v(-13.32, 21.08) * mm});
            skLineSegment(sketch, "E1352", {"start": v(-13.32, 21.08) * mm, "end": v(-13.22, 20.92) * mm});
            skLineSegment(sketch, "E1353", {"start": v(-13.22, 20.92) * mm, "end": v(-13.1, 20.77) * mm});
            skLineSegment(sketch, "E1354", {"start": v(-13.1, 20.77) * mm, "end": v(-13, 20.62) * mm});
            skLineSegment(sketch, "E1355", {"start": v(-13, 20.62) * mm, "end": v(-12.89, 20.47) * mm});
            skLineSegment(sketch, "E1356", {"start": v(-12.89, 20.47) * mm, "end": v(-12.77, 20.32) * mm});
            skLineSegment(sketch, "E1357", {"start": v(-12.77, 20.32) * mm, "end": v(-12.66, 20.17) * mm});
            skLineSegment(sketch, "E1358", {"start": v(-12.66, 20.17) * mm, "end": v(-12.54, 20.03) * mm});
            skLineSegment(sketch, "E1359", {"start": v(-12.54, 20.03) * mm, "end": v(-12.43, 19.88) * mm});
            skLineSegment(sketch, "E1360", {"start": v(-12.43, 19.88) * mm, "end": v(-12.3, 19.74) * mm});
            skLineSegment(sketch, "E1361", {"start": v(-12.3, 19.74) * mm, "end": v(-12.19, 19.6) * mm});
            skLineSegment(sketch, "E1362", {"start": v(-12.19, 19.6) * mm, "end": v(-12.07, 19.45) * mm});
            skLineSegment(sketch, "E1363", {"start": v(-12.07, 19.45) * mm, "end": v(-11.94, 19.32) * mm});
            skLineSegment(sketch, "E1364", {"start": v(-11.94, 19.32) * mm, "end": v(-11.82, 19.18) * mm});
            skLineSegment(sketch, "E1365", {"start": v(-11.82, 19.18) * mm, "end": v(-11.69, 19.05) * mm});
            skLineSegment(sketch, "E1366", {"start": v(-11.69, 19.05) * mm, "end": v(-11.56, 18.92) * mm});
            skLineSegment(sketch, "E1367", {"start": v(-11.56, 18.92) * mm, "end": v(-11.43, 18.79) * mm});
            skLineSegment(sketch, "E1368", {"start": v(-11.43, 18.79) * mm, "end": v(-11.3, 18.66) * mm});
            skLineSegment(sketch, "E1369", {"start": v(-11.3, 18.66) * mm, "end": v(-11.15, 18.54) * mm});
            skLineSegment(sketch, "E1370", {"start": v(-11.15, 18.54) * mm, "end": v(-11.01, 18.42) * mm});
            skLineSegment(sketch, "E1371", {"start": v(-11.01, 18.42) * mm, "end": v(-10.87, 18.3) * mm});
            skLineSegment(sketch, "E1372", {"start": v(-10.87, 18.3) * mm, "end": v(-10.73, 18.19) * mm});
            skLineSegment(sketch, "E1373", {"start": v(-10.73, 18.19) * mm, "end": v(-10.58, 18.08) * mm});
            skLineSegment(sketch, "E1374", {"start": v(-10.58, 18.08) * mm, "end": v(-10.43, 17.97) * mm});
            skLineSegment(sketch, "E1375", {"start": v(-10.43, 17.97) * mm, "end": v(-10.27, 17.86) * mm});
            skLineSegment(sketch, "E1376", {"start": v(-10.27, 17.86) * mm, "end": v(-10.12, 17.76) * mm});
            skLineSegment(sketch, "E1377", {"start": v(-10.12, 17.76) * mm, "end": v(-9.96, 17.67) * mm});
            skLineSegment(sketch, "E1378", {"start": v(-9.96, 17.67) * mm, "end": v(-9.8, 17.57) * mm});
            skLineSegment(sketch, "E1379", {"start": v(-9.8, 17.57) * mm, "end": v(-9.63, 17.48) * mm});
            skLineSegment(sketch, "E1380", {"start": v(-9.63, 17.48) * mm, "end": v(-9.46, 17.4) * mm});
            skLineSegment(sketch, "E1381", {"start": v(-9.46, 17.4) * mm, "end": v(-9.28, 17.32) * mm});
            skLineSegment(sketch, "E1382", {"start": v(-9.28, 17.32) * mm, "end": v(-9.1, 17.24) * mm});
            skLineSegment(sketch, "E1383", {"start": v(-9.1, 17.24) * mm, "end": v(-9.02, 17.2) * mm});
            skLineSegment(sketch, "E1384", {"start": v(-9.02, 17.2) * mm, "end": v(-8.93, 17.17) * mm});
            skLineSegment(sketch, "E1385", {"start": v(-8.93, 17.17) * mm, "end": v(-8.84, 17.14) * mm});
            skLineSegment(sketch, "E1386", {"start": v(-8.84, 17.14) * mm, "end": v(-8.76, 17.11) * mm});
            skLineSegment(sketch, "E1387", {"start": v(-8.76, 17.11) * mm, "end": v(-8.68, 17.1) * mm});
            skLineSegment(sketch, "E1388", {"start": v(-8.68, 17.1) * mm, "end": v(-8.6, 17.07) * mm});
            skLineSegment(sketch, "E1389", {"start": v(-8.6, 17.07) * mm, "end": v(-8.53, 17.06) * mm});
            skLineSegment(sketch, "E1390", {"start": v(-8.53, 17.06) * mm, "end": v(-8.45, 17.04) * mm});
            skLineSegment(sketch, "E1391", {"start": v(-8.45, 17.04) * mm, "end": v(-8.38, 17.04) * mm});
            skLineSegment(sketch, "E1392", {"start": v(-8.38, 17.04) * mm, "end": v(-8.32, 17.03) * mm});
            skLineSegment(sketch, "E1393", {"start": v(-8.32, 17.03) * mm, "end": v(-8.25, 17.03) * mm});
            skLineSegment(sketch, "E1394", {"start": v(-8.25, 17.03) * mm, "end": v(-8.19, 17.03) * mm});
            skLineSegment(sketch, "E1395", {"start": v(-8.19, 17.03) * mm, "end": v(-8.12, 17.04) * mm});
            skLineSegment(sketch, "E1396", {"start": v(-8.12, 17.04) * mm, "end": v(-8.06, 17.05) * mm});
            skLineSegment(sketch, "E1397", {"start": v(-8.06, 17.05) * mm, "end": v(-8, 17.06) * mm});
            skLineSegment(sketch, "E1398", {"start": v(-8, 17.06) * mm, "end": v(-7.95, 17.08) * mm});
            skLineSegment(sketch, "E1399", {"start": v(-7.95, 17.08) * mm, "end": v(-7.9, 17.1) * mm});
            skLineSegment(sketch, "E1400", {"start": v(-7.9, 17.1) * mm, "end": v(-7.84, 17.12) * mm});
            skLineSegment(sketch, "E1401", {"start": v(-7.84, 17.12) * mm, "end": v(-7.78, 17.15) * mm});
            skLineSegment(sketch, "E1402", {"start": v(-7.78, 17.15) * mm, "end": v(-7.73, 17.18) * mm});
            skLineSegment(sketch, "E1403", {"start": v(-7.73, 17.18) * mm, "end": v(-7.68, 17.22) * mm});
            skLineSegment(sketch, "E1404", {"start": v(-7.68, 17.22) * mm, "end": v(-7.63, 17.26) * mm});
            skLineSegment(sketch, "E1405", {"start": v(-7.63, 17.26) * mm, "end": v(-7.58, 17.3) * mm});
            skLineSegment(sketch, "E1406", {"start": v(-7.58, 17.3) * mm, "end": v(-7.54, 17.35) * mm});
            skLineSegment(sketch, "E1407", {"start": v(-7.54, 17.35) * mm, "end": v(-7.5, 17.4) * mm});
            skLineSegment(sketch, "E1408", {"start": v(-7.5, 17.4) * mm, "end": v(-7.45, 17.46) * mm});
            skLineSegment(sketch, "E1409", {"start": v(-7.45, 17.46) * mm, "end": v(-7.4, 17.51) * mm});
            skLineSegment(sketch, "E1410", {"start": v(-7.4, 17.51) * mm, "end": v(-7.36, 17.58) * mm});
            skLineSegment(sketch, "E1411", {"start": v(-7.36, 17.58) * mm, "end": v(-7.32, 17.64) * mm});
            skLineSegment(sketch, "E1412", {"start": v(-7.32, 17.64) * mm, "end": v(-7.27, 17.71) * mm});
            skLineSegment(sketch, "E1413", {"start": v(-7.27, 17.71) * mm, "end": v(-7.23, 17.79) * mm});
            skLineSegment(sketch, "E1414", {"start": v(-7.23, 17.79) * mm, "end": v(-7.19, 17.87) * mm});
            skLineSegment(sketch, "E1415", {"start": v(-7.19, 17.87) * mm, "end": v(-7.17, 17.9) * mm});
            skLineSegment(sketch, "E1416", {"start": v(-7.17, 17.9) * mm, "end": v(-7.15, 17.95) * mm});
            skLineSegment(sketch, "E1417", {"start": v(-7.15, 17.95) * mm, "end": v(-7.12, 18) * mm});
            skLineSegment(sketch, "E1418", {"start": v(-7.12, 18) * mm, "end": v(-7.1, 18.04) * mm});
            skLineSegment(sketch, "E1419", {"start": v(-7.1, 18.04) * mm, "end": v(-7.08, 18.08) * mm});
            skLineSegment(sketch, "E1420", {"start": v(-7.08, 18.08) * mm, "end": v(-7.06, 18.13) * mm});
            skLineSegment(sketch, "E1421", {"start": v(-7.06, 18.13) * mm, "end": v(-7.04, 18.17) * mm});
            skLineSegment(sketch, "E1422", {"start": v(-7.04, 18.17) * mm, "end": v(-7.02, 18.22) * mm});
            skLineSegment(sketch, "E1423", {"start": v(-7.02, 18.22) * mm, "end": v(-7, 18.26) * mm});
            skLineSegment(sketch, "E1424", {"start": v(-7, 18.26) * mm, "end": v(-6.98, 18.3) * mm});
            skLineSegment(sketch, "E1425", {"start": v(-6.98, 18.3) * mm, "end": v(-6.96, 18.35) * mm});
            skLineSegment(sketch, "E1426", {"start": v(-6.96, 18.35) * mm, "end": v(-6.94, 18.4) * mm});
            skLineSegment(sketch, "E1427", {"start": v(-6.94, 18.4) * mm, "end": v(-6.92, 18.44) * mm});
            skLineSegment(sketch, "E1428", {"start": v(-6.92, 18.44) * mm, "end": v(-6.9, 18.48) * mm});
            skLineSegment(sketch, "E1429", {"start": v(-6.9, 18.48) * mm, "end": v(-6.88, 18.53) * mm});
            skLineSegment(sketch, "E1430", {"start": v(-6.88, 18.53) * mm, "end": v(-6.86, 18.57) * mm});
            skLineSegment(sketch, "E1431", {"start": v(-6.86, 18.57) * mm, "end": v(-6.84, 18.62) * mm});
            skLineSegment(sketch, "E1432", {"start": v(-6.84, 18.62) * mm, "end": v(-6.82, 18.66) * mm});
            skLineSegment(sketch, "E1433", {"start": v(-6.82, 18.66) * mm, "end": v(-6.8, 18.7) * mm});
            skLineSegment(sketch, "E1434", {"start": v(-6.8, 18.7) * mm, "end": v(-6.78, 18.75) * mm});
            skLineSegment(sketch, "E1435", {"start": v(-6.78, 18.75) * mm, "end": v(-6.76, 18.8) * mm});
            skLineSegment(sketch, "E1436", {"start": v(-6.76, 18.8) * mm, "end": v(-6.74, 18.84) * mm});
            skLineSegment(sketch, "E1437", {"start": v(-6.74, 18.84) * mm, "end": v(-6.73, 18.89) * mm});
            skLineSegment(sketch, "E1438", {"start": v(-6.73, 18.89) * mm, "end": v(-6.7, 18.93) * mm});
            skLineSegment(sketch, "E1439", {"start": v(-6.7, 18.93) * mm, "end": v(-6.7, 18.98) * mm});
            skLineSegment(sketch, "E1440", {"start": v(-6.7, 18.98) * mm, "end": v(-6.67, 19.02) * mm});
            skLineSegment(sketch, "E1441", {"start": v(-6.67, 19.02) * mm, "end": v(-6.66, 19.07) * mm});
            skLineSegment(sketch, "E1442", {"start": v(-6.66, 19.07) * mm, "end": v(-6.64, 19.12) * mm});
            skLineSegment(sketch, "E1443", {"start": v(-6.64, 19.12) * mm, "end": v(-6.62, 19.16) * mm});
            skLineSegment(sketch, "E1444", {"start": v(-6.62, 19.16) * mm, "end": v(-6.6, 19.2) * mm});
            skLineSegment(sketch, "E1445", {"start": v(-6.6, 19.2) * mm, "end": v(-6.59, 19.25) * mm});
            skLineSegment(sketch, "E1446", {"start": v(-6.59, 19.25) * mm, "end": v(-6.57, 19.3) * mm});
            skLineSegment(sketch, "E1447", {"start": v(-6.57, 19.3) * mm, "end": v(-6.54, 19.38) * mm});
            skLineSegment(sketch, "E1448", {"start": v(-6.54, 19.38) * mm, "end": v(-6.51, 19.46) * mm});
            skLineSegment(sketch, "E1449", {"start": v(-6.51, 19.46) * mm, "end": v(-6.49, 19.55) * mm});
            skLineSegment(sketch, "E1450", {"start": v(-6.49, 19.55) * mm, "end": v(-6.46, 19.63) * mm});
            skLineSegment(sketch, "E1451", {"start": v(-6.46, 19.63) * mm, "end": v(-6.43, 19.71) * mm});
            skLineSegment(sketch, "E1452", {"start": v(-6.43, 19.71) * mm, "end": v(-6.4, 19.8) * mm});
            skLineSegment(sketch, "E1453", {"start": v(-6.4, 19.8) * mm, "end": v(-6.37, 19.88) * mm});
            skLineSegment(sketch, "E1454", {"start": v(-6.37, 19.88) * mm, "end": v(-6.34, 19.96) * mm});
            skLineSegment(sketch, "E1455", {"start": v(-6.34, 19.96) * mm, "end": v(-6.32, 20.05) * mm});
            skLineSegment(sketch, "E1456", {"start": v(-6.32, 20.05) * mm, "end": v(-6.29, 20.13) * mm});
            skLineSegment(sketch, "E1457", {"start": v(-6.29, 20.13) * mm, "end": v(-6.26, 20.21) * mm});
            skLineSegment(sketch, "E1458", {"start": v(-6.26, 20.21) * mm, "end": v(-6.23, 20.3) * mm});
            skLineSegment(sketch, "E1459", {"start": v(-6.23, 20.3) * mm, "end": v(-6.2, 20.38) * mm});
            skLineSegment(sketch, "E1460", {"start": v(-6.2, 20.38) * mm, "end": v(-6.18, 20.47) * mm});
            skLineSegment(sketch, "E1461", {"start": v(-6.18, 20.47) * mm, "end": v(-6.15, 20.55) * mm});
            skLineSegment(sketch, "E1462", {"start": v(-6.15, 20.55) * mm, "end": v(-6.12, 20.64) * mm});
            skLineSegment(sketch, "E1463", {"start": v(-6.12, 20.64) * mm, "end": v(-6.1, 20.72) * mm});
            skLineSegment(sketch, "E1464", {"start": v(-6.1, 20.72) * mm, "end": v(-6.07, 20.8) * mm});
            skLineSegment(sketch, "E1465", {"start": v(-6.07, 20.8) * mm, "end": v(-6.04, 20.9) * mm});
            skLineSegment(sketch, "E1466", {"start": v(-6.04, 20.9) * mm, "end": v(-6.01, 20.98) * mm});
            skLineSegment(sketch, "E1467", {"start": v(-6.01, 20.98) * mm, "end": v(-5.98, 21.07) * mm});
            skLineSegment(sketch, "E1468", {"start": v(-5.98, 21.07) * mm, "end": v(-5.96, 21.15) * mm});
            skLineSegment(sketch, "E1469", {"start": v(-5.96, 21.15) * mm, "end": v(-5.93, 21.24) * mm});
            skLineSegment(sketch, "E1470", {"start": v(-5.93, 21.24) * mm, "end": v(-5.9, 21.33) * mm});
            skLineSegment(sketch, "E1471", {"start": v(-5.9, 21.33) * mm, "end": v(-5.87, 21.42) * mm});
            skLineSegment(sketch, "E1472", {"start": v(-5.87, 21.42) * mm, "end": v(-5.84, 21.5) * mm});
            skLineSegment(sketch, "E1473", {"start": v(-5.84, 21.5) * mm, "end": v(-5.81, 21.6) * mm});
            skLineSegment(sketch, "E1474", {"start": v(-5.81, 21.6) * mm, "end": v(-5.78, 21.69) * mm});
            skLineSegment(sketch, "E1475", {"start": v(-5.78, 21.69) * mm, "end": v(-5.75, 21.78) * mm});
            skLineSegment(sketch, "E1476", {"start": v(-5.75, 21.78) * mm, "end": v(-5.72, 21.87) * mm});
            skLineSegment(sketch, "E1477", {"start": v(-5.72, 21.87) * mm, "end": v(-5.7, 21.96) * mm});
            skLineSegment(sketch, "E1478", {"start": v(-5.7, 21.96) * mm, "end": v(-5.66, 22.05) * mm});
            skLineSegment(sketch, "E1479", {"start": v(6, 40.03) * mm, "end": v(6.4, 39.91) * mm});
            skLineSegment(sketch, "E1480", {"start": v(6.4, 39.91) * mm, "end": v(6.8, 39.8) * mm});
            skLineSegment(sketch, "E1481", {"start": v(6.8, 39.8) * mm, "end": v(7.2, 39.67) * mm});
            skLineSegment(sketch, "E1482", {"start": v(7.2, 39.67) * mm, "end": v(7.6, 39.55) * mm});
            skLineSegment(sketch, "E1483", {"start": v(7.6, 39.55) * mm, "end": v(7.98, 39.42) * mm});
            skLineSegment(sketch, "E1484", {"start": v(7.98, 39.42) * mm, "end": v(8.37, 39.3) * mm});
            skLineSegment(sketch, "E1485", {"start": v(8.37, 39.3) * mm, "end": v(8.76, 39.16) * mm});
            skLineSegment(sketch, "E1486", {"start": v(8.76, 39.16) * mm, "end": v(9.14, 39.02) * mm});
            skLineSegment(sketch, "E1487", {"start": v(9.14, 39.02) * mm, "end": v(9.52, 38.87) * mm});
            skLineSegment(sketch, "E1488", {"start": v(9.52, 38.87) * mm, "end": v(9.9, 38.72) * mm});
            skLineSegment(sketch, "E1489", {"start": v(9.9, 38.72) * mm, "end": v(10.26, 38.57) * mm});
            skLineSegment(sketch, "E1490", {"start": v(10.26, 38.57) * mm, "end": v(10.63, 38.4) * mm});
            skLineSegment(sketch, "E1491", {"start": v(10.63, 38.4) * mm, "end": v(10.99, 38.23) * mm});
            skLineSegment(sketch, "E1492", {"start": v(10.99, 38.23) * mm, "end": v(11.34, 38.06) * mm});
            skLineSegment(sketch, "E1493", {"start": v(11.34, 38.06) * mm, "end": v(11.7, 37.87) * mm});
            skLineSegment(sketch, "E1494", {"start": v(11.7, 37.87) * mm, "end": v(12.04, 37.68) * mm});
            skLineSegment(sketch, "E1495", {"start": v(12.04, 37.68) * mm, "end": v(12.38, 37.48) * mm});
            skLineSegment(sketch, "E1496", {"start": v(12.38, 37.48) * mm, "end": v(12.72, 37.27) * mm});
            skLineSegment(sketch, "E1497", {"start": v(12.72, 37.27) * mm, "end": v(13.04, 37.05) * mm});
            skLineSegment(sketch, "E1498", {"start": v(13.04, 37.05) * mm, "end": v(13.37, 36.81) * mm});
            skLineSegment(sketch, "E1499", {"start": v(13.37, 36.81) * mm, "end": v(13.68, 36.57) * mm});
            skLineSegment(sketch, "E1500", {"start": v(13.68, 36.57) * mm, "end": v(14, 36.32) * mm});
            skLineSegment(sketch, "E1501", {"start": v(14, 36.32) * mm, "end": v(14.3, 36.06) * mm});
            skLineSegment(sketch, "E1502", {"start": v(14.3, 36.06) * mm, "end": v(14.6, 35.78) * mm});
            skLineSegment(sketch, "E1503", {"start": v(14.6, 35.78) * mm, "end": v(14.88, 35.5) * mm});
            skLineSegment(sketch, "E1504", {"start": v(14.88, 35.5) * mm, "end": v(15.16, 35.2) * mm});
            skLineSegment(sketch, "E1505", {"start": v(15.16, 35.2) * mm, "end": v(15.44, 34.88) * mm});
            skLineSegment(sketch, "E1506", {"start": v(15.44, 34.88) * mm, "end": v(15.7, 34.56) * mm});
            skLineSegment(sketch, "E1507", {"start": v(15.7, 34.56) * mm, "end": v(15.96, 34.22) * mm});
            skLineSegment(sketch, "E1508", {"start": v(15.96, 34.22) * mm, "end": v(16.21, 33.86) * mm});
            skLineSegment(sketch, "E1509", {"start": v(16.21, 33.86) * mm, "end": v(16.45, 33.5) * mm});
            skLineSegment(sketch, "E1510", {"start": v(16.45, 33.5) * mm, "end": v(16.69, 33.1) * mm});
            skLineSegment(sketch, "E1511", {"start": v(16.69, 33.1) * mm, "end": v(16.67, 33.2) * mm});
            skLineSegment(sketch, "E1512", {"start": v(16.67, 33.2) * mm, "end": v(16.65, 33.3) * mm});
            skLineSegment(sketch, "E1513", {"start": v(16.65, 33.3) * mm, "end": v(16.63, 33.38) * mm});
            skLineSegment(sketch, "E1514", {"start": v(16.63, 33.38) * mm, "end": v(16.6, 33.47) * mm});
            skLineSegment(sketch, "E1515", {"start": v(16.6, 33.47) * mm, "end": v(16.59, 33.56) * mm});
            skLineSegment(sketch, "E1516", {"start": v(16.59, 33.56) * mm, "end": v(16.57, 33.65) * mm});
            skLineSegment(sketch, "E1517", {"start": v(16.57, 33.65) * mm, "end": v(16.55, 33.73) * mm});
            skLineSegment(sketch, "E1518", {"start": v(16.55, 33.73) * mm, "end": v(16.54, 33.82) * mm});
            skLineSegment(sketch, "E1519", {"start": v(16.54, 33.82) * mm, "end": v(16.52, 33.9) * mm});
            skLineSegment(sketch, "E1520", {"start": v(16.52, 33.9) * mm, "end": v(16.5, 33.99) * mm});
            skLineSegment(sketch, "E1521", {"start": v(16.5, 33.99) * mm, "end": v(16.48, 34.07) * mm});
            skLineSegment(sketch, "E1522", {"start": v(16.48, 34.07) * mm, "end": v(16.47, 34.15) * mm});
            skLineSegment(sketch, "E1523", {"start": v(16.47, 34.15) * mm, "end": v(16.45, 34.23) * mm});
            skLineSegment(sketch, "E1524", {"start": v(16.45, 34.23) * mm, "end": v(16.43, 34.32) * mm});
            skLineSegment(sketch, "E1525", {"start": v(16.43, 34.32) * mm, "end": v(16.42, 34.4) * mm});
            skLineSegment(sketch, "E1526", {"start": v(16.42, 34.4) * mm, "end": v(16.4, 34.48) * mm});
            skLineSegment(sketch, "E1527", {"start": v(16.4, 34.48) * mm, "end": v(16.38, 34.56) * mm});
            skLineSegment(sketch, "E1528", {"start": v(16.38, 34.56) * mm, "end": v(16.37, 34.63) * mm});
            skLineSegment(sketch, "E1529", {"start": v(16.37, 34.63) * mm, "end": v(16.35, 34.71) * mm});
            skLineSegment(sketch, "E1530", {"start": v(16.35, 34.71) * mm, "end": v(16.33, 34.8) * mm});
            skLineSegment(sketch, "E1531", {"start": v(16.33, 34.8) * mm, "end": v(16.32, 34.87) * mm});
            skLineSegment(sketch, "E1532", {"start": v(16.32, 34.87) * mm, "end": v(16.3, 34.94) * mm});
            skLineSegment(sketch, "E1533", {"start": v(16.3, 34.94) * mm, "end": v(16.28, 35.02) * mm});
            skLineSegment(sketch, "E1534", {"start": v(16.28, 35.02) * mm, "end": v(16.26, 35.1) * mm});
            skLineSegment(sketch, "E1535", {"start": v(16.26, 35.1) * mm, "end": v(16.24, 35.17) * mm});
            skLineSegment(sketch, "E1536", {"start": v(16.24, 35.17) * mm, "end": v(16.23, 35.25) * mm});
            skLineSegment(sketch, "E1537", {"start": v(16.23, 35.25) * mm, "end": v(16.2, 35.32) * mm});
            skLineSegment(sketch, "E1538", {"start": v(16.2, 35.32) * mm, "end": v(16.19, 35.4) * mm});
            skLineSegment(sketch, "E1539", {"start": v(16.19, 35.4) * mm, "end": v(16.17, 35.47) * mm});
            skLineSegment(sketch, "E1540", {"start": v(16.17, 35.47) * mm, "end": v(16.15, 35.55) * mm});
            skLineSegment(sketch, "E1541", {"start": v(16.15, 35.55) * mm, "end": v(16.13, 35.62) * mm});
            skLineSegment(sketch, "E1542", {"start": v(16.13, 35.62) * mm, "end": v(16.1, 35.7) * mm});
            skLineSegment(sketch, "E1543", {"start": v(16.1, 35.7) * mm, "end": v(16.02, 36) * mm});
            skLineSegment(sketch, "E1544", {"start": v(16.02, 36) * mm, "end": v(15.92, 36.32) * mm});
            skLineSegment(sketch, "E1545", {"start": v(15.92, 36.32) * mm, "end": v(15.81, 36.63) * mm});
            skLineSegment(sketch, "E1546", {"start": v(15.81, 36.63) * mm, "end": v(15.7, 36.93) * mm});
            skLineSegment(sketch, "E1547", {"start": v(15.7, 36.93) * mm, "end": v(15.59, 37.23) * mm});
            skLineSegment(sketch, "E1548", {"start": v(15.59, 37.23) * mm, "end": v(15.47, 37.53) * mm});
            skLineSegment(sketch, "E1549", {"start": v(15.47, 37.53) * mm, "end": v(15.34, 37.82) * mm});
            skLineSegment(sketch, "E1550", {"start": v(15.34, 37.82) * mm, "end": v(15.21, 38.11) * mm});
            skLineSegment(sketch, "E1551", {"start": v(15.21, 38.11) * mm, "end": v(15.07, 38.4) * mm});
            skLineSegment(sketch, "E1552", {"start": v(15.07, 38.4) * mm, "end": v(14.93, 38.68) * mm});
            skLineSegment(sketch, "E1553", {"start": v(14.93, 38.68) * mm, "end": v(14.78, 38.96) * mm});
            skLineSegment(sketch, "E1554", {"start": v(14.78, 38.96) * mm, "end": v(14.63, 39.24) * mm});
            skLineSegment(sketch, "E1555", {"start": v(14.63, 39.24) * mm, "end": v(14.47, 39.5) * mm});
            skLineSegment(sketch, "E1556", {"start": v(14.47, 39.5) * mm, "end": v(14.3, 39.78) * mm});
            skLineSegment(sketch, "E1557", {"start": v(14.3, 39.78) * mm, "end": v(14.14, 40.04) * mm});
            skLineSegment(sketch, "E1558", {"start": v(14.14, 40.04) * mm, "end": v(13.97, 40.3) * mm});
            skLineSegment(sketch, "E1559", {"start": v(13.97, 40.3) * mm, "end": v(13.8, 40.57) * mm});
            skLineSegment(sketch, "E1560", {"start": v(13.8, 40.57) * mm, "end": v(13.6, 40.82) * mm});
            skLineSegment(sketch, "E1561", {"start": v(13.6, 40.82) * mm, "end": v(13.42, 41.08) * mm});
            skLineSegment(sketch, "E1562", {"start": v(13.42, 41.08) * mm, "end": v(13.23, 41.33) * mm});
            skLineSegment(sketch, "E1563", {"start": v(13.23, 41.33) * mm, "end": v(13.03, 41.57) * mm});
            skLineSegment(sketch, "E1564", {"start": v(13.03, 41.57) * mm, "end": v(12.83, 41.82) * mm});
            skLineSegment(sketch, "E1565", {"start": v(12.83, 41.82) * mm, "end": v(12.63, 42.06) * mm});
            skLineSegment(sketch, "E1566", {"start": v(12.63, 42.06) * mm, "end": v(12.42, 42.3) * mm});
            skLineSegment(sketch, "E1567", {"start": v(12.42, 42.3) * mm, "end": v(12.2, 42.53) * mm});
            skLineSegment(sketch, "E1568", {"start": v(12.2, 42.53) * mm, "end": v(11.98, 42.76) * mm});
            skLineSegment(sketch, "E1569", {"start": v(11.98, 42.76) * mm, "end": v(11.76, 43) * mm});
            skLineSegment(sketch, "E1570", {"start": v(11.76, 43) * mm, "end": v(11.53, 43.22) * mm});
            skLineSegment(sketch, "E1571", {"start": v(11.53, 43.22) * mm, "end": v(11.3, 43.44) * mm});
            skLineSegment(sketch, "E1572", {"start": v(11.3, 43.44) * mm, "end": v(11.07, 43.66) * mm});
            skLineSegment(sketch, "E1573", {"start": v(11.07, 43.66) * mm, "end": v(10.83, 43.88) * mm});
            skLineSegment(sketch, "E1574", {"start": v(10.83, 43.88) * mm, "end": v(10.58, 44.09) * mm});
            skLineSegment(sketch, "E1575", {"start": v(10.58, 44.09) * mm, "end": v(10.49, 44.17) * mm});
            skLineSegment(sketch, "E1576", {"start": v(10.49, 44.17) * mm, "end": v(10.39, 44.25) * mm});
            skLineSegment(sketch, "E1577", {"start": v(10.39, 44.25) * mm, "end": v(10.29, 44.33) * mm});
            skLineSegment(sketch, "E1578", {"start": v(10.29, 44.33) * mm, "end": v(10.2, 44.4) * mm});
            skLineSegment(sketch, "E1579", {"start": v(10.2, 44.4) * mm, "end": v(10.1, 44.47) * mm});
            skLineSegment(sketch, "E1580", {"start": v(10.1, 44.47) * mm, "end": v(10, 44.53) * mm});
            skLineSegment(sketch, "E1581", {"start": v(10, 44.53) * mm, "end": v(9.9, 44.58) * mm});
            skLineSegment(sketch, "E1582", {"start": v(9.9, 44.58) * mm, "end": v(9.8, 44.64) * mm});
            skLineSegment(sketch, "E1583", {"start": v(9.8, 44.64) * mm, "end": v(9.7, 44.68) * mm});
            skLineSegment(sketch, "E1584", {"start": v(9.7, 44.68) * mm, "end": v(9.61, 44.72) * mm});
            skLineSegment(sketch, "E1585", {"start": v(9.61, 44.72) * mm, "end": v(9.51, 44.76) * mm});
            skLineSegment(sketch, "E1586", {"start": v(9.51, 44.76) * mm, "end": v(9.42, 44.78) * mm});
            skLineSegment(sketch, "E1587", {"start": v(9.42, 44.78) * mm, "end": v(9.32, 44.8) * mm});
            skLineSegment(sketch, "E1588", {"start": v(9.32, 44.8) * mm, "end": v(9.23, 44.82) * mm});
            skLineSegment(sketch, "E1589", {"start": v(9.23, 44.82) * mm, "end": v(9.14, 44.83) * mm});
            skLineSegment(sketch, "E1590", {"start": v(9.14, 44.83) * mm, "end": v(9.04, 44.83) * mm});
            skLineSegment(sketch, "E1591", {"start": v(9.04, 44.83) * mm, "end": v(8.95, 44.83) * mm});
            skLineSegment(sketch, "E1592", {"start": v(8.95, 44.83) * mm, "end": v(8.86, 44.81) * mm});
            skLineSegment(sketch, "E1593", {"start": v(8.86, 44.81) * mm, "end": v(8.77, 44.8) * mm});
            skLineSegment(sketch, "E1594", {"start": v(8.77, 44.8) * mm, "end": v(8.67, 44.76) * mm});
            skLineSegment(sketch, "E1595", {"start": v(8.67, 44.76) * mm, "end": v(8.58, 44.72) * mm});
            skLineSegment(sketch, "E1596", {"start": v(8.58, 44.72) * mm, "end": v(8.5, 44.68) * mm});
            skLineSegment(sketch, "E1597", {"start": v(8.5, 44.68) * mm, "end": v(8.4, 44.63) * mm});
            skLineSegment(sketch, "E1598", {"start": v(8.4, 44.63) * mm, "end": v(8.32, 44.56) * mm});
            skLineSegment(sketch, "E1599", {"start": v(8.32, 44.56) * mm, "end": v(8.23, 44.5) * mm});
            skLineSegment(sketch, "E1600", {"start": v(8.23, 44.5) * mm, "end": v(8.14, 44.4) * mm});
            skLineSegment(sketch, "E1601", {"start": v(8.14, 44.4) * mm, "end": v(8.05, 44.32) * mm});
            skLineSegment(sketch, "E1602", {"start": v(8.05, 44.32) * mm, "end": v(7.97, 44.22) * mm});
            skLineSegment(sketch, "E1603", {"start": v(7.97, 44.22) * mm, "end": v(7.88, 44.1) * mm});
            skLineSegment(sketch, "E1604", {"start": v(7.88, 44.1) * mm, "end": v(7.8, 43.99) * mm});
            skLineSegment(sketch, "E1605", {"start": v(7.8, 43.99) * mm, "end": v(7.71, 43.86) * mm});
            skLineSegment(sketch, "E1606", {"start": v(7.71, 43.86) * mm, "end": v(7.63, 43.72) * mm});
            skLineSegment(sketch, "E1607", {"start": v(7.63, 43.72) * mm, "end": v(7.57, 43.6) * mm});
            skLineSegment(sketch, "E1608", {"start": v(7.57, 43.6) * mm, "end": v(7.5, 43.5) * mm});
            skLineSegment(sketch, "E1609", {"start": v(7.5, 43.5) * mm, "end": v(7.45, 43.39) * mm});
            skLineSegment(sketch, "E1610", {"start": v(7.45, 43.39) * mm, "end": v(7.4, 43.28) * mm});
            skLineSegment(sketch, "E1611", {"start": v(7.4, 43.28) * mm, "end": v(7.33, 43.17) * mm});
            skLineSegment(sketch, "E1612", {"start": v(7.33, 43.17) * mm, "end": v(7.28, 43.06) * mm});
            skLineSegment(sketch, "E1613", {"start": v(7.28, 43.06) * mm, "end": v(7.22, 42.94) * mm});
            skLineSegment(sketch, "E1614", {"start": v(7.22, 42.94) * mm, "end": v(7.17, 42.83) * mm});
            skLineSegment(sketch, "E1615", {"start": v(7.17, 42.83) * mm, "end": v(7.12, 42.72) * mm});
            skLineSegment(sketch, "E1616", {"start": v(7.12, 42.72) * mm, "end": v(7.07, 42.6) * mm});
            skLineSegment(sketch, "E1617", {"start": v(7.07, 42.6) * mm, "end": v(7.01, 42.49) * mm});
            skLineSegment(sketch, "E1618", {"start": v(7.01, 42.49) * mm, "end": v(6.96, 42.37) * mm});
            skLineSegment(sketch, "E1619", {"start": v(6.96, 42.37) * mm, "end": v(6.91, 42.26) * mm});
            skLineSegment(sketch, "E1620", {"start": v(6.91, 42.26) * mm, "end": v(6.86, 42.14) * mm});
            skLineSegment(sketch, "E1621", {"start": v(6.86, 42.14) * mm, "end": v(6.82, 42.02) * mm});
            skLineSegment(sketch, "E1622", {"start": v(6.82, 42.02) * mm, "end": v(6.77, 41.9) * mm});
            skLineSegment(sketch, "E1623", {"start": v(6.77, 41.9) * mm, "end": v(6.72, 41.8) * mm});
            skLineSegment(sketch, "E1624", {"start": v(6.72, 41.8) * mm, "end": v(6.67, 41.67) * mm});
            skLineSegment(sketch, "E1625", {"start": v(6.67, 41.67) * mm, "end": v(6.62, 41.56) * mm});
            skLineSegment(sketch, "E1626", {"start": v(6.62, 41.56) * mm, "end": v(6.58, 41.44) * mm});
            skLineSegment(sketch, "E1627", {"start": v(6.58, 41.44) * mm, "end": v(6.53, 41.32) * mm});
            skLineSegment(sketch, "E1628", {"start": v(6.53, 41.32) * mm, "end": v(6.48, 41.2) * mm});
            skLineSegment(sketch, "E1629", {"start": v(6.48, 41.2) * mm, "end": v(6.43, 41.09) * mm});
            skLineSegment(sketch, "E1630", {"start": v(6.43, 41.09) * mm, "end": v(6.39, 40.97) * mm});
            skLineSegment(sketch, "E1631", {"start": v(6.39, 40.97) * mm, "end": v(6.34, 40.85) * mm});
            skLineSegment(sketch, "E1632", {"start": v(6.34, 40.85) * mm, "end": v(6.3, 40.73) * mm});
            skLineSegment(sketch, "E1633", {"start": v(6.3, 40.73) * mm, "end": v(6.24, 40.62) * mm});
            skLineSegment(sketch, "E1634", {"start": v(6.24, 40.62) * mm, "end": v(6.2, 40.5) * mm});
            skLineSegment(sketch, "E1635", {"start": v(6.2, 40.5) * mm, "end": v(6.14, 40.38) * mm});
            skLineSegment(sketch, "E1636", {"start": v(6.14, 40.38) * mm, "end": v(6.1, 40.26) * mm});
            skLineSegment(sketch, "E1637", {"start": v(6.1, 40.26) * mm, "end": v(6.05, 40.15) * mm});
            skLineSegment(sketch, "E1638", {"start": v(6.05, 40.15) * mm, "end": v(6, 40.03) * mm});
            skLineSegment(sketch, "E1639", {"start": v(16.58, 28.71) * mm, "end": v(16.57, 28.52) * mm});
            skLineSegment(sketch, "E1640", {"start": v(16.57, 28.52) * mm, "end": v(16.55, 28.33) * mm});
            skLineSegment(sketch, "E1641", {"start": v(16.55, 28.33) * mm, "end": v(16.53, 28.13) * mm});
            skLineSegment(sketch, "E1642", {"start": v(16.53, 28.13) * mm, "end": v(16.51, 27.94) * mm});
            skLineSegment(sketch, "E1643", {"start": v(16.51, 27.94) * mm, "end": v(16.49, 27.75) * mm});
            skLineSegment(sketch, "E1644", {"start": v(16.49, 27.75) * mm, "end": v(16.46, 27.55) * mm});
            skLineSegment(sketch, "E1645", {"start": v(16.46, 27.55) * mm, "end": v(16.43, 27.36) * mm});
            skLineSegment(sketch, "E1646", {"start": v(16.43, 27.36) * mm, "end": v(16.4, 27.17) * mm});
            skLineSegment(sketch, "E1647", {"start": v(16.4, 27.17) * mm, "end": v(16.36, 26.97) * mm});
            skLineSegment(sketch, "E1648", {"start": v(16.36, 26.97) * mm, "end": v(16.32, 26.78) * mm});
            skLineSegment(sketch, "E1649", {"start": v(16.32, 26.78) * mm, "end": v(16.28, 26.59) * mm});
            skLineSegment(sketch, "E1650", {"start": v(16.28, 26.59) * mm, "end": v(16.23, 26.4) * mm});
            skLineSegment(sketch, "E1651", {"start": v(16.23, 26.4) * mm, "end": v(16.19, 26.2) * mm});
            skLineSegment(sketch, "E1652", {"start": v(16.19, 26.2) * mm, "end": v(16.14, 26) * mm});
            skLineSegment(sketch, "E1653", {"start": v(16.14, 26) * mm, "end": v(16.08, 25.82) * mm});
            skLineSegment(sketch, "E1654", {"start": v(16.08, 25.82) * mm, "end": v(16.03, 25.62) * mm});
            skLineSegment(sketch, "E1655", {"start": v(16.03, 25.62) * mm, "end": v(15.97, 25.43) * mm});
            skLineSegment(sketch, "E1656", {"start": v(15.97, 25.43) * mm, "end": v(15.91, 25.24) * mm});
            skLineSegment(sketch, "E1657", {"start": v(15.91, 25.24) * mm, "end": v(15.85, 25.05) * mm});
            skLineSegment(sketch, "E1658", {"start": v(15.85, 25.05) * mm, "end": v(15.78, 24.86) * mm});
            skLineSegment(sketch, "E1659", {"start": v(15.78, 24.86) * mm, "end": v(15.71, 24.67) * mm});
            skLineSegment(sketch, "E1660", {"start": v(15.71, 24.67) * mm, "end": v(15.64, 24.48) * mm});
            skLineSegment(sketch, "E1661", {"start": v(15.64, 24.48) * mm, "end": v(15.57, 24.29) * mm});
            skLineSegment(sketch, "E1662", {"start": v(15.57, 24.29) * mm, "end": v(15.5, 24.1) * mm});
            skLineSegment(sketch, "E1663", {"start": v(15.5, 24.1) * mm, "end": v(15.41, 23.91) * mm});
            skLineSegment(sketch, "E1664", {"start": v(15.41, 23.91) * mm, "end": v(15.33, 23.72) * mm});
            skLineSegment(sketch, "E1665", {"start": v(15.33, 23.72) * mm, "end": v(15.24, 23.54) * mm});
            skLineSegment(sketch, "E1666", {"start": v(15.24, 23.54) * mm, "end": v(15.16, 23.35) * mm});
            skLineSegment(sketch, "E1667", {"start": v(15.16, 23.35) * mm, "end": v(15.07, 23.16) * mm});
            skLineSegment(sketch, "E1668", {"start": v(15.07, 23.16) * mm, "end": v(14.97, 22.98) * mm});
            skLineSegment(sketch, "E1669", {"start": v(14.97, 22.98) * mm, "end": v(14.88, 22.8) * mm});
            skLineSegment(sketch, "E1670", {"start": v(14.88, 22.8) * mm, "end": v(14.78, 22.61) * mm});
            skLineSegment(sketch, "E1671", {"start": v(14.78, 22.61) * mm, "end": v(14.65, 22.38) * mm});
            skLineSegment(sketch, "E1672", {"start": v(14.65, 22.38) * mm, "end": v(14.52, 22.16) * mm});
            skLineSegment(sketch, "E1673", {"start": v(14.52, 22.16) * mm, "end": v(14.4, 21.94) * mm});
            skLineSegment(sketch, "E1674", {"start": v(14.4, 21.94) * mm, "end": v(14.26, 21.72) * mm});
            skLineSegment(sketch, "E1675", {"start": v(14.26, 21.72) * mm, "end": v(14.12, 21.5) * mm});
            skLineSegment(sketch, "E1676", {"start": v(14.12, 21.5) * mm, "end": v(13.98, 21.3) * mm});
            skLineSegment(sketch, "E1677", {"start": v(13.98, 21.3) * mm, "end": v(13.83, 21.08) * mm});
            skLineSegment(sketch, "E1678", {"start": v(13.83, 21.08) * mm, "end": v(13.69, 20.88) * mm});
            skLineSegment(sketch, "E1679", {"start": v(13.69, 20.88) * mm, "end": v(13.54, 20.67) * mm});
            skLineSegment(sketch, "E1680", {"start": v(13.54, 20.67) * mm, "end": v(13.38, 20.47) * mm});
            skLineSegment(sketch, "E1681", {"start": v(13.38, 20.47) * mm, "end": v(13.23, 20.27) * mm});
            skLineSegment(sketch, "E1682", {"start": v(13.23, 20.27) * mm, "end": v(13.07, 20.08) * mm});
            skLineSegment(sketch, "E1683", {"start": v(13.07, 20.08) * mm, "end": v(12.9, 19.89) * mm});
            skLineSegment(sketch, "E1684", {"start": v(12.9, 19.89) * mm, "end": v(12.74, 19.7) * mm});
            skLineSegment(sketch, "E1685", {"start": v(12.74, 19.7) * mm, "end": v(12.57, 19.51) * mm});
            skLineSegment(sketch, "E1686", {"start": v(12.57, 19.51) * mm, "end": v(12.4, 19.33) * mm});
            skLineSegment(sketch, "E1687", {"start": v(12.4, 19.33) * mm, "end": v(12.23, 19.15) * mm});
            skLineSegment(sketch, "E1688", {"start": v(12.23, 19.15) * mm, "end": v(12.05, 18.97) * mm});
            skLineSegment(sketch, "E1689", {"start": v(12.05, 18.97) * mm, "end": v(11.87, 18.8) * mm});
            skLineSegment(sketch, "E1690", {"start": v(11.87, 18.8) * mm, "end": v(11.68, 18.63) * mm});
            skLineSegment(sketch, "E1691", {"start": v(11.68, 18.63) * mm, "end": v(11.5, 18.46) * mm});
            skLineSegment(sketch, "E1692", {"start": v(11.5, 18.46) * mm, "end": v(11.3, 18.3) * mm});
            skLineSegment(sketch, "E1693", {"start": v(11.3, 18.3) * mm, "end": v(11.11, 18.13) * mm});
            skLineSegment(sketch, "E1694", {"start": v(11.11, 18.13) * mm, "end": v(10.92, 17.97) * mm});
            skLineSegment(sketch, "E1695", {"start": v(10.92, 17.97) * mm, "end": v(10.72, 17.81) * mm});
            skLineSegment(sketch, "E1696", {"start": v(10.72, 17.81) * mm, "end": v(10.52, 17.66) * mm});
            skLineSegment(sketch, "E1697", {"start": v(10.52, 17.66) * mm, "end": v(10.31, 17.5) * mm});
            skLineSegment(sketch, "E1698", {"start": v(10.31, 17.5) * mm, "end": v(10.1, 17.36) * mm});
            skLineSegment(sketch, "E1699", {"start": v(10.1, 17.36) * mm, "end": v(9.9, 17.21) * mm});
            skLineSegment(sketch, "E1700", {"start": v(9.9, 17.21) * mm, "end": v(9.68, 17.07) * mm});
            skLineSegment(sketch, "E1701", {"start": v(9.68, 17.07) * mm, "end": v(9.46, 16.93) * mm});
            skLineSegment(sketch, "E1702", {"start": v(9.46, 16.93) * mm, "end": v(9.24, 16.8) * mm});
            skLineSegment(sketch, "E1703", {"start": v(9.24, 16.8) * mm, "end": v(9.05, 16.69) * mm});
            skLineSegment(sketch, "E1704", {"start": v(9.05, 16.69) * mm, "end": v(8.87, 16.58) * mm});
            skLineSegment(sketch, "E1705", {"start": v(8.87, 16.58) * mm, "end": v(8.68, 16.47) * mm});
            skLineSegment(sketch, "E1706", {"start": v(8.68, 16.47) * mm, "end": v(8.5, 16.37) * mm});
            skLineSegment(sketch, "E1707", {"start": v(8.5, 16.37) * mm, "end": v(8.3, 16.26) * mm});
            skLineSegment(sketch, "E1708", {"start": v(8.3, 16.26) * mm, "end": v(8.12, 16.16) * mm});
            skLineSegment(sketch, "E1709", {"start": v(8.12, 16.16) * mm, "end": v(7.93, 16.07) * mm});
            skLineSegment(sketch, "E1710", {"start": v(7.93, 16.07) * mm, "end": v(7.74, 15.97) * mm});
            skLineSegment(sketch, "E1711", {"start": v(7.74, 15.97) * mm, "end": v(7.55, 15.88) * mm});
            skLineSegment(sketch, "E1712", {"start": v(7.55, 15.88) * mm, "end": v(7.36, 15.78) * mm});
            skLineSegment(sketch, "E1713", {"start": v(7.36, 15.78) * mm, "end": v(7.17, 15.7) * mm});
            skLineSegment(sketch, "E1714", {"start": v(7.17, 15.7) * mm, "end": v(6.98, 15.6) * mm});
            skLineSegment(sketch, "E1715", {"start": v(6.98, 15.6) * mm, "end": v(6.79, 15.52) * mm});
            skLineSegment(sketch, "E1716", {"start": v(6.79, 15.52) * mm, "end": v(6.6, 15.44) * mm});
            skLineSegment(sketch, "E1717", {"start": v(6.6, 15.44) * mm, "end": v(6.4, 15.36) * mm});
            skLineSegment(sketch, "E1718", {"start": v(6.4, 15.36) * mm, "end": v(6.2, 15.28) * mm});
            skLineSegment(sketch, "E1719", {"start": v(6.2, 15.28) * mm, "end": v(6, 15.2) * mm});
            skLineSegment(sketch, "E1720", {"start": v(6, 15.2) * mm, "end": v(5.8, 15.13) * mm});
            skLineSegment(sketch, "E1721", {"start": v(5.8, 15.13) * mm, "end": v(5.6, 15.06) * mm});
            skLineSegment(sketch, "E1722", {"start": v(5.6, 15.06) * mm, "end": v(5.4, 14.99) * mm});
            skLineSegment(sketch, "E1723", {"start": v(5.4, 14.99) * mm, "end": v(5.2, 14.92) * mm});
            skLineSegment(sketch, "E1724", {"start": v(5.2, 14.92) * mm, "end": v(5, 14.86) * mm});
            skLineSegment(sketch, "E1725", {"start": v(5, 14.86) * mm, "end": v(4.8, 14.8) * mm});
            skLineSegment(sketch, "E1726", {"start": v(4.8, 14.8) * mm, "end": v(4.6, 14.73) * mm});
            skLineSegment(sketch, "E1727", {"start": v(4.6, 14.73) * mm, "end": v(4.4, 14.68) * mm});
            skLineSegment(sketch, "E1728", {"start": v(4.4, 14.68) * mm, "end": v(4.2, 14.62) * mm});
            skLineSegment(sketch, "E1729", {"start": v(4.2, 14.62) * mm, "end": v(4, 14.57) * mm});
            skLineSegment(sketch, "E1730", {"start": v(4, 14.57) * mm, "end": v(3.79, 14.52) * mm});
            skLineSegment(sketch, "E1731", {"start": v(3.79, 14.52) * mm, "end": v(3.58, 14.48) * mm});
            skLineSegment(sketch, "E1732", {"start": v(3.58, 14.48) * mm, "end": v(3.37, 14.43) * mm});
            skLineSegment(sketch, "E1733", {"start": v(3.37, 14.43) * mm, "end": v(3.16, 14.4) * mm});
            skLineSegment(sketch, "E1734", {"start": v(3.16, 14.4) * mm, "end": v(2.95, 14.35) * mm});
            skLineSegment(sketch, "E1735", {"start": v(2.95, 14.35) * mm, "end": v(2.85, 14.33) * mm});
            skLineSegment(sketch, "E1736", {"start": v(2.85, 14.33) * mm, "end": v(2.74, 14.32) * mm});
            skLineSegment(sketch, "E1737", {"start": v(2.74, 14.32) * mm, "end": v(2.63, 14.3) * mm});
            skLineSegment(sketch, "E1738", {"start": v(2.63, 14.3) * mm, "end": v(2.52, 14.29) * mm});
            skLineSegment(sketch, "E1739", {"start": v(2.52, 14.29) * mm, "end": v(2.41, 14.27) * mm});
            skLineSegment(sketch, "E1740", {"start": v(2.41, 14.27) * mm, "end": v(2.3, 14.26) * mm});
            skLineSegment(sketch, "E1741", {"start": v(2.3, 14.26) * mm, "end": v(2.2, 14.25) * mm});
            skLineSegment(sketch, "E1742", {"start": v(2.2, 14.25) * mm, "end": v(2.08, 14.24) * mm});
            skLineSegment(sketch, "E1743", {"start": v(2.08, 14.24) * mm, "end": v(1.97, 14.23) * mm});
            skLineSegment(sketch, "E1744", {"start": v(1.97, 14.23) * mm, "end": v(1.86, 14.23) * mm});
            skLineSegment(sketch, "E1745", {"start": v(1.86, 14.23) * mm, "end": v(1.75, 14.22) * mm});
            skLineSegment(sketch, "E1746", {"start": v(1.75, 14.22) * mm, "end": v(1.64, 14.21) * mm});
            skLineSegment(sketch, "E1747", {"start": v(1.64, 14.21) * mm, "end": v(1.53, 14.21) * mm});
            skLineSegment(sketch, "E1748", {"start": v(1.53, 14.21) * mm, "end": v(1.42, 14.2) * mm});
            skLineSegment(sketch, "E1749", {"start": v(1.42, 14.2) * mm, "end": v(1.3, 14.2) * mm});
            skLineSegment(sketch, "E1750", {"start": v(1.3, 14.2) * mm, "end": v(1.2, 14.2) * mm});
            skLineSegment(sketch, "E1751", {"start": v(1.2, 14.2) * mm, "end": v(1.09, 14.2) * mm});
            skLineSegment(sketch, "E1752", {"start": v(1.09, 14.2) * mm, "end": v(0.97, 14.2) * mm});
            skLineSegment(sketch, "E1753", {"start": v(0.97, 14.2) * mm, "end": v(0.86, 14.2) * mm});
            skLineSegment(sketch, "E1754", {"start": v(0.86, 14.2) * mm, "end": v(0.75, 14.21) * mm});
            skLineSegment(sketch, "E1755", {"start": v(0.75, 14.21) * mm, "end": v(0.64, 14.22) * mm});
            skLineSegment(sketch, "E1756", {"start": v(0.64, 14.22) * mm, "end": v(0.53, 14.22) * mm});
            skLineSegment(sketch, "E1757", {"start": v(0.53, 14.22) * mm, "end": v(0.42, 14.23) * mm});
            skLineSegment(sketch, "E1758", {"start": v(0.42, 14.23) * mm, "end": v(0.3, 14.23) * mm});
            skLineSegment(sketch, "E1759", {"start": v(0.3, 14.23) * mm, "end": v(0.2, 14.24) * mm});
            skLineSegment(sketch, "E1760", {"start": v(0.2, 14.24) * mm, "end": v(0.09, 14.25) * mm});
            skLineSegment(sketch, "E1761", {"start": v(0.09, 14.25) * mm, "end": v(-0.02, 14.26) * mm});
            skLineSegment(sketch, "E1762", {"start": v(-0.02, 14.26) * mm, "end": v(-0.13, 14.27) * mm});
            skLineSegment(sketch, "E1763", {"start": v(-0.13, 14.27) * mm, "end": v(-0.24, 14.28) * mm});
            skLineSegment(sketch, "E1764", {"start": v(-0.24, 14.28) * mm, "end": v(-0.35, 14.3) * mm});
            skLineSegment(sketch, "E1765", {"start": v(-0.35, 14.3) * mm, "end": v(-0.46, 14.3) * mm});
            skLineSegment(sketch, "E1766", {"start": v(-0.46, 14.3) * mm, "end": v(-0.57, 14.32) * mm});
            skLineSegment(sketch, "E1767", {"start": v(-0.57, 14.32) * mm, "end": v(-0.7, 14.34) * mm});
            skLineSegment(sketch, "E1768", {"start": v(-0.7, 14.34) * mm, "end": v(-0.82, 14.36) * mm});
            skLineSegment(sketch, "E1769", {"start": v(-0.82, 14.36) * mm, "end": v(-0.93, 14.39) * mm});
            skLineSegment(sketch, "E1770", {"start": v(-0.93, 14.39) * mm, "end": v(-1.05, 14.42) * mm});
            skLineSegment(sketch, "E1771", {"start": v(-1.05, 14.42) * mm, "end": v(-1.15, 14.45) * mm});
            skLineSegment(sketch, "E1772", {"start": v(-1.15, 14.45) * mm, "end": v(-1.25, 14.5) * mm});
            skLineSegment(sketch, "E1773", {"start": v(-1.25, 14.5) * mm, "end": v(-1.35, 14.53) * mm});
            skLineSegment(sketch, "E1774", {"start": v(-1.35, 14.53) * mm, "end": v(-1.44, 14.58) * mm});
            skLineSegment(sketch, "E1775", {"start": v(-1.44, 14.58) * mm, "end": v(-1.53, 14.63) * mm});
            skLineSegment(sketch, "E1776", {"start": v(-1.53, 14.63) * mm, "end": v(-1.6, 14.69) * mm});
            skLineSegment(sketch, "E1777", {"start": v(-1.6, 14.69) * mm, "end": v(-1.68, 14.74) * mm});
            skLineSegment(sketch, "E1778", {"start": v(-1.68, 14.74) * mm, "end": v(-1.76, 14.8) * mm});
            skLineSegment(sketch, "E1779", {"start": v(-1.76, 14.8) * mm, "end": v(-1.82, 14.87) * mm});
            skLineSegment(sketch, "E1780", {"start": v(-1.82, 14.87) * mm, "end": v(-1.89, 14.94) * mm});
            skLineSegment(sketch, "E1781", {"start": v(-1.89, 14.94) * mm, "end": v(-1.94, 15.02) * mm});
            skLineSegment(sketch, "E1782", {"start": v(-1.94, 15.02) * mm, "end": v(-2, 15.1) * mm});
            skLineSegment(sketch, "E1783", {"start": v(-2, 15.1) * mm, "end": v(-2.05, 15.17) * mm});
            skLineSegment(sketch, "E1784", {"start": v(-2.05, 15.17) * mm, "end": v(-2.1, 15.26) * mm});
            skLineSegment(sketch, "E1785", {"start": v(-2.1, 15.26) * mm, "end": v(-2.14, 15.35) * mm});
            skLineSegment(sketch, "E1786", {"start": v(-2.14, 15.35) * mm, "end": v(-2.17, 15.44) * mm});
            skLineSegment(sketch, "E1787", {"start": v(-2.17, 15.44) * mm, "end": v(-2.2, 15.53) * mm});
            skLineSegment(sketch, "E1788", {"start": v(-2.2, 15.53) * mm, "end": v(-2.24, 15.63) * mm});
            skLineSegment(sketch, "E1789", {"start": v(-2.24, 15.63) * mm, "end": v(-2.26, 15.73) * mm});
            skLineSegment(sketch, "E1790", {"start": v(-2.26, 15.73) * mm, "end": v(-2.28, 15.83) * mm});
            skLineSegment(sketch, "E1791", {"start": v(-2.28, 15.83) * mm, "end": v(-2.3, 15.94) * mm});
            skLineSegment(sketch, "E1792", {"start": v(-2.3, 15.94) * mm, "end": v(-2.32, 16.05) * mm});
            skLineSegment(sketch, "E1793", {"start": v(-2.32, 16.05) * mm, "end": v(-2.33, 16.17) * mm});
            skLineSegment(sketch, "E1794", {"start": v(-2.33, 16.17) * mm, "end": v(-2.34, 16.28) * mm});
            skLineSegment(sketch, "E1795", {"start": v(-2.34, 16.28) * mm, "end": v(-2.34, 16.4) * mm});
            skLineSegment(sketch, "E1796", {"start": v(-2.34, 16.4) * mm, "end": v(-2.34, 16.52) * mm});
            skLineSegment(sketch, "E1797", {"start": v(-2.34, 16.52) * mm, "end": v(-2.34, 16.65) * mm});
            skLineSegment(sketch, "E1798", {"start": v(-2.34, 16.65) * mm, "end": v(-2.33, 16.78) * mm});
            skLineSegment(sketch, "E1799", {"start": v(-2.33, 16.78) * mm, "end": v(-2.32, 16.94) * mm});
            skLineSegment(sketch, "E1800", {"start": v(-2.32, 16.94) * mm, "end": v(-2.3, 17.1) * mm});
            skLineSegment(sketch, "E1801", {"start": v(-2.3, 17.1) * mm, "end": v(-2.28, 17.25) * mm});
            skLineSegment(sketch, "E1802", {"start": v(-2.28, 17.25) * mm, "end": v(-2.26, 17.4) * mm});
            skLineSegment(sketch, "E1803", {"start": v(-2.26, 17.4) * mm, "end": v(-2.23, 17.55) * mm});
            skLineSegment(sketch, "E1804", {"start": v(-2.23, 17.55) * mm, "end": v(-2.2, 17.7) * mm});
            skLineSegment(sketch, "E1805", {"start": v(-2.2, 17.7) * mm, "end": v(-2.17, 17.85) * mm});
            skLineSegment(sketch, "E1806", {"start": v(-2.17, 17.85) * mm, "end": v(-2.13, 18) * mm});
            skLineSegment(sketch, "E1807", {"start": v(-2.13, 18) * mm, "end": v(-2.1, 18.15) * mm});
            skLineSegment(sketch, "E1808", {"start": v(-2.1, 18.15) * mm, "end": v(-2.05, 18.3) * mm});
            skLineSegment(sketch, "E1809", {"start": v(-2.05, 18.3) * mm, "end": v(-2, 18.44) * mm});
            skLineSegment(sketch, "E1810", {"start": v(-2, 18.44) * mm, "end": v(-1.96, 18.58) * mm});
            skLineSegment(sketch, "E1811", {"start": v(-1.96, 18.58) * mm, "end": v(-1.91, 18.73) * mm});
            skLineSegment(sketch, "E1812", {"start": v(-1.91, 18.73) * mm, "end": v(-1.86, 18.87) * mm});
            skLineSegment(sketch, "E1813", {"start": v(-1.86, 18.87) * mm, "end": v(-1.8, 19.01) * mm});
            skLineSegment(sketch, "E1814", {"start": v(-1.8, 19.01) * mm, "end": v(-1.75, 19.16) * mm});
            skLineSegment(sketch, "E1815", {"start": v(-1.75, 19.16) * mm, "end": v(-1.7, 19.3) * mm});
            skLineSegment(sketch, "E1816", {"start": v(-1.7, 19.3) * mm, "end": v(-1.64, 19.44) * mm});
            skLineSegment(sketch, "E1817", {"start": v(-1.64, 19.44) * mm, "end": v(-1.58, 19.58) * mm});
            skLineSegment(sketch, "E1818", {"start": v(-1.58, 19.58) * mm, "end": v(-1.52, 19.72) * mm});
            skLineSegment(sketch, "E1819", {"start": v(-1.52, 19.72) * mm, "end": v(-1.46, 19.86) * mm});
            skLineSegment(sketch, "E1820", {"start": v(-1.46, 19.86) * mm, "end": v(-1.4, 20) * mm});
            skLineSegment(sketch, "E1821", {"start": v(-1.4, 20) * mm, "end": v(-1.34, 20.14) * mm});
            skLineSegment(sketch, "E1822", {"start": v(-1.34, 20.14) * mm, "end": v(-1.28, 20.28) * mm});
            skLineSegment(sketch, "E1823", {"start": v(-1.28, 20.28) * mm, "end": v(-1.22, 20.41) * mm});
            skLineSegment(sketch, "E1824", {"start": v(-1.22, 20.41) * mm, "end": v(-1.16, 20.55) * mm});
            skLineSegment(sketch, "E1825", {"start": v(-1.16, 20.55) * mm, "end": v(-1.1, 20.7) * mm});
            skLineSegment(sketch, "E1826", {"start": v(-1.1, 20.7) * mm, "end": v(-1.04, 20.83) * mm});
            skLineSegment(sketch, "E1827", {"start": v(-1.04, 20.83) * mm, "end": v(-0.98, 20.97) * mm});
            skLineSegment(sketch, "E1828", {"start": v(-0.98, 20.97) * mm, "end": v(-0.92, 21.11) * mm});
            skLineSegment(sketch, "E1829", {"start": v(-0.92, 21.11) * mm, "end": v(-0.86, 21.25) * mm});
            skLineSegment(sketch, "E1830", {"start": v(-0.86, 21.25) * mm, "end": v(-0.8, 21.4) * mm});
            skLineSegment(sketch, "E1831", {"start": v(-0.8, 21.4) * mm, "end": v(-0.79, 21.42) * mm});
            skLineSegment(sketch, "E1832", {"start": v(-0.79, 21.42) * mm, "end": v(-0.78, 21.43) * mm});
            skLineSegment(sketch, "E1833", {"start": v(-0.78, 21.43) * mm, "end": v(-0.77, 21.44) * mm});
            skLineSegment(sketch, "E1834", {"start": v(-0.77, 21.44) * mm, "end": v(-0.76, 21.45) * mm});
            skLineSegment(sketch, "E1835", {"start": v(-0.76, 21.45) * mm, "end": v(-0.74, 21.47) * mm});
            skLineSegment(sketch, "E1836", {"start": v(-0.74, 21.47) * mm, "end": v(-0.73, 21.48) * mm});
            skLineSegment(sketch, "E1837", {"start": v(-0.73, 21.48) * mm, "end": v(-0.71, 21.49) * mm});
            skLineSegment(sketch, "E1838", {"start": v(-0.71, 21.49) * mm, "end": v(-0.7, 21.5) * mm});
            skLineSegment(sketch, "E1839", {"start": v(-0.7, 21.5) * mm, "end": v(-0.68, 21.5) * mm});
            skLineSegment(sketch, "E1840", {"start": v(-0.68, 21.5) * mm, "end": v(-0.66, 21.52) * mm});
            skLineSegment(sketch, "E1841", {"start": v(-0.66, 21.52) * mm, "end": v(-0.64, 21.52) * mm});
            skLineSegment(sketch, "E1842", {"start": v(-0.64, 21.52) * mm, "end": v(-0.62, 21.53) * mm});
            skLineSegment(sketch, "E1843", {"start": v(-0.62, 21.53) * mm, "end": v(-0.6, 21.54) * mm});
            skLineSegment(sketch, "E1844", {"start": v(-0.6, 21.54) * mm, "end": v(-0.58, 21.55) * mm});
            skLineSegment(sketch, "E1845", {"start": v(-0.58, 21.55) * mm, "end": v(-0.55, 21.56) * mm});
            skLineSegment(sketch, "E1846", {"start": v(-0.55, 21.56) * mm, "end": v(-0.53, 21.56) * mm});
            skLineSegment(sketch, "E1847", {"start": v(-0.53, 21.56) * mm, "end": v(-0.5, 21.57) * mm});
            skLineSegment(sketch, "E1848", {"start": v(-0.5, 21.57) * mm, "end": v(-0.48, 21.58) * mm});
            skLineSegment(sketch, "E1849", {"start": v(-0.48, 21.58) * mm, "end": v(-0.46, 21.58) * mm});
            skLineSegment(sketch, "E1850", {"start": v(-0.46, 21.58) * mm, "end": v(-0.44, 21.59) * mm});
            skLineSegment(sketch, "E1851", {"start": v(-0.44, 21.59) * mm, "end": v(-0.41, 21.6) * mm});
            skLineSegment(sketch, "E1852", {"start": v(-0.41, 21.6) * mm, "end": v(-0.39, 21.6) * mm});
            skLineSegment(sketch, "E1853", {"start": v(-0.39, 21.6) * mm, "end": v(-0.36, 21.6) * mm});
            skLineSegment(sketch, "E1854", {"start": v(-0.36, 21.6) * mm, "end": v(-0.34, 21.6) * mm});
            skLineSegment(sketch, "E1855", {"start": v(-0.34, 21.6) * mm, "end": v(-0.32, 21.6) * mm});
            skLineSegment(sketch, "E1856", {"start": v(-0.32, 21.6) * mm, "end": v(-0.3, 21.6) * mm});
            skLineSegment(sketch, "E1857", {"start": v(-0.3, 21.6) * mm, "end": v(-0.27, 21.61) * mm});
            skLineSegment(sketch, "E1858", {"start": v(-0.27, 21.61) * mm, "end": v(-0.25, 21.61) * mm});
            skLineSegment(sketch, "E1859", {"start": v(-0.25, 21.61) * mm, "end": v(-0.23, 21.61) * mm});
            skLineSegment(sketch, "E1860", {"start": v(-0.23, 21.61) * mm, "end": v(-0.2, 21.61) * mm});
            skLineSegment(sketch, "E1861", {"start": v(-0.2, 21.61) * mm, "end": v(-0.18, 21.61) * mm});
            skLineSegment(sketch, "E1862", {"start": v(-0.18, 21.61) * mm, "end": v(0.04, 21.61) * mm});
            skLineSegment(sketch, "E1863", {"start": v(0.04, 21.61) * mm, "end": v(0.26, 21.62) * mm});
            skLineSegment(sketch, "E1864", {"start": v(0.26, 21.62) * mm, "end": v(0.48, 21.62) * mm});
            skLineSegment(sketch, "E1865", {"start": v(0.48, 21.62) * mm, "end": v(0.7, 21.62) * mm});
            skLineSegment(sketch, "E1866", {"start": v(0.7, 21.62) * mm, "end": v(0.92, 21.63) * mm});
            skLineSegment(sketch, "E1867", {"start": v(0.92, 21.63) * mm, "end": v(1.14, 21.64) * mm});
            skLineSegment(sketch, "E1868", {"start": v(1.14, 21.64) * mm, "end": v(1.36, 21.65) * mm});
            skLineSegment(sketch, "E1869", {"start": v(1.36, 21.65) * mm, "end": v(1.58, 21.66) * mm});
            skLineSegment(sketch, "E1870", {"start": v(1.58, 21.66) * mm, "end": v(1.8, 21.67) * mm});
            skLineSegment(sketch, "E1871", {"start": v(1.8, 21.67) * mm, "end": v(2.01, 21.7) * mm});
            skLineSegment(sketch, "E1872", {"start": v(2.01, 21.7) * mm, "end": v(2.23, 21.7) * mm});
            skLineSegment(sketch, "E1873", {"start": v(2.23, 21.7) * mm, "end": v(2.45, 21.73) * mm});
            skLineSegment(sketch, "E1874", {"start": v(2.45, 21.73) * mm, "end": v(2.67, 21.75) * mm});
            skLineSegment(sketch, "E1875", {"start": v(2.67, 21.75) * mm, "end": v(2.89, 21.77) * mm});
            skLineSegment(sketch, "E1876", {"start": v(2.89, 21.77) * mm, "end": v(3.1, 21.8) * mm});
            skLineSegment(sketch, "E1877", {"start": v(3.1, 21.8) * mm, "end": v(3.32, 21.82) * mm});
            skLineSegment(sketch, "E1878", {"start": v(3.32, 21.82) * mm, "end": v(3.54, 21.85) * mm});
            skLineSegment(sketch, "E1879", {"start": v(3.54, 21.85) * mm, "end": v(3.76, 21.87) * mm});
            skLineSegment(sketch, "E1880", {"start": v(3.76, 21.87) * mm, "end": v(3.97, 21.9) * mm});
            skLineSegment(sketch, "E1881", {"start": v(3.97, 21.9) * mm, "end": v(4.2, 21.94) * mm});
            skLineSegment(sketch, "E1882", {"start": v(4.2, 21.94) * mm, "end": v(4.4, 21.97) * mm});
            skLineSegment(sketch, "E1883", {"start": v(4.4, 21.97) * mm, "end": v(4.62, 22) * mm});
            skLineSegment(sketch, "E1884", {"start": v(4.62, 22) * mm, "end": v(4.84, 22.04) * mm});
            skLineSegment(sketch, "E1885", {"start": v(4.84, 22.04) * mm, "end": v(5.06, 22.08) * mm});
            skLineSegment(sketch, "E1886", {"start": v(5.06, 22.08) * mm, "end": v(5.27, 22.12) * mm});
            skLineSegment(sketch, "E1887", {"start": v(5.27, 22.12) * mm, "end": v(5.49, 22.16) * mm});
            skLineSegment(sketch, "E1888", {"start": v(5.49, 22.16) * mm, "end": v(5.7, 22.2) * mm});
            skLineSegment(sketch, "E1889", {"start": v(5.7, 22.2) * mm, "end": v(5.92, 22.25) * mm});
            skLineSegment(sketch, "E1890", {"start": v(5.92, 22.25) * mm, "end": v(6.13, 22.3) * mm});
            skLineSegment(sketch, "E1891", {"start": v(6.13, 22.3) * mm, "end": v(6.35, 22.34) * mm});
            skLineSegment(sketch, "E1892", {"start": v(6.35, 22.34) * mm, "end": v(6.56, 22.39) * mm});
            skLineSegment(sketch, "E1893", {"start": v(6.56, 22.39) * mm, "end": v(6.78, 22.44) * mm});
            skLineSegment(sketch, "E1894", {"start": v(6.78, 22.44) * mm, "end": v(7, 22.5) * mm});
            skLineSegment(sketch, "E1895", {"start": v(7, 22.5) * mm, "end": v(7.24, 22.55) * mm});
            skLineSegment(sketch, "E1896", {"start": v(7.24, 22.55) * mm, "end": v(7.48, 22.61) * mm});
            skLineSegment(sketch, "E1897", {"start": v(7.48, 22.61) * mm, "end": v(7.7, 22.67) * mm});
            skLineSegment(sketch, "E1898", {"start": v(7.7, 22.67) * mm, "end": v(7.94, 22.74) * mm});
            skLineSegment(sketch, "E1899", {"start": v(7.94, 22.74) * mm, "end": v(8.17, 22.8) * mm});
            skLineSegment(sketch, "E1900", {"start": v(8.17, 22.8) * mm, "end": v(8.4, 22.87) * mm});
            skLineSegment(sketch, "E1901", {"start": v(8.4, 22.87) * mm, "end": v(8.62, 22.95) * mm});
            skLineSegment(sketch, "E1902", {"start": v(8.62, 22.95) * mm, "end": v(8.85, 23.02) * mm});
            skLineSegment(sketch, "E1903", {"start": v(8.85, 23.02) * mm, "end": v(9.08, 23.1) * mm});
            skLineSegment(sketch, "E1904", {"start": v(9.08, 23.1) * mm, "end": v(9.3, 23.18) * mm});
            skLineSegment(sketch, "E1905", {"start": v(9.3, 23.18) * mm, "end": v(9.53, 23.26) * mm});
            skLineSegment(sketch, "E1906", {"start": v(9.53, 23.26) * mm, "end": v(9.75, 23.34) * mm});
            skLineSegment(sketch, "E1907", {"start": v(9.75, 23.34) * mm, "end": v(9.97, 23.43) * mm});
            skLineSegment(sketch, "E1908", {"start": v(9.97, 23.43) * mm, "end": v(10.19, 23.52) * mm});
            skLineSegment(sketch, "E1909", {"start": v(10.19, 23.52) * mm, "end": v(10.4, 23.61) * mm});
            skLineSegment(sketch, "E1910", {"start": v(10.4, 23.61) * mm, "end": v(10.62, 23.71) * mm});
            skLineSegment(sketch, "E1911", {"start": v(10.62, 23.71) * mm, "end": v(10.84, 23.81) * mm});
            skLineSegment(sketch, "E1912", {"start": v(10.84, 23.81) * mm, "end": v(11.05, 23.91) * mm});
            skLineSegment(sketch, "E1913", {"start": v(11.05, 23.91) * mm, "end": v(11.26, 24.02) * mm});
            skLineSegment(sketch, "E1914", {"start": v(11.26, 24.02) * mm, "end": v(11.48, 24.13) * mm});
            skLineSegment(sketch, "E1915", {"start": v(11.48, 24.13) * mm, "end": v(11.68, 24.24) * mm});
            skLineSegment(sketch, "E1916", {"start": v(11.68, 24.24) * mm, "end": v(11.9, 24.36) * mm});
            skLineSegment(sketch, "E1917", {"start": v(11.9, 24.36) * mm, "end": v(12.1, 24.48) * mm});
            skLineSegment(sketch, "E1918", {"start": v(12.1, 24.48) * mm, "end": v(12.3, 24.6) * mm});
            skLineSegment(sketch, "E1919", {"start": v(12.3, 24.6) * mm, "end": v(12.5, 24.73) * mm});
            skLineSegment(sketch, "E1920", {"start": v(12.5, 24.73) * mm, "end": v(12.7, 24.86) * mm});
            skLineSegment(sketch, "E1921", {"start": v(12.7, 24.86) * mm, "end": v(12.9, 25) * mm});
            skLineSegment(sketch, "E1922", {"start": v(12.9, 25) * mm, "end": v(13.1, 25.14) * mm});
            skLineSegment(sketch, "E1923", {"start": v(13.1, 25.14) * mm, "end": v(13.28, 25.28) * mm});
            skLineSegment(sketch, "E1924", {"start": v(13.28, 25.28) * mm, "end": v(13.47, 25.43) * mm});
            skLineSegment(sketch, "E1925", {"start": v(13.47, 25.43) * mm, "end": v(13.66, 25.58) * mm});
            skLineSegment(sketch, "E1926", {"start": v(13.66, 25.58) * mm, "end": v(13.77, 25.67) * mm});
            skLineSegment(sketch, "E1927", {"start": v(13.77, 25.67) * mm, "end": v(13.87, 25.76) * mm});
            skLineSegment(sketch, "E1928", {"start": v(13.87, 25.76) * mm, "end": v(13.97, 25.85) * mm});
            skLineSegment(sketch, "E1929", {"start": v(13.97, 25.85) * mm, "end": v(14.07, 25.94) * mm});
            skLineSegment(sketch, "E1930", {"start": v(14.07, 25.94) * mm, "end": v(14.17, 26.03) * mm});
            skLineSegment(sketch, "E1931", {"start": v(14.17, 26.03) * mm, "end": v(14.27, 26.12) * mm});
            skLineSegment(sketch, "E1932", {"start": v(14.27, 26.12) * mm, "end": v(14.36, 26.22) * mm});
            skLineSegment(sketch, "E1933", {"start": v(14.36, 26.22) * mm, "end": v(14.46, 26.32) * mm});
            skLineSegment(sketch, "E1934", {"start": v(14.46, 26.32) * mm, "end": v(14.55, 26.41) * mm});
            skLineSegment(sketch, "E1935", {"start": v(14.55, 26.41) * mm, "end": v(14.65, 26.51) * mm});
            skLineSegment(sketch, "E1936", {"start": v(14.65, 26.51) * mm, "end": v(14.74, 26.61) * mm});
            skLineSegment(sketch, "E1937", {"start": v(14.74, 26.61) * mm, "end": v(14.83, 26.71) * mm});
            skLineSegment(sketch, "E1938", {"start": v(14.83, 26.71) * mm, "end": v(14.93, 26.81) * mm});
            skLineSegment(sketch, "E1939", {"start": v(14.93, 26.81) * mm, "end": v(15.02, 26.91) * mm});
            skLineSegment(sketch, "E1940", {"start": v(15.02, 26.91) * mm, "end": v(15.1, 27.01) * mm});
            skLineSegment(sketch, "E1941", {"start": v(15.1, 27.01) * mm, "end": v(15.2, 27.11) * mm});
            skLineSegment(sketch, "E1942", {"start": v(15.2, 27.11) * mm, "end": v(15.28, 27.22) * mm});
            skLineSegment(sketch, "E1943", {"start": v(15.28, 27.22) * mm, "end": v(15.37, 27.32) * mm});
            skLineSegment(sketch, "E1944", {"start": v(15.37, 27.32) * mm, "end": v(15.46, 27.42) * mm});
            skLineSegment(sketch, "E1945", {"start": v(15.46, 27.42) * mm, "end": v(15.55, 27.52) * mm});
            skLineSegment(sketch, "E1946", {"start": v(15.55, 27.52) * mm, "end": v(15.63, 27.62) * mm});
            skLineSegment(sketch, "E1947", {"start": v(15.63, 27.62) * mm, "end": v(15.72, 27.73) * mm});
            skLineSegment(sketch, "E1948", {"start": v(15.72, 27.73) * mm, "end": v(15.8, 27.83) * mm});
            skLineSegment(sketch, "E1949", {"start": v(15.8, 27.83) * mm, "end": v(15.9, 27.93) * mm});
            skLineSegment(sketch, "E1950", {"start": v(15.9, 27.93) * mm, "end": v(15.98, 28.03) * mm});
            skLineSegment(sketch, "E1951", {"start": v(15.98, 28.03) * mm, "end": v(16.07, 28.13) * mm});
            skLineSegment(sketch, "E1952", {"start": v(16.07, 28.13) * mm, "end": v(16.15, 28.23) * mm});
            skLineSegment(sketch, "E1953", {"start": v(16.15, 28.23) * mm, "end": v(16.24, 28.33) * mm});
            skLineSegment(sketch, "E1954", {"start": v(16.24, 28.33) * mm, "end": v(16.32, 28.43) * mm});
            skLineSegment(sketch, "E1955", {"start": v(16.32, 28.43) * mm, "end": v(16.41, 28.52) * mm});
            skLineSegment(sketch, "E1956", {"start": v(16.41, 28.52) * mm, "end": v(16.5, 28.62) * mm});
            skLineSegment(sketch, "E1957", {"start": v(16.5, 28.62) * mm, "end": v(16.58, 28.71) * mm});
            skLineSegment(sketch, "E1958", {"start": v(1.22, 40.8) * mm, "end": v(1.14, 40.8) * mm});
            skLineSegment(sketch, "E1959", {"start": v(1.14, 40.8) * mm, "end": v(1.06, 40.8) * mm});
            skLineSegment(sketch, "E1960", {"start": v(1.06, 40.8) * mm, "end": v(0.98, 40.81) * mm});
            skLineSegment(sketch, "E1961", {"start": v(0.98, 40.81) * mm, "end": v(0.9, 40.82) * mm});
            skLineSegment(sketch, "E1962", {"start": v(0.9, 40.82) * mm, "end": v(0.82, 40.82) * mm});
            skLineSegment(sketch, "E1963", {"start": v(0.82, 40.82) * mm, "end": v(0.74, 40.83) * mm});
            skLineSegment(sketch, "E1964", {"start": v(0.74, 40.83) * mm, "end": v(0.66, 40.84) * mm});
            skLineSegment(sketch, "E1965", {"start": v(0.66, 40.84) * mm, "end": v(0.59, 40.84) * mm});
            skLineSegment(sketch, "E1966", {"start": v(0.59, 40.84) * mm, "end": v(0.5, 40.85) * mm});
            skLineSegment(sketch, "E1967", {"start": v(0.5, 40.85) * mm, "end": v(0.43, 40.85) * mm});
            skLineSegment(sketch, "E1968", {"start": v(0.43, 40.85) * mm, "end": v(0.36, 40.86) * mm});
            skLineSegment(sketch, "E1969", {"start": v(0.36, 40.86) * mm, "end": v(0.29, 40.87) * mm});
            skLineSegment(sketch, "E1970", {"start": v(0.29, 40.87) * mm, "end": v(0.21, 40.87) * mm});
            skLineSegment(sketch, "E1971", {"start": v(0.21, 40.87) * mm, "end": v(0.14, 40.88) * mm});
            skLineSegment(sketch, "E1972", {"start": v(0.14, 40.88) * mm, "end": v(0.07, 40.88) * mm});
            skLineSegment(sketch, "E1973", {"start": v(0.07, 40.88) * mm, "end": v(0, 40.89) * mm});
            skLineSegment(sketch, "E1974", {"start": v(0, 40.89) * mm, "end": v(-0.08, 40.9) * mm});
            skLineSegment(sketch, "E1975", {"start": v(-0.08, 40.9) * mm, "end": v(-0.15, 40.9) * mm});
            skLineSegment(sketch, "E1976", {"start": v(-0.15, 40.9) * mm, "end": v(-0.22, 40.9) * mm});
            skLineSegment(sketch, "E1977", {"start": v(-0.22, 40.9) * mm, "end": v(-0.29, 40.9) * mm});
            skLineSegment(sketch, "E1978", {"start": v(-0.29, 40.9) * mm, "end": v(-0.36, 40.91) * mm});
            skLineSegment(sketch, "E1979", {"start": v(-0.36, 40.91) * mm, "end": v(-0.43, 40.92) * mm});
            skLineSegment(sketch, "E1980", {"start": v(-0.43, 40.92) * mm, "end": v(-0.5, 40.92) * mm});
            skLineSegment(sketch, "E1981", {"start": v(-0.5, 40.92) * mm, "end": v(-0.56, 40.93) * mm});
            skLineSegment(sketch, "E1982", {"start": v(-0.56, 40.93) * mm, "end": v(-0.63, 40.93) * mm});
            skLineSegment(sketch, "E1983", {"start": v(-0.63, 40.93) * mm, "end": v(-0.7, 40.93) * mm});
            skLineSegment(sketch, "E1984", {"start": v(-0.7, 40.93) * mm, "end": v(-0.77, 40.94) * mm});
            skLineSegment(sketch, "E1985", {"start": v(-0.77, 40.94) * mm, "end": v(-0.84, 40.94) * mm});
            skLineSegment(sketch, "E1986", {"start": v(-0.84, 40.94) * mm, "end": v(-0.9, 40.94) * mm});
            skLineSegment(sketch, "E1987", {"start": v(-0.9, 40.94) * mm, "end": v(-0.97, 40.94) * mm});
            skLineSegment(sketch, "E1988", {"start": v(-0.97, 40.94) * mm, "end": v(-1.04, 40.94) * mm});
            skLineSegment(sketch, "E1989", {"start": v(-1.04, 40.94) * mm, "end": v(-1.1, 40.94) * mm});
            skLineSegment(sketch, "E1990", {"start": v(-1.1, 40.94) * mm, "end": v(-1.35, 40.94) * mm});
            skLineSegment(sketch, "E1991", {"start": v(-1.35, 40.94) * mm, "end": v(-1.6, 40.94) * mm});
            skLineSegment(sketch, "E1992", {"start": v(-1.6, 40.94) * mm, "end": v(-1.83, 40.94) * mm});
            skLineSegment(sketch, "E1993", {"start": v(-1.83, 40.94) * mm, "end": v(-2.07, 40.93) * mm});
            skLineSegment(sketch, "E1994", {"start": v(-2.07, 40.93) * mm, "end": v(-2.31, 40.92) * mm});
            skLineSegment(sketch, "E1995", {"start": v(-2.31, 40.92) * mm, "end": v(-2.55, 40.9) * mm});
            skLineSegment(sketch, "E1996", {"start": v(-2.55, 40.9) * mm, "end": v(-2.79, 40.89) * mm});
            skLineSegment(sketch, "E1997", {"start": v(-2.79, 40.89) * mm, "end": v(-3.02, 40.87) * mm});
            skLineSegment(sketch, "E1998", {"start": v(-3.02, 40.87) * mm, "end": v(-3.26, 40.84) * mm});
            skLineSegment(sketch, "E1999", {"start": v(-3.26, 40.84) * mm, "end": v(-3.5, 40.82) * mm});
            skLineSegment(sketch, "E2000", {"start": v(-3.5, 40.82) * mm, "end": v(-3.74, 40.8) * mm});
            skLineSegment(sketch, "E2001", {"start": v(-3.74, 40.8) * mm, "end": v(-3.97, 40.76) * mm});
            skLineSegment(sketch, "E2002", {"start": v(-3.97, 40.76) * mm, "end": v(-4.2, 40.73) * mm});
            skLineSegment(sketch, "E2003", {"start": v(-4.2, 40.73) * mm, "end": v(-4.44, 40.7) * mm});
            skLineSegment(sketch, "E2004", {"start": v(-4.44, 40.7) * mm, "end": v(-4.68, 40.66) * mm});
            skLineSegment(sketch, "E2005", {"start": v(-4.68, 40.66) * mm, "end": v(-4.91, 40.62) * mm});
            skLineSegment(sketch, "E2006", {"start": v(-4.91, 40.62) * mm, "end": v(-5.15, 40.57) * mm});
            skLineSegment(sketch, "E2007", {"start": v(-5.15, 40.57) * mm, "end": v(-5.38, 40.53) * mm});
            skLineSegment(sketch, "E2008", {"start": v(-5.38, 40.53) * mm, "end": v(-5.61, 40.48) * mm});
            skLineSegment(sketch, "E2009", {"start": v(-5.61, 40.48) * mm, "end": v(-5.85, 40.43) * mm});
            skLineSegment(sketch, "E2010", {"start": v(-5.85, 40.43) * mm, "end": v(-6.08, 40.38) * mm});
            skLineSegment(sketch, "E2011", {"start": v(-6.08, 40.38) * mm, "end": v(-6.31, 40.33) * mm});
            skLineSegment(sketch, "E2012", {"start": v(-6.31, 40.33) * mm, "end": v(-6.54, 40.27) * mm});
            skLineSegment(sketch, "E2013", {"start": v(-6.54, 40.27) * mm, "end": v(-6.77, 40.21) * mm});
            skLineSegment(sketch, "E2014", {"start": v(-6.77, 40.21) * mm, "end": v(-7, 40.15) * mm});
            skLineSegment(sketch, "E2015", {"start": v(-7, 40.15) * mm, "end": v(-7.24, 40.1) * mm});
            skLineSegment(sketch, "E2016", {"start": v(-7.24, 40.1) * mm, "end": v(-7.47, 40.03) * mm});
            skLineSegment(sketch, "E2017", {"start": v(-7.47, 40.03) * mm, "end": v(-7.7, 39.96) * mm});
            skLineSegment(sketch, "E2018", {"start": v(-7.7, 39.96) * mm, "end": v(-7.93, 39.9) * mm});
            skLineSegment(sketch, "E2019", {"start": v(-7.93, 39.9) * mm, "end": v(-8.16, 39.82) * mm});
            skLineSegment(sketch, "E2020", {"start": v(-8.16, 39.82) * mm, "end": v(-8.39, 39.75) * mm});
            skLineSegment(sketch, "E2021", {"start": v(-8.39, 39.75) * mm, "end": v(-8.62, 39.68) * mm});
            skLineSegment(sketch, "E2022", {"start": v(-8.62, 39.68) * mm, "end": v(-8.79, 39.62) * mm});
            skLineSegment(sketch, "E2023", {"start": v(-8.79, 39.62) * mm, "end": v(-8.95, 39.57) * mm});
            skLineSegment(sketch, "E2024", {"start": v(-8.95, 39.57) * mm, "end": v(-9.12, 39.51) * mm});
            skLineSegment(sketch, "E2025", {"start": v(-9.12, 39.51) * mm, "end": v(-9.28, 39.45) * mm});
            skLineSegment(sketch, "E2026", {"start": v(-9.28, 39.45) * mm, "end": v(-9.45, 39.4) * mm});
            skLineSegment(sketch, "E2027", {"start": v(-9.45, 39.4) * mm, "end": v(-9.6, 39.33) * mm});
            skLineSegment(sketch, "E2028", {"start": v(-9.6, 39.33) * mm, "end": v(-9.77, 39.27) * mm});
            skLineSegment(sketch, "E2029", {"start": v(-9.77, 39.27) * mm, "end": v(-9.93, 39.2) * mm});
            skLineSegment(sketch, "E2030", {"start": v(-9.93, 39.2) * mm, "end": v(-10.1, 39.13) * mm});
            skLineSegment(sketch, "E2031", {"start": v(-10.1, 39.13) * mm, "end": v(-10.25, 39.07) * mm});
            skLineSegment(sketch, "E2032", {"start": v(-10.25, 39.07) * mm, "end": v(-10.4, 39) * mm});
            skLineSegment(sketch, "E2033", {"start": v(-10.4, 39) * mm, "end": v(-10.57, 38.93) * mm});
            skLineSegment(sketch, "E2034", {"start": v(-10.57, 38.93) * mm, "end": v(-10.72, 38.85) * mm});
            skLineSegment(sketch, "E2035", {"start": v(-10.72, 38.85) * mm, "end": v(-10.88, 38.78) * mm});
            skLineSegment(sketch, "E2036", {"start": v(-10.88, 38.78) * mm, "end": v(-11.03, 38.7) * mm});
            skLineSegment(sketch, "E2037", {"start": v(-11.03, 38.7) * mm, "end": v(-11.19, 38.63) * mm});
            skLineSegment(sketch, "E2038", {"start": v(-11.19, 38.63) * mm, "end": v(-11.34, 38.55) * mm});
            skLineSegment(sketch, "E2039", {"start": v(-11.34, 38.55) * mm, "end": v(-11.5, 38.47) * mm});
            skLineSegment(sketch, "E2040", {"start": v(-11.5, 38.47) * mm, "end": v(-11.64, 38.39) * mm});
            skLineSegment(sketch, "E2041", {"start": v(-11.64, 38.39) * mm, "end": v(-11.8, 38.3) * mm});
            skLineSegment(sketch, "E2042", {"start": v(-11.8, 38.3) * mm, "end": v(-11.94, 38.22) * mm});
            skLineSegment(sketch, "E2043", {"start": v(-11.94, 38.22) * mm, "end": v(-12.1, 38.14) * mm});
            skLineSegment(sketch, "E2044", {"start": v(-12.1, 38.14) * mm, "end": v(-12.24, 38.05) * mm});
            skLineSegment(sketch, "E2045", {"start": v(-12.24, 38.05) * mm, "end": v(-12.39, 37.96) * mm});
            skLineSegment(sketch, "E2046", {"start": v(-12.39, 37.96) * mm, "end": v(-12.54, 37.87) * mm});
            skLineSegment(sketch, "E2047", {"start": v(-12.54, 37.87) * mm, "end": v(-12.68, 37.78) * mm});
            skLineSegment(sketch, "E2048", {"start": v(-12.68, 37.78) * mm, "end": v(-12.83, 37.68) * mm});
            skLineSegment(sketch, "E2049", {"start": v(-12.83, 37.68) * mm, "end": v(-12.97, 37.59) * mm});
            skLineSegment(sketch, "E2050", {"start": v(-12.97, 37.59) * mm, "end": v(-13.11, 37.49) * mm});
            skLineSegment(sketch, "E2051", {"start": v(-13.11, 37.49) * mm, "end": v(-13.25, 37.4) * mm});
            skLineSegment(sketch, "E2052", {"start": v(-13.25, 37.4) * mm, "end": v(-13.4, 37.3) * mm});
            skLineSegment(sketch, "E2053", {"start": v(-13.4, 37.3) * mm, "end": v(-13.54, 37.19) * mm});
            skLineSegment(sketch, "E2054", {"start": v(-13.54, 37.19) * mm, "end": v(-13.64, 37.1) * mm});
            skLineSegment(sketch, "E2055", {"start": v(-13.64, 37.1) * mm, "end": v(-13.75, 37.03) * mm});
            skLineSegment(sketch, "E2056", {"start": v(-13.75, 37.03) * mm, "end": v(-13.86, 36.94) * mm});
            skLineSegment(sketch, "E2057", {"start": v(-13.86, 36.94) * mm, "end": v(-13.96, 36.86) * mm});
            skLineSegment(sketch, "E2058", {"start": v(-13.96, 36.86) * mm, "end": v(-14.07, 36.77) * mm});
            skLineSegment(sketch, "E2059", {"start": v(-14.07, 36.77) * mm, "end": v(-14.17, 36.69) * mm});
            skLineSegment(sketch, "E2060", {"start": v(-14.17, 36.69) * mm, "end": v(-14.27, 36.6) * mm});
            skLineSegment(sketch, "E2061", {"start": v(-14.27, 36.6) * mm, "end": v(-14.37, 36.5) * mm});
            skLineSegment(sketch, "E2062", {"start": v(-14.37, 36.5) * mm, "end": v(-14.47, 36.42) * mm});
            skLineSegment(sketch, "E2063", {"start": v(-14.47, 36.42) * mm, "end": v(-14.56, 36.32) * mm});
            skLineSegment(sketch, "E2064", {"start": v(-14.56, 36.32) * mm, "end": v(-14.66, 36.23) * mm});
            skLineSegment(sketch, "E2065", {"start": v(-14.66, 36.23) * mm, "end": v(-14.75, 36.13) * mm});
            skLineSegment(sketch, "E2066", {"start": v(-14.75, 36.13) * mm, "end": v(-14.84, 36.04) * mm});
            skLineSegment(sketch, "E2067", {"start": v(-14.84, 36.04) * mm, "end": v(-14.93, 35.94) * mm});
            skLineSegment(sketch, "E2068", {"start": v(-14.93, 35.94) * mm, "end": v(-15.02, 35.84) * mm});
            skLineSegment(sketch, "E2069", {"start": v(-15.02, 35.84) * mm, "end": v(-15.1, 35.74) * mm});
            skLineSegment(sketch, "E2070", {"start": v(-15.1, 35.74) * mm, "end": v(-15.2, 35.63) * mm});
            skLineSegment(sketch, "E2071", {"start": v(-15.2, 35.63) * mm, "end": v(-15.28, 35.53) * mm});
            skLineSegment(sketch, "E2072", {"start": v(-15.28, 35.53) * mm, "end": v(-15.36, 35.42) * mm});
            skLineSegment(sketch, "E2073", {"start": v(-15.36, 35.42) * mm, "end": v(-15.44, 35.32) * mm});
            skLineSegment(sketch, "E2074", {"start": v(-15.44, 35.32) * mm, "end": v(-15.51, 35.2) * mm});
            skLineSegment(sketch, "E2075", {"start": v(-15.51, 35.2) * mm, "end": v(-15.59, 35.1) * mm});
            skLineSegment(sketch, "E2076", {"start": v(-15.59, 35.1) * mm, "end": v(-15.66, 34.98) * mm});
            skLineSegment(sketch, "E2077", {"start": v(-15.66, 34.98) * mm, "end": v(-15.73, 34.87) * mm});
            skLineSegment(sketch, "E2078", {"start": v(-15.73, 34.87) * mm, "end": v(-15.8, 34.75) * mm});
            skLineSegment(sketch, "E2079", {"start": v(-15.8, 34.75) * mm, "end": v(-15.87, 34.63) * mm});
            skLineSegment(sketch, "E2080", {"start": v(-15.87, 34.63) * mm, "end": v(-15.93, 34.51) * mm});
            skLineSegment(sketch, "E2081", {"start": v(-15.93, 34.51) * mm, "end": v(-16, 34.39) * mm});
            skLineSegment(sketch, "E2082", {"start": v(-16, 34.39) * mm, "end": v(-16.05, 34.26) * mm});
            skLineSegment(sketch, "E2083", {"start": v(-16.05, 34.26) * mm, "end": v(-16.1, 34.14) * mm});
            skLineSegment(sketch, "E2084", {"start": v(-16.1, 34.14) * mm, "end": v(-16.16, 34.01) * mm});
            skLineSegment(sketch, "E2085", {"start": v(-16.16, 34.01) * mm, "end": v(-16.21, 33.88) * mm});
            skLineSegment(sketch, "E2086", {"start": v(-16.21, 33.88) * mm, "end": v(-16.22, 33.88) * mm});
            skLineSegment(sketch, "E2087", {"start": v(-16.22, 33.88) * mm, "end": v(-16.23, 33.89) * mm});
            skLineSegment(sketch, "E2088", {"start": v(-16.23, 33.89) * mm, "end": v(-16.24, 33.89) * mm});
            skLineSegment(sketch, "E2089", {"start": v(-16.24, 33.89) * mm, "end": v(-16.25, 33.9) * mm});
            skLineSegment(sketch, "E2090", {"start": v(-16.25, 33.9) * mm, "end": v(-16.26, 33.9) * mm});
            skLineSegment(sketch, "E2091", {"start": v(-16.26, 33.9) * mm, "end": v(-16.27, 33.9) * mm});
            skLineSegment(sketch, "E2092", {"start": v(-16.27, 33.9) * mm, "end": v(-16.28, 33.9) * mm});
            skLineSegment(sketch, "E2093", {"start": v(-16.28, 33.9) * mm, "end": v(-16.29, 33.9) * mm});
            skLineSegment(sketch, "E2094", {"start": v(-16.29, 33.9) * mm, "end": v(-16.3, 33.9) * mm});
            skLineSegment(sketch, "E2095", {"start": v(-16.3, 33.9) * mm, "end": v(-16.31, 33.9) * mm});
            skLineSegment(sketch, "E2096", {"start": v(-16.31, 33.9) * mm, "end": v(-16.32, 33.9) * mm});
            skLineSegment(sketch, "E2097", {"start": v(-16.32, 33.9) * mm, "end": v(-16.33, 33.9) * mm});
            skLineSegment(sketch, "E2098", {"start": v(-16.33, 33.9) * mm, "end": v(-16.34, 33.91) * mm});
            skLineSegment(sketch, "E2099", {"start": v(-16.34, 33.91) * mm, "end": v(-16.35, 33.91) * mm});
            skLineSegment(sketch, "E2100", {"start": v(-16.35, 33.91) * mm, "end": v(-16.35, 33.92) * mm});
            skLineSegment(sketch, "E2101", {"start": v(-16.35, 33.92) * mm, "end": v(-16.36, 33.92) * mm});
            skLineSegment(sketch, "E2102", {"start": v(-16.36, 33.92) * mm, "end": v(-16.37, 33.92) * mm});
            skLineSegment(sketch, "E2103", {"start": v(-16.37, 33.92) * mm, "end": v(-16.38, 33.92) * mm});
            skLineSegment(sketch, "E2104", {"start": v(-16.38, 33.92) * mm, "end": v(-16.37, 34) * mm});
            skLineSegment(sketch, "E2105", {"start": v(-16.37, 34) * mm, "end": v(-16.35, 34.08) * mm});
            skLineSegment(sketch, "E2106", {"start": v(-16.35, 34.08) * mm, "end": v(-16.33, 34.16) * mm});
            skLineSegment(sketch, "E2107", {"start": v(-16.33, 34.16) * mm, "end": v(-16.31, 34.24) * mm});
            skLineSegment(sketch, "E2108", {"start": v(-16.31, 34.24) * mm, "end": v(-16.3, 34.32) * mm});
            skLineSegment(sketch, "E2109", {"start": v(-16.3, 34.32) * mm, "end": v(-16.28, 34.4) * mm});
            skLineSegment(sketch, "E2110", {"start": v(-16.28, 34.4) * mm, "end": v(-16.26, 34.48) * mm});
            skLineSegment(sketch, "E2111", {"start": v(-16.26, 34.48) * mm, "end": v(-16.25, 34.57) * mm});
            skLineSegment(sketch, "E2112", {"start": v(-16.25, 34.57) * mm, "end": v(-16.23, 34.65) * mm});
            skLineSegment(sketch, "E2113", {"start": v(-16.23, 34.65) * mm, "end": v(-16.21, 34.73) * mm});
            skLineSegment(sketch, "E2114", {"start": v(-16.21, 34.73) * mm, "end": v(-16.2, 34.8) * mm});
            skLineSegment(sketch, "E2115", {"start": v(-16.2, 34.8) * mm, "end": v(-16.18, 34.89) * mm});
            skLineSegment(sketch, "E2116", {"start": v(-16.18, 34.89) * mm, "end": v(-16.16, 34.97) * mm});
            skLineSegment(sketch, "E2117", {"start": v(-16.16, 34.97) * mm, "end": v(-16.14, 35.05) * mm});
            skLineSegment(sketch, "E2118", {"start": v(-16.14, 35.05) * mm, "end": v(-16.13, 35.13) * mm});
            skLineSegment(sketch, "E2119", {"start": v(-16.13, 35.13) * mm, "end": v(-16.11, 35.2) * mm});
            skLineSegment(sketch, "E2120", {"start": v(-16.11, 35.2) * mm, "end": v(-16.1, 35.29) * mm});
            skLineSegment(sketch, "E2121", {"start": v(-16.1, 35.29) * mm, "end": v(-16.08, 35.37) * mm});
            skLineSegment(sketch, "E2122", {"start": v(-16.08, 35.37) * mm, "end": v(-16.06, 35.45) * mm});
            skLineSegment(sketch, "E2123", {"start": v(-16.06, 35.45) * mm, "end": v(-16.04, 35.53) * mm});
            skLineSegment(sketch, "E2124", {"start": v(-16.04, 35.53) * mm, "end": v(-16.02, 35.6) * mm});
            skLineSegment(sketch, "E2125", {"start": v(-16.02, 35.6) * mm, "end": v(-16, 35.69) * mm});
            skLineSegment(sketch, "E2126", {"start": v(-16, 35.69) * mm, "end": v(-15.98, 35.77) * mm});
            skLineSegment(sketch, "E2127", {"start": v(-15.98, 35.77) * mm, "end": v(-15.96, 35.85) * mm});
            skLineSegment(sketch, "E2128", {"start": v(-15.96, 35.85) * mm, "end": v(-15.94, 35.93) * mm});
            skLineSegment(sketch, "E2129", {"start": v(-15.94, 35.93) * mm, "end": v(-15.92, 36) * mm});
            skLineSegment(sketch, "E2130", {"start": v(-15.92, 36) * mm, "end": v(-15.9, 36.09) * mm});
            skLineSegment(sketch, "E2131", {"start": v(-15.9, 36.09) * mm, "end": v(-15.88, 36.16) * mm});
            skLineSegment(sketch, "E2132", {"start": v(-15.88, 36.16) * mm, "end": v(-15.86, 36.24) * mm});
            skLineSegment(sketch, "E2133", {"start": v(-15.86, 36.24) * mm, "end": v(-15.83, 36.32) * mm});
            skLineSegment(sketch, "E2134", {"start": v(-15.83, 36.32) * mm, "end": v(-15.81, 36.4) * mm});
            skLineSegment(sketch, "E2135", {"start": v(-15.81, 36.4) * mm, "end": v(-15.79, 36.48) * mm});
            skLineSegment(sketch, "E2136", {"start": v(-15.79, 36.48) * mm, "end": v(-15.73, 36.67) * mm});
            skLineSegment(sketch, "E2137", {"start": v(-15.73, 36.67) * mm, "end": v(-15.66, 36.86) * mm});
            skLineSegment(sketch, "E2138", {"start": v(-15.66, 36.86) * mm, "end": v(-15.6, 37.05) * mm});
            skLineSegment(sketch, "E2139", {"start": v(-15.6, 37.05) * mm, "end": v(-15.53, 37.23) * mm});
            skLineSegment(sketch, "E2140", {"start": v(-15.53, 37.23) * mm, "end": v(-15.46, 37.42) * mm});
            skLineSegment(sketch, "E2141", {"start": v(-15.46, 37.42) * mm, "end": v(-15.39, 37.6) * mm});
            skLineSegment(sketch, "E2142", {"start": v(-15.39, 37.6) * mm, "end": v(-15.31, 37.78) * mm});
            skLineSegment(sketch, "E2143", {"start": v(-15.31, 37.78) * mm, "end": v(-15.23, 37.97) * mm});
            skLineSegment(sketch, "E2144", {"start": v(-15.23, 37.97) * mm, "end": v(-15.16, 38.15) * mm});
            skLineSegment(sketch, "E2145", {"start": v(-15.16, 38.15) * mm, "end": v(-15.07, 38.32) * mm});
            skLineSegment(sketch, "E2146", {"start": v(-15.07, 38.32) * mm, "end": v(-14.99, 38.5) * mm});
            skLineSegment(sketch, "E2147", {"start": v(-14.99, 38.5) * mm, "end": v(-14.9, 38.68) * mm});
            skLineSegment(sketch, "E2148", {"start": v(-14.9, 38.68) * mm, "end": v(-14.81, 38.85) * mm});
            skLineSegment(sketch, "E2149", {"start": v(-14.81, 38.85) * mm, "end": v(-14.72, 39.03) * mm});
            skLineSegment(sketch, "E2150", {"start": v(-14.72, 39.03) * mm, "end": v(-14.63, 39.2) * mm});
            skLineSegment(sketch, "E2151", {"start": v(-14.63, 39.2) * mm, "end": v(-14.53, 39.37) * mm});
            skLineSegment(sketch, "E2152", {"start": v(-14.53, 39.37) * mm, "end": v(-14.44, 39.54) * mm});
            skLineSegment(sketch, "E2153", {"start": v(-14.44, 39.54) * mm, "end": v(-14.34, 39.71) * mm});
            skLineSegment(sketch, "E2154", {"start": v(-14.34, 39.71) * mm, "end": v(-14.24, 39.88) * mm});
            skLineSegment(sketch, "E2155", {"start": v(-14.24, 39.88) * mm, "end": v(-14.13, 40.05) * mm});
            skLineSegment(sketch, "E2156", {"start": v(-14.13, 40.05) * mm, "end": v(-14.03, 40.21) * mm});
            skLineSegment(sketch, "E2157", {"start": v(-14.03, 40.21) * mm, "end": v(-13.92, 40.38) * mm});
            skLineSegment(sketch, "E2158", {"start": v(-13.92, 40.38) * mm, "end": v(-13.8, 40.54) * mm});
            skLineSegment(sketch, "E2159", {"start": v(-13.8, 40.54) * mm, "end": v(-13.7, 40.7) * mm});
            skLineSegment(sketch, "E2160", {"start": v(-13.7, 40.7) * mm, "end": v(-13.58, 40.86) * mm});
            skLineSegment(sketch, "E2161", {"start": v(-13.58, 40.86) * mm, "end": v(-13.46, 41.02) * mm});
            skLineSegment(sketch, "E2162", {"start": v(-13.46, 41.02) * mm, "end": v(-13.34, 41.18) * mm});
            skLineSegment(sketch, "E2163", {"start": v(-13.34, 41.18) * mm, "end": v(-13.22, 41.34) * mm});
            skLineSegment(sketch, "E2164", {"start": v(-13.22, 41.34) * mm, "end": v(-13.1, 41.5) * mm});
            skLineSegment(sketch, "E2165", {"start": v(-13.1, 41.5) * mm, "end": v(-12.98, 41.66) * mm});
            skLineSegment(sketch, "E2166", {"start": v(-12.98, 41.66) * mm, "end": v(-12.85, 41.81) * mm});
            skLineSegment(sketch, "E2167", {"start": v(-12.85, 41.81) * mm, "end": v(-12.72, 41.97) * mm});
            skLineSegment(sketch, "E2168", {"start": v(-12.72, 41.97) * mm, "end": v(-12.58, 42.13) * mm});
            skLineSegment(sketch, "E2169", {"start": v(-12.58, 42.13) * mm, "end": v(-12.43, 42.3) * mm});
            skLineSegment(sketch, "E2170", {"start": v(-12.43, 42.3) * mm, "end": v(-12.29, 42.47) * mm});
            skLineSegment(sketch, "E2171", {"start": v(-12.29, 42.47) * mm, "end": v(-12.14, 42.63) * mm});
            skLineSegment(sketch, "E2172", {"start": v(-12.14, 42.63) * mm, "end": v(-11.99, 42.79) * mm});
            skLineSegment(sketch, "E2173", {"start": v(-11.99, 42.79) * mm, "end": v(-11.84, 42.95) * mm});
            skLineSegment(sketch, "E2174", {"start": v(-11.84, 42.95) * mm, "end": v(-11.68, 43.1) * mm});
            skLineSegment(sketch, "E2175", {"start": v(-11.68, 43.1) * mm, "end": v(-11.53, 43.26) * mm});
            skLineSegment(sketch, "E2176", {"start": v(-11.53, 43.26) * mm, "end": v(-11.38, 43.4) * mm});
            skLineSegment(sketch, "E2177", {"start": v(-11.38, 43.4) * mm, "end": v(-11.22, 43.56) * mm});
            skLineSegment(sketch, "E2178", {"start": v(-11.22, 43.56) * mm, "end": v(-11.06, 43.7) * mm});
            skLineSegment(sketch, "E2179", {"start": v(-11.06, 43.7) * mm, "end": v(-10.9, 43.85) * mm});
            skLineSegment(sketch, "E2180", {"start": v(-10.9, 43.85) * mm, "end": v(-10.74, 44) * mm});
            skLineSegment(sketch, "E2181", {"start": v(-10.74, 44) * mm, "end": v(-10.57, 44.14) * mm});
            skLineSegment(sketch, "E2182", {"start": v(-10.57, 44.14) * mm, "end": v(-10.4, 44.27) * mm});
            skLineSegment(sketch, "E2183", {"start": v(-10.4, 44.27) * mm, "end": v(-10.24, 44.41) * mm});
            skLineSegment(sketch, "E2184", {"start": v(-10.24, 44.41) * mm, "end": v(-10.07, 44.54) * mm});
            skLineSegment(sketch, "E2185", {"start": v(-10.07, 44.54) * mm, "end": v(-9.9, 44.68) * mm});
            skLineSegment(sketch, "E2186", {"start": v(-9.9, 44.68) * mm, "end": v(-9.73, 44.8) * mm});
            skLineSegment(sketch, "E2187", {"start": v(-9.73, 44.8) * mm, "end": v(-9.55, 44.93) * mm});
            skLineSegment(sketch, "E2188", {"start": v(-9.55, 44.93) * mm, "end": v(-9.38, 45.06) * mm});
            skLineSegment(sketch, "E2189", {"start": v(-9.38, 45.06) * mm, "end": v(-9.2, 45.18) * mm});
            skLineSegment(sketch, "E2190", {"start": v(-9.2, 45.18) * mm, "end": v(-9.02, 45.3) * mm});
            skLineSegment(sketch, "E2191", {"start": v(-9.02, 45.3) * mm, "end": v(-8.83, 45.41) * mm});
            skLineSegment(sketch, "E2192", {"start": v(-8.83, 45.41) * mm, "end": v(-8.65, 45.53) * mm});
            skLineSegment(sketch, "E2193", {"start": v(-8.65, 45.53) * mm, "end": v(-8.46, 45.64) * mm});
            skLineSegment(sketch, "E2194", {"start": v(-8.46, 45.64) * mm, "end": v(-8.28, 45.75) * mm});
            skLineSegment(sketch, "E2195", {"start": v(-8.28, 45.75) * mm, "end": v(-8.09, 45.85) * mm});
            skLineSegment(sketch, "E2196", {"start": v(-8.09, 45.85) * mm, "end": v(-7.9, 45.95) * mm});
            skLineSegment(sketch, "E2197", {"start": v(-7.9, 45.95) * mm, "end": v(-7.7, 46.05) * mm});
            skLineSegment(sketch, "E2198", {"start": v(-7.7, 46.05) * mm, "end": v(-7.5, 46.15) * mm});
            skLineSegment(sketch, "E2199", {"start": v(-7.5, 46.15) * mm, "end": v(-7.3, 46.25) * mm});
            skLineSegment(sketch, "E2200", {"start": v(-7.3, 46.25) * mm, "end": v(-7.07, 46.35) * mm});
            skLineSegment(sketch, "E2201", {"start": v(-7.07, 46.35) * mm, "end": v(-6.83, 46.46) * mm});
            skLineSegment(sketch, "E2202", {"start": v(-6.83, 46.46) * mm, "end": v(-6.6, 46.56) * mm});
            skLineSegment(sketch, "E2203", {"start": v(-6.6, 46.56) * mm, "end": v(-6.36, 46.66) * mm});
            skLineSegment(sketch, "E2204", {"start": v(-6.36, 46.66) * mm, "end": v(-6.12, 46.75) * mm});
            skLineSegment(sketch, "E2205", {"start": v(-6.12, 46.75) * mm, "end": v(-5.88, 46.84) * mm});
            skLineSegment(sketch, "E2206", {"start": v(-5.88, 46.84) * mm, "end": v(-5.64, 46.93) * mm});
            skLineSegment(sketch, "E2207", {"start": v(-5.64, 46.93) * mm, "end": v(-5.4, 47.02) * mm});
            skLineSegment(sketch, "E2208", {"start": v(-5.4, 47.02) * mm, "end": v(-5.16, 47.1) * mm});
            skLineSegment(sketch, "E2209", {"start": v(-5.16, 47.1) * mm, "end": v(-4.92, 47.18) * mm});
            skLineSegment(sketch, "E2210", {"start": v(-4.92, 47.18) * mm, "end": v(-4.67, 47.25) * mm});
            skLineSegment(sketch, "E2211", {"start": v(-4.67, 47.25) * mm, "end": v(-4.43, 47.32) * mm});
            skLineSegment(sketch, "E2212", {"start": v(-4.43, 47.32) * mm, "end": v(-4.19, 47.39) * mm});
            skLineSegment(sketch, "E2213", {"start": v(-4.19, 47.39) * mm, "end": v(-3.94, 47.45) * mm});
            skLineSegment(sketch, "E2214", {"start": v(-3.94, 47.45) * mm, "end": v(-3.7, 47.5) * mm});
            skLineSegment(sketch, "E2215", {"start": v(-3.7, 47.5) * mm, "end": v(-3.45, 47.56) * mm});
            skLineSegment(sketch, "E2216", {"start": v(-3.45, 47.56) * mm, "end": v(-3.2, 47.62) * mm});
            skLineSegment(sketch, "E2217", {"start": v(-3.2, 47.62) * mm, "end": v(-2.95, 47.66) * mm});
            skLineSegment(sketch, "E2218", {"start": v(-2.95, 47.66) * mm, "end": v(-2.7, 47.7) * mm});
            skLineSegment(sketch, "E2219", {"start": v(-2.7, 47.7) * mm, "end": v(-2.45, 47.75) * mm});
            skLineSegment(sketch, "E2220", {"start": v(-2.45, 47.75) * mm, "end": v(-2.2, 47.78) * mm});
            skLineSegment(sketch, "E2221", {"start": v(-2.2, 47.78) * mm, "end": v(-1.94, 47.81) * mm});
            skLineSegment(sketch, "E2222", {"start": v(-1.94, 47.81) * mm, "end": v(-1.7, 47.84) * mm});
            skLineSegment(sketch, "E2223", {"start": v(-1.7, 47.84) * mm, "end": v(-1.44, 47.86) * mm});
            skLineSegment(sketch, "E2224", {"start": v(-1.44, 47.86) * mm, "end": v(-1.18, 47.88) * mm});
            skLineSegment(sketch, "E2225", {"start": v(-1.18, 47.88) * mm, "end": v(-0.93, 47.9) * mm});
            skLineSegment(sketch, "E2226", {"start": v(-0.93, 47.9) * mm, "end": v(-0.67, 47.9) * mm});
            skLineSegment(sketch, "E2227", {"start": v(-0.67, 47.9) * mm, "end": v(-0.41, 47.91) * mm});
            skLineSegment(sketch, "E2228", {"start": v(-0.41, 47.91) * mm, "end": v(-0.15, 47.91) * mm});
            skLineSegment(sketch, "E2229", {"start": v(-0.15, 47.91) * mm, "end": v(0.1, 47.91) * mm});
            skLineSegment(sketch, "E2230", {"start": v(0.1, 47.91) * mm, "end": v(0.37, 47.9) * mm});
            skLineSegment(sketch, "E2231", {"start": v(0.37, 47.9) * mm, "end": v(0.63, 47.9) * mm});
            skLineSegment(sketch, "E2232", {"start": v(0.63, 47.9) * mm, "end": v(0.78, 47.88) * mm});
            skLineSegment(sketch, "E2233", {"start": v(0.78, 47.88) * mm, "end": v(0.93, 47.86) * mm});
            skLineSegment(sketch, "E2234", {"start": v(0.93, 47.86) * mm, "end": v(1.07, 47.83) * mm});
            skLineSegment(sketch, "E2235", {"start": v(1.07, 47.83) * mm, "end": v(1.2, 47.8) * mm});
            skLineSegment(sketch, "E2236", {"start": v(1.2, 47.8) * mm, "end": v(1.34, 47.76) * mm});
            skLineSegment(sketch, "E2237", {"start": v(1.34, 47.76) * mm, "end": v(1.47, 47.71) * mm});
            skLineSegment(sketch, "E2238", {"start": v(1.47, 47.71) * mm, "end": v(1.6, 47.66) * mm});
            skLineSegment(sketch, "E2239", {"start": v(1.6, 47.66) * mm, "end": v(1.72, 47.6) * mm});
            skLineSegment(sketch, "E2240", {"start": v(1.72, 47.6) * mm, "end": v(1.83, 47.53) * mm});
            skLineSegment(sketch, "E2241", {"start": v(1.83, 47.53) * mm, "end": v(1.94, 47.46) * mm});
            skLineSegment(sketch, "E2242", {"start": v(1.94, 47.46) * mm, "end": v(2.04, 47.38) * mm});
            skLineSegment(sketch, "E2243", {"start": v(2.04, 47.38) * mm, "end": v(2.14, 47.3) * mm});
            skLineSegment(sketch, "E2244", {"start": v(2.14, 47.3) * mm, "end": v(2.23, 47.2) * mm});
            skLineSegment(sketch, "E2245", {"start": v(2.23, 47.2) * mm, "end": v(2.32, 47.11) * mm});
            skLineSegment(sketch, "E2246", {"start": v(2.32, 47.11) * mm, "end": v(2.4, 47.02) * mm});
            skLineSegment(sketch, "E2247", {"start": v(2.4, 47.02) * mm, "end": v(2.47, 46.91) * mm});
            skLineSegment(sketch, "E2248", {"start": v(2.47, 46.91) * mm, "end": v(2.54, 46.8) * mm});
            skLineSegment(sketch, "E2249", {"start": v(2.54, 46.8) * mm, "end": v(2.6, 46.69) * mm});
            skLineSegment(sketch, "E2250", {"start": v(2.6, 46.69) * mm, "end": v(2.66, 46.57) * mm});
            skLineSegment(sketch, "E2251", {"start": v(2.66, 46.57) * mm, "end": v(2.7, 46.45) * mm});
            skLineSegment(sketch, "E2252", {"start": v(2.7, 46.45) * mm, "end": v(2.75, 46.32) * mm});
            skLineSegment(sketch, "E2253", {"start": v(2.75, 46.32) * mm, "end": v(2.78, 46.2) * mm});
            skLineSegment(sketch, "E2254", {"start": v(2.78, 46.2) * mm, "end": v(2.8, 46.06) * mm});
            skLineSegment(sketch, "E2255", {"start": v(2.8, 46.06) * mm, "end": v(2.83, 45.92) * mm});
            skLineSegment(sketch, "E2256", {"start": v(2.83, 45.92) * mm, "end": v(2.84, 45.78) * mm});
            skLineSegment(sketch, "E2257", {"start": v(2.84, 45.78) * mm, "end": v(2.84, 45.63) * mm});
            skLineSegment(sketch, "E2258", {"start": v(2.84, 45.63) * mm, "end": v(2.84, 45.49) * mm});
            skLineSegment(sketch, "E2259", {"start": v(2.84, 45.49) * mm, "end": v(2.83, 45.34) * mm});
            skLineSegment(sketch, "E2260", {"start": v(2.83, 45.34) * mm, "end": v(2.8, 45.18) * mm});
            skLineSegment(sketch, "E2261", {"start": v(2.8, 45.18) * mm, "end": v(2.78, 45.03) * mm});
            skLineSegment(sketch, "E2262", {"start": v(2.78, 45.03) * mm, "end": v(2.74, 44.87) * mm});
            skLineSegment(sketch, "E2263", {"start": v(2.74, 44.87) * mm, "end": v(2.7, 44.71) * mm});
            skLineSegment(sketch, "E2264", {"start": v(2.7, 44.71) * mm, "end": v(2.66, 44.59) * mm});
            skLineSegment(sketch, "E2265", {"start": v(2.66, 44.59) * mm, "end": v(2.62, 44.46) * mm});
            skLineSegment(sketch, "E2266", {"start": v(2.62, 44.46) * mm, "end": v(2.58, 44.34) * mm});
            skLineSegment(sketch, "E2267", {"start": v(2.58, 44.34) * mm, "end": v(2.54, 44.22) * mm});
            skLineSegment(sketch, "E2268", {"start": v(2.54, 44.22) * mm, "end": v(2.5, 44.1) * mm});
            skLineSegment(sketch, "E2269", {"start": v(2.5, 44.1) * mm, "end": v(2.46, 43.97) * mm});
            skLineSegment(sketch, "E2270", {"start": v(2.46, 43.97) * mm, "end": v(2.41, 43.85) * mm});
            skLineSegment(sketch, "E2271", {"start": v(2.41, 43.85) * mm, "end": v(2.37, 43.73) * mm});
            skLineSegment(sketch, "E2272", {"start": v(2.37, 43.73) * mm, "end": v(2.33, 43.6) * mm});
            skLineSegment(sketch, "E2273", {"start": v(2.33, 43.6) * mm, "end": v(2.28, 43.48) * mm});
            skLineSegment(sketch, "E2274", {"start": v(2.28, 43.48) * mm, "end": v(2.23, 43.36) * mm});
            skLineSegment(sketch, "E2275", {"start": v(2.23, 43.36) * mm, "end": v(2.19, 43.24) * mm});
            skLineSegment(sketch, "E2276", {"start": v(2.19, 43.24) * mm, "end": v(2.14, 43.12) * mm});
            skLineSegment(sketch, "E2277", {"start": v(2.14, 43.12) * mm, "end": v(2.1, 43) * mm});
            skLineSegment(sketch, "E2278", {"start": v(2.1, 43) * mm, "end": v(2.05, 42.87) * mm});
            skLineSegment(sketch, "E2279", {"start": v(2.05, 42.87) * mm, "end": v(2, 42.75) * mm});
            skLineSegment(sketch, "E2280", {"start": v(2, 42.75) * mm, "end": v(1.95, 42.63) * mm});
            skLineSegment(sketch, "E2281", {"start": v(1.95, 42.63) * mm, "end": v(1.9, 42.5) * mm});
            skLineSegment(sketch, "E2282", {"start": v(1.9, 42.5) * mm, "end": v(1.86, 42.39) * mm});
            skLineSegment(sketch, "E2283", {"start": v(1.86, 42.39) * mm, "end": v(1.8, 42.27) * mm});
            skLineSegment(sketch, "E2284", {"start": v(1.8, 42.27) * mm, "end": v(1.76, 42.14) * mm});
            skLineSegment(sketch, "E2285", {"start": v(1.76, 42.14) * mm, "end": v(1.7, 42.02) * mm});
            skLineSegment(sketch, "E2286", {"start": v(1.7, 42.02) * mm, "end": v(1.66, 41.9) * mm});
            skLineSegment(sketch, "E2287", {"start": v(1.66, 41.9) * mm, "end": v(1.61, 41.78) * mm});
            skLineSegment(sketch, "E2288", {"start": v(1.61, 41.78) * mm, "end": v(1.56, 41.65) * mm});
            skLineSegment(sketch, "E2289", {"start": v(1.56, 41.65) * mm, "end": v(1.51, 41.53) * mm});
            skLineSegment(sketch, "E2290", {"start": v(1.51, 41.53) * mm, "end": v(1.46, 41.4) * mm});
            skLineSegment(sketch, "E2291", {"start": v(1.46, 41.4) * mm, "end": v(1.42, 41.29) * mm});
            skLineSegment(sketch, "E2292", {"start": v(1.42, 41.29) * mm, "end": v(1.37, 41.16) * mm});
            skLineSegment(sketch, "E2293", {"start": v(1.37, 41.16) * mm, "end": v(1.32, 41.04) * mm});
            skLineSegment(sketch, "E2294", {"start": v(1.32, 41.04) * mm, "end": v(1.27, 40.92) * mm});
            skLineSegment(sketch, "E2295", {"start": v(1.27, 40.92) * mm, "end": v(1.22, 40.8) * mm});
            skLineSegment(sketch, "E2296", {"start": v(-0.24, 23.31) * mm, "end": v(-0.07, 23.74) * mm});
            skLineSegment(sketch, "E2297", {"start": v(-0.07, 23.74) * mm, "end": v(0.09, 24.16) * mm});
            skLineSegment(sketch, "E2298", {"start": v(0.09, 24.16) * mm, "end": v(0.25, 24.59) * mm});
            skLineSegment(sketch, "E2299", {"start": v(0.25, 24.59) * mm, "end": v(0.4, 25) * mm});
            skLineSegment(sketch, "E2300", {"start": v(0.4, 25) * mm, "end": v(0.57, 25.43) * mm});
            skLineSegment(sketch, "E2301", {"start": v(0.57, 25.43) * mm, "end": v(0.73, 25.85) * mm});
            skLineSegment(sketch, "E2302", {"start": v(0.73, 25.85) * mm, "end": v(0.9, 26.27) * mm});
            skLineSegment(sketch, "E2303", {"start": v(0.9, 26.27) * mm, "end": v(1.05, 26.7) * mm});
            skLineSegment(sketch, "E2304", {"start": v(1.05, 26.7) * mm, "end": v(1.21, 27.11) * mm});
            skLineSegment(sketch, "E2305", {"start": v(1.21, 27.11) * mm, "end": v(1.37, 27.53) * mm});
            skLineSegment(sketch, "E2306", {"start": v(1.37, 27.53) * mm, "end": v(1.53, 27.95) * mm});
            skLineSegment(sketch, "E2307", {"start": v(1.53, 27.95) * mm, "end": v(1.69, 28.37) * mm});
            skLineSegment(sketch, "E2308", {"start": v(1.69, 28.37) * mm, "end": v(1.85, 28.8) * mm});
            skLineSegment(sketch, "E2309", {"start": v(1.85, 28.8) * mm, "end": v(2, 29.2) * mm});
            skLineSegment(sketch, "E2310", {"start": v(2, 29.2) * mm, "end": v(2.17, 29.63) * mm});
            skLineSegment(sketch, "E2311", {"start": v(2.17, 29.63) * mm, "end": v(2.32, 30.05) * mm});
            skLineSegment(sketch, "E2312", {"start": v(2.32, 30.05) * mm, "end": v(2.48, 30.46) * mm});
            skLineSegment(sketch, "E2313", {"start": v(2.48, 30.46) * mm, "end": v(2.64, 30.88) * mm});
            skLineSegment(sketch, "E2314", {"start": v(2.64, 30.88) * mm, "end": v(2.8, 31.3) * mm});
            skLineSegment(sketch, "E2315", {"start": v(2.8, 31.3) * mm, "end": v(2.96, 31.72) * mm});
            skLineSegment(sketch, "E2316", {"start": v(2.96, 31.72) * mm, "end": v(3.12, 32.13) * mm});
            skLineSegment(sketch, "E2317", {"start": v(3.12, 32.13) * mm, "end": v(3.28, 32.55) * mm});
            skLineSegment(sketch, "E2318", {"start": v(3.28, 32.55) * mm, "end": v(3.44, 32.97) * mm});
            skLineSegment(sketch, "E2319", {"start": v(3.44, 32.97) * mm, "end": v(3.6, 33.38) * mm});
            skLineSegment(sketch, "E2320", {"start": v(3.6, 33.38) * mm, "end": v(3.75, 33.8) * mm});
            skLineSegment(sketch, "E2321", {"start": v(3.75, 33.8) * mm, "end": v(3.91, 34.22) * mm});
            skLineSegment(sketch, "E2322", {"start": v(3.91, 34.22) * mm, "end": v(4.07, 34.64) * mm});
            skLineSegment(sketch, "E2323", {"start": v(4.07, 34.64) * mm, "end": v(4.23, 35.05) * mm});
            skLineSegment(sketch, "E2324", {"start": v(4.23, 35.05) * mm, "end": v(4.39, 35.47) * mm});
            skLineSegment(sketch, "E2325", {"start": v(4.39, 35.47) * mm, "end": v(4.55, 35.89) * mm});
            skLineSegment(sketch, "E2326", {"start": v(4.55, 35.89) * mm, "end": v(4.7, 36.3) * mm});
            skLineSegment(sketch, "E2327", {"start": v(4.7, 36.3) * mm, "end": v(4.86, 36.73) * mm});
            skLineSegment(sketch, "E2328", {"start": v(4.86, 36.73) * mm, "end": v(5.01, 36.62) * mm});
            skLineSegment(sketch, "E2329", {"start": v(5.01, 36.62) * mm, "end": v(5.16, 36.51) * mm});
            skLineSegment(sketch, "E2330", {"start": v(5.16, 36.51) * mm, "end": v(5.3, 36.4) * mm});
            skLineSegment(sketch, "E2331", {"start": v(5.3, 36.4) * mm, "end": v(5.44, 36.3) * mm});
            skLineSegment(sketch, "E2332", {"start": v(5.44, 36.3) * mm, "end": v(5.57, 36.18) * mm});
            skLineSegment(sketch, "E2333", {"start": v(5.57, 36.18) * mm, "end": v(5.7, 36.07) * mm});
            skLineSegment(sketch, "E2334", {"start": v(5.7, 36.07) * mm, "end": v(5.84, 35.95) * mm});
            skLineSegment(sketch, "E2335", {"start": v(5.84, 35.95) * mm, "end": v(5.96, 35.83) * mm});
            skLineSegment(sketch, "E2336", {"start": v(5.96, 35.83) * mm, "end": v(6.08, 35.7) * mm});
            skLineSegment(sketch, "E2337", {"start": v(6.08, 35.7) * mm, "end": v(6.2, 35.59) * mm});
            skLineSegment(sketch, "E2338", {"start": v(6.2, 35.59) * mm, "end": v(6.32, 35.46) * mm});
            skLineSegment(sketch, "E2339", {"start": v(6.32, 35.46) * mm, "end": v(6.43, 35.33) * mm});
            skLineSegment(sketch, "E2340", {"start": v(6.43, 35.33) * mm, "end": v(6.54, 35.2) * mm});
            skLineSegment(sketch, "E2341", {"start": v(6.54, 35.2) * mm, "end": v(6.64, 35.07) * mm});
            skLineSegment(sketch, "E2342", {"start": v(6.64, 35.07) * mm, "end": v(6.75, 34.94) * mm});
            skLineSegment(sketch, "E2343", {"start": v(6.75, 34.94) * mm, "end": v(6.84, 34.8) * mm});
            skLineSegment(sketch, "E2344", {"start": v(6.84, 34.8) * mm, "end": v(6.94, 34.66) * mm});
            skLineSegment(sketch, "E2345", {"start": v(6.94, 34.66) * mm, "end": v(7.03, 34.52) * mm});
            skLineSegment(sketch, "E2346", {"start": v(7.03, 34.52) * mm, "end": v(7.11, 34.38) * mm});
            skLineSegment(sketch, "E2347", {"start": v(7.11, 34.38) * mm, "end": v(7.2, 34.23) * mm});
            skLineSegment(sketch, "E2348", {"start": v(7.2, 34.23) * mm, "end": v(7.27, 34.08) * mm});
            skLineSegment(sketch, "E2349", {"start": v(7.27, 34.08) * mm, "end": v(7.34, 33.93) * mm});
            skLineSegment(sketch, "E2350", {"start": v(7.34, 33.93) * mm, "end": v(7.41, 33.77) * mm});
            skLineSegment(sketch, "E2351", {"start": v(7.41, 33.77) * mm, "end": v(7.48, 33.61) * mm});
            skLineSegment(sketch, "E2352", {"start": v(7.48, 33.61) * mm, "end": v(7.54, 33.45) * mm});
            skLineSegment(sketch, "E2353", {"start": v(7.54, 33.45) * mm, "end": v(7.6, 33.29) * mm});
            skLineSegment(sketch, "E2354", {"start": v(7.6, 33.29) * mm, "end": v(7.65, 33.12) * mm});
            skLineSegment(sketch, "E2355", {"start": v(7.65, 33.12) * mm, "end": v(7.7, 32.95) * mm});
            skLineSegment(sketch, "E2356", {"start": v(7.7, 32.95) * mm, "end": v(7.74, 32.78) * mm});
            skLineSegment(sketch, "E2357", {"start": v(7.74, 32.78) * mm, "end": v(7.78, 32.6) * mm});
            skLineSegment(sketch, "E2358", {"start": v(7.78, 32.6) * mm, "end": v(7.8, 32.42) * mm});
            skLineSegment(sketch, "E2359", {"start": v(7.8, 32.42) * mm, "end": v(7.84, 32.23) * mm});
            skLineSegment(sketch, "E2360", {"start": v(7.84, 32.23) * mm, "end": v(7.87, 32.01) * mm});
            skLineSegment(sketch, "E2361", {"start": v(7.87, 32.01) * mm, "end": v(7.89, 31.8) * mm});
            skLineSegment(sketch, "E2362", {"start": v(7.89, 31.8) * mm, "end": v(7.9, 31.58) * mm});
            skLineSegment(sketch, "E2363", {"start": v(7.9, 31.58) * mm, "end": v(7.91, 31.36) * mm});
            skLineSegment(sketch, "E2364", {"start": v(7.91, 31.36) * mm, "end": v(7.92, 31.15) * mm});
            skLineSegment(sketch, "E2365", {"start": v(7.92, 31.15) * mm, "end": v(7.91, 30.94) * mm});
            skLineSegment(sketch, "E2366", {"start": v(7.91, 30.94) * mm, "end": v(7.9, 30.73) * mm});
            skLineSegment(sketch, "E2367", {"start": v(7.9, 30.73) * mm, "end": v(7.89, 30.53) * mm});
            skLineSegment(sketch, "E2368", {"start": v(7.89, 30.53) * mm, "end": v(7.86, 30.32) * mm});
            skLineSegment(sketch, "E2369", {"start": v(7.86, 30.32) * mm, "end": v(7.84, 30.12) * mm});
            skLineSegment(sketch, "E2370", {"start": v(7.84, 30.12) * mm, "end": v(7.8, 29.92) * mm});
            skLineSegment(sketch, "E2371", {"start": v(7.8, 29.92) * mm, "end": v(7.76, 29.72) * mm});
            skLineSegment(sketch, "E2372", {"start": v(7.76, 29.72) * mm, "end": v(7.72, 29.53) * mm});
            skLineSegment(sketch, "E2373", {"start": v(7.72, 29.53) * mm, "end": v(7.67, 29.33) * mm});
            skLineSegment(sketch, "E2374", {"start": v(7.67, 29.33) * mm, "end": v(7.61, 29.14) * mm});
            skLineSegment(sketch, "E2375", {"start": v(7.61, 29.14) * mm, "end": v(7.55, 28.95) * mm});
            skLineSegment(sketch, "E2376", {"start": v(7.55, 28.95) * mm, "end": v(7.48, 28.76) * mm});
            skLineSegment(sketch, "E2377", {"start": v(7.48, 28.76) * mm, "end": v(7.4, 28.57) * mm});
            skLineSegment(sketch, "E2378", {"start": v(7.4, 28.57) * mm, "end": v(7.33, 28.39) * mm});
            skLineSegment(sketch, "E2379", {"start": v(7.33, 28.39) * mm, "end": v(7.25, 28.2) * mm});
            skLineSegment(sketch, "E2380", {"start": v(7.25, 28.2) * mm, "end": v(7.16, 28.02) * mm});
            skLineSegment(sketch, "E2381", {"start": v(7.16, 28.02) * mm, "end": v(7.06, 27.84) * mm});
            skLineSegment(sketch, "E2382", {"start": v(7.06, 27.84) * mm, "end": v(6.97, 27.66) * mm});
            skLineSegment(sketch, "E2383", {"start": v(6.97, 27.66) * mm, "end": v(6.86, 27.48) * mm});
            skLineSegment(sketch, "E2384", {"start": v(6.86, 27.48) * mm, "end": v(6.75, 27.3) * mm});
            skLineSegment(sketch, "E2385", {"start": v(6.75, 27.3) * mm, "end": v(6.64, 27.13) * mm});
            skLineSegment(sketch, "E2386", {"start": v(6.64, 27.13) * mm, "end": v(6.52, 26.96) * mm});
            skLineSegment(sketch, "E2387", {"start": v(6.52, 26.96) * mm, "end": v(6.4, 26.79) * mm});
            skLineSegment(sketch, "E2388", {"start": v(6.4, 26.79) * mm, "end": v(6.27, 26.62) * mm});
            skLineSegment(sketch, "E2389", {"start": v(6.27, 26.62) * mm, "end": v(6.14, 26.45) * mm});
            skLineSegment(sketch, "E2390", {"start": v(6.14, 26.45) * mm, "end": v(6, 26.28) * mm});
            skLineSegment(sketch, "E2391", {"start": v(6, 26.28) * mm, "end": v(5.87, 26.12) * mm});
            skLineSegment(sketch, "E2392", {"start": v(5.87, 26.12) * mm, "end": v(5.74, 25.97) * mm});
            skLineSegment(sketch, "E2393", {"start": v(5.74, 25.97) * mm, "end": v(5.61, 25.84) * mm});
            skLineSegment(sketch, "E2394", {"start": v(5.61, 25.84) * mm, "end": v(5.49, 25.7) * mm});
            skLineSegment(sketch, "E2395", {"start": v(5.49, 25.7) * mm, "end": v(5.36, 25.57) * mm});
            skLineSegment(sketch, "E2396", {"start": v(5.36, 25.57) * mm, "end": v(5.22, 25.44) * mm});
            skLineSegment(sketch, "E2397", {"start": v(5.22, 25.44) * mm, "end": v(5.09, 25.32) * mm});
            skLineSegment(sketch, "E2398", {"start": v(5.09, 25.32) * mm, "end": v(4.95, 25.2) * mm});
            skLineSegment(sketch, "E2399", {"start": v(4.95, 25.2) * mm, "end": v(4.81, 25.08) * mm});
            skLineSegment(sketch, "E2400", {"start": v(4.81, 25.08) * mm, "end": v(4.67, 24.97) * mm});
            skLineSegment(sketch, "E2401", {"start": v(4.67, 24.97) * mm, "end": v(4.53, 24.86) * mm});
            skLineSegment(sketch, "E2402", {"start": v(4.53, 24.86) * mm, "end": v(4.39, 24.76) * mm});
            skLineSegment(sketch, "E2403", {"start": v(4.39, 24.76) * mm, "end": v(4.24, 24.66) * mm});
            skLineSegment(sketch, "E2404", {"start": v(4.24, 24.66) * mm, "end": v(4.1, 24.56) * mm});
            skLineSegment(sketch, "E2405", {"start": v(4.1, 24.56) * mm, "end": v(3.94, 24.47) * mm});
            skLineSegment(sketch, "E2406", {"start": v(3.94, 24.47) * mm, "end": v(3.8, 24.38) * mm});
            skLineSegment(sketch, "E2407", {"start": v(3.8, 24.38) * mm, "end": v(3.64, 24.3) * mm});
            skLineSegment(sketch, "E2408", {"start": v(3.64, 24.3) * mm, "end": v(3.48, 24.21) * mm});
            skLineSegment(sketch, "E2409", {"start": v(3.48, 24.21) * mm, "end": v(3.32, 24.13) * mm});
            skLineSegment(sketch, "E2410", {"start": v(3.32, 24.13) * mm, "end": v(3.16, 24.06) * mm});
            skLineSegment(sketch, "E2411", {"start": v(3.16, 24.06) * mm, "end": v(3, 24) * mm});
            skLineSegment(sketch, "E2412", {"start": v(3, 24) * mm, "end": v(2.83, 23.93) * mm});
            skLineSegment(sketch, "E2413", {"start": v(2.83, 23.93) * mm, "end": v(2.67, 23.87) * mm});
            skLineSegment(sketch, "E2414", {"start": v(2.67, 23.87) * mm, "end": v(2.5, 23.8) * mm});
            skLineSegment(sketch, "E2415", {"start": v(2.5, 23.8) * mm, "end": v(2.33, 23.76) * mm});
            skLineSegment(sketch, "E2416", {"start": v(2.33, 23.76) * mm, "end": v(2.15, 23.7) * mm});
            skLineSegment(sketch, "E2417", {"start": v(2.15, 23.7) * mm, "end": v(1.98, 23.66) * mm});
            skLineSegment(sketch, "E2418", {"start": v(1.98, 23.66) * mm, "end": v(1.8, 23.62) * mm});
            skLineSegment(sketch, "E2419", {"start": v(1.8, 23.62) * mm, "end": v(1.62, 23.59) * mm});
            skLineSegment(sketch, "E2420", {"start": v(1.62, 23.59) * mm, "end": v(1.44, 23.55) * mm});
            skLineSegment(sketch, "E2421", {"start": v(1.44, 23.55) * mm, "end": v(1.25, 23.53) * mm});
            skLineSegment(sketch, "E2422", {"start": v(1.25, 23.53) * mm, "end": v(1.07, 23.5) * mm});
            skLineSegment(sketch, "E2423", {"start": v(1.07, 23.5) * mm, "end": v(0.88, 23.48) * mm});
            skLineSegment(sketch, "E2424", {"start": v(0.88, 23.48) * mm, "end": v(0.85, 23.48) * mm});
            skLineSegment(sketch, "E2425", {"start": v(0.85, 23.48) * mm, "end": v(0.81, 23.48) * mm});
            skLineSegment(sketch, "E2426", {"start": v(0.81, 23.48) * mm, "end": v(0.78, 23.47) * mm});
            skLineSegment(sketch, "E2427", {"start": v(0.78, 23.47) * mm, "end": v(0.75, 23.47) * mm});
            skLineSegment(sketch, "E2428", {"start": v(0.75, 23.47) * mm, "end": v(0.72, 23.46) * mm});
            skLineSegment(sketch, "E2429", {"start": v(0.72, 23.46) * mm, "end": v(0.69, 23.46) * mm});
            skLineSegment(sketch, "E2430", {"start": v(0.69, 23.46) * mm, "end": v(0.66, 23.46) * mm});
            skLineSegment(sketch, "E2431", {"start": v(0.66, 23.46) * mm, "end": v(0.62, 23.45) * mm});
            skLineSegment(sketch, "E2432", {"start": v(0.62, 23.45) * mm, "end": v(0.6, 23.45) * mm});
            skLineSegment(sketch, "E2433", {"start": v(0.6, 23.45) * mm, "end": v(0.56, 23.44) * mm});
            skLineSegment(sketch, "E2434", {"start": v(0.56, 23.44) * mm, "end": v(0.53, 23.44) * mm});
            skLineSegment(sketch, "E2435", {"start": v(0.53, 23.44) * mm, "end": v(0.5, 23.43) * mm});
            skLineSegment(sketch, "E2436", {"start": v(0.5, 23.43) * mm, "end": v(0.46, 23.43) * mm});
            skLineSegment(sketch, "E2437", {"start": v(0.46, 23.43) * mm, "end": v(0.43, 23.42) * mm});
            skLineSegment(sketch, "E2438", {"start": v(0.43, 23.42) * mm, "end": v(0.4, 23.42) * mm});
            skLineSegment(sketch, "E2439", {"start": v(0.4, 23.42) * mm, "end": v(0.36, 23.41) * mm});
            skLineSegment(sketch, "E2440", {"start": v(0.36, 23.41) * mm, "end": v(0.33, 23.4) * mm});
            skLineSegment(sketch, "E2441", {"start": v(0.33, 23.4) * mm, "end": v(0.3, 23.4) * mm});
            skLineSegment(sketch, "E2442", {"start": v(0.3, 23.4) * mm, "end": v(0.26, 23.4) * mm});
            skLineSegment(sketch, "E2443", {"start": v(0.26, 23.4) * mm, "end": v(0.22, 23.39) * mm});
            skLineSegment(sketch, "E2444", {"start": v(0.22, 23.39) * mm, "end": v(0.19, 23.38) * mm});
            skLineSegment(sketch, "E2445", {"start": v(0.19, 23.38) * mm, "end": v(0.15, 23.38) * mm});
            skLineSegment(sketch, "E2446", {"start": v(0.15, 23.38) * mm, "end": v(0.12, 23.37) * mm});
            skLineSegment(sketch, "E2447", {"start": v(0.12, 23.37) * mm, "end": v(0.08, 23.36) * mm});
            skLineSegment(sketch, "E2448", {"start": v(0.08, 23.36) * mm, "end": v(0.04, 23.36) * mm});
            skLineSegment(sketch, "E2449", {"start": v(0.04, 23.36) * mm, "end": v(0, 23.35) * mm});
            skLineSegment(sketch, "E2450", {"start": v(0, 23.35) * mm, "end": v(-0.03, 23.34) * mm});
            skLineSegment(sketch, "E2451", {"start": v(-0.03, 23.34) * mm, "end": v(-0.07, 23.34) * mm});
            skLineSegment(sketch, "E2452", {"start": v(-0.07, 23.34) * mm, "end": v(-0.11, 23.33) * mm});
            skLineSegment(sketch, "E2453", {"start": v(-0.11, 23.33) * mm, "end": v(-0.15, 23.33) * mm});
            skLineSegment(sketch, "E2454", {"start": v(-0.15, 23.33) * mm, "end": v(-0.2, 23.32) * mm});
            skLineSegment(sketch, "E2455", {"start": v(-0.2, 23.32) * mm, "end": v(-0.24, 23.31) * mm});
            skLineSegment(sketch, "E2456", {"start": v(-4.45, 25.1) * mm, "end": v(-4.7, 25.31) * mm});
            skLineSegment(sketch, "E2457", {"start": v(-4.7, 25.31) * mm, "end": v(-4.93, 25.53) * mm});
            skLineSegment(sketch, "E2458", {"start": v(-4.93, 25.53) * mm, "end": v(-5.15, 25.75) * mm});
            skLineSegment(sketch, "E2459", {"start": v(-5.15, 25.75) * mm, "end": v(-5.36, 25.98) * mm});
            skLineSegment(sketch, "E2460", {"start": v(-5.36, 25.98) * mm, "end": v(-5.57, 26.22) * mm});
            skLineSegment(sketch, "E2461", {"start": v(-5.57, 26.22) * mm, "end": v(-5.76, 26.46) * mm});
            skLineSegment(sketch, "E2462", {"start": v(-5.76, 26.46) * mm, "end": v(-5.94, 26.7) * mm});
            skLineSegment(sketch, "E2463", {"start": v(-5.94, 26.7) * mm, "end": v(-6.11, 26.96) * mm});
            skLineSegment(sketch, "E2464", {"start": v(-6.11, 26.96) * mm, "end": v(-6.27, 27.22) * mm});
            skLineSegment(sketch, "E2465", {"start": v(-6.27, 27.22) * mm, "end": v(-6.42, 27.49) * mm});
            skLineSegment(sketch, "E2466", {"start": v(-6.42, 27.49) * mm, "end": v(-6.56, 27.76) * mm});
            skLineSegment(sketch, "E2467", {"start": v(-6.56, 27.76) * mm, "end": v(-6.69, 28.03) * mm});
            skLineSegment(sketch, "E2468", {"start": v(-6.69, 28.03) * mm, "end": v(-6.8, 28.31) * mm});
            skLineSegment(sketch, "E2469", {"start": v(-6.8, 28.31) * mm, "end": v(-6.9, 28.6) * mm});
            skLineSegment(sketch, "E2470", {"start": v(-6.9, 28.6) * mm, "end": v(-7, 28.88) * mm});
            skLineSegment(sketch, "E2471", {"start": v(-7, 28.88) * mm, "end": v(-7.08, 29.17) * mm});
            skLineSegment(sketch, "E2472", {"start": v(-7.08, 29.17) * mm, "end": v(-7.15, 29.47) * mm});
            skLineSegment(sketch, "E2473", {"start": v(-7.15, 29.47) * mm, "end": v(-7.21, 29.76) * mm});
            skLineSegment(sketch, "E2474", {"start": v(-7.21, 29.76) * mm, "end": v(-7.26, 30.06) * mm});
            skLineSegment(sketch, "E2475", {"start": v(-7.26, 30.06) * mm, "end": v(-7.3, 30.36) * mm});
            skLineSegment(sketch, "E2476", {"start": v(-7.3, 30.36) * mm, "end": v(-7.32, 30.67) * mm});
            skLineSegment(sketch, "E2477", {"start": v(-7.32, 30.67) * mm, "end": v(-7.33, 30.97) * mm});
            skLineSegment(sketch, "E2478", {"start": v(-7.33, 30.97) * mm, "end": v(-7.33, 31.27) * mm});
            skLineSegment(sketch, "E2479", {"start": v(-7.33, 31.27) * mm, "end": v(-7.32, 31.58) * mm});
            skLineSegment(sketch, "E2480", {"start": v(-7.32, 31.58) * mm, "end": v(-7.3, 31.89) * mm});
            skLineSegment(sketch, "E2481", {"start": v(-7.3, 31.89) * mm, "end": v(-7.26, 32.2) * mm});
            skLineSegment(sketch, "E2482", {"start": v(-7.26, 32.2) * mm, "end": v(-7.2, 32.5) * mm});
            skLineSegment(sketch, "E2483", {"start": v(-7.2, 32.5) * mm, "end": v(-7.15, 32.8) * mm});
            skLineSegment(sketch, "E2484", {"start": v(-7.15, 32.8) * mm, "end": v(-7.07, 33.11) * mm});
            skLineSegment(sketch, "E2485", {"start": v(-7.07, 33.11) * mm, "end": v(-6.99, 33.42) * mm});
            skLineSegment(sketch, "E2486", {"start": v(-6.99, 33.42) * mm, "end": v(-6.89, 33.72) * mm});
            skLineSegment(sketch, "E2487", {"start": v(-6.89, 33.72) * mm, "end": v(-6.78, 34.02) * mm});
            skLineSegment(sketch, "E2488", {"start": v(-6.78, 34.02) * mm, "end": v(-6.65, 34.31) * mm});
            skLineSegment(sketch, "E2489", {"start": v(-6.65, 34.31) * mm, "end": v(-6.52, 34.6) * mm});
            skLineSegment(sketch, "E2490", {"start": v(-6.52, 34.6) * mm, "end": v(-6.38, 34.87) * mm});
            skLineSegment(sketch, "E2491", {"start": v(-6.38, 34.87) * mm, "end": v(-6.24, 35.14) * mm});
            skLineSegment(sketch, "E2492", {"start": v(-6.24, 35.14) * mm, "end": v(-6.08, 35.4) * mm});
            skLineSegment(sketch, "E2493", {"start": v(-6.08, 35.4) * mm, "end": v(-5.91, 35.65) * mm});
            skLineSegment(sketch, "E2494", {"start": v(-5.91, 35.65) * mm, "end": v(-5.74, 35.9) * mm});
            skLineSegment(sketch, "E2495", {"start": v(-5.74, 35.9) * mm, "end": v(-5.56, 36.12) * mm});
            skLineSegment(sketch, "E2496", {"start": v(-5.56, 36.12) * mm, "end": v(-5.37, 36.35) * mm});
            skLineSegment(sketch, "E2497", {"start": v(-5.37, 36.35) * mm, "end": v(-5.18, 36.56) * mm});
            skLineSegment(sketch, "E2498", {"start": v(-5.18, 36.56) * mm, "end": v(-4.98, 36.76) * mm});
            skLineSegment(sketch, "E2499", {"start": v(-4.98, 36.76) * mm, "end": v(-4.77, 36.96) * mm});
            skLineSegment(sketch, "E2500", {"start": v(-4.77, 36.96) * mm, "end": v(-4.55, 37.14) * mm});
            skLineSegment(sketch, "E2501", {"start": v(-4.55, 37.14) * mm, "end": v(-4.33, 37.32) * mm});
            skLineSegment(sketch, "E2502", {"start": v(-4.33, 37.32) * mm, "end": v(-4.1, 37.48) * mm});
            skLineSegment(sketch, "E2503", {"start": v(-4.1, 37.48) * mm, "end": v(-3.88, 37.64) * mm});
            skLineSegment(sketch, "E2504", {"start": v(-3.88, 37.64) * mm, "end": v(-3.64, 37.78) * mm});
            skLineSegment(sketch, "E2505", {"start": v(-3.64, 37.78) * mm, "end": v(-3.4, 37.92) * mm});
            skLineSegment(sketch, "E2506", {"start": v(-3.4, 37.92) * mm, "end": v(-3.15, 38.04) * mm});
            skLineSegment(sketch, "E2507", {"start": v(-3.15, 38.04) * mm, "end": v(-2.9, 38.16) * mm});
            skLineSegment(sketch, "E2508", {"start": v(-2.9, 38.16) * mm, "end": v(-2.64, 38.26) * mm});
            skLineSegment(sketch, "E2509", {"start": v(-2.64, 38.26) * mm, "end": v(-2.38, 38.35) * mm});
            skLineSegment(sketch, "E2510", {"start": v(-2.38, 38.35) * mm, "end": v(-2.12, 38.43) * mm});
            skLineSegment(sketch, "E2511", {"start": v(-2.12, 38.43) * mm, "end": v(-1.85, 38.5) * mm});
            skLineSegment(sketch, "E2512", {"start": v(-1.85, 38.5) * mm, "end": v(-1.58, 38.56) * mm});
            skLineSegment(sketch, "E2513", {"start": v(-1.58, 38.56) * mm, "end": v(-1.3, 38.6) * mm});
            skLineSegment(sketch, "E2514", {"start": v(-1.3, 38.6) * mm, "end": v(-1.03, 38.64) * mm});
            skLineSegment(sketch, "E2515", {"start": v(-1.03, 38.64) * mm, "end": v(-0.75, 38.67) * mm});
            skLineSegment(sketch, "E2516", {"start": v(-0.75, 38.67) * mm, "end": v(-0.47, 38.68) * mm});
            skLineSegment(sketch, "E2517", {"start": v(-0.47, 38.68) * mm, "end": v(-0.18, 38.68) * mm});
            skLineSegment(sketch, "E2518", {"start": v(-0.18, 38.68) * mm, "end": v(0.1, 38.67) * mm});
            skLineSegment(sketch, "E2519", {"start": v(0.1, 38.67) * mm, "end": v(0.39, 38.64) * mm});
            skLineSegment(sketch, "E2520", {"start": v(0.39, 38.64) * mm, "end": v(0.24, 38.22) * mm});
            skLineSegment(sketch, "E2521", {"start": v(0.24, 38.22) * mm, "end": v(0.09, 37.8) * mm});
            skLineSegment(sketch, "E2522", {"start": v(0.09, 37.8) * mm, "end": v(-0.07, 37.37) * mm});
            skLineSegment(sketch, "E2523", {"start": v(-0.07, 37.37) * mm, "end": v(-0.22, 36.95) * mm});
            skLineSegment(sketch, "E2524", {"start": v(-0.22, 36.95) * mm, "end": v(-0.37, 36.52) * mm});
            skLineSegment(sketch, "E2525", {"start": v(-0.37, 36.52) * mm, "end": v(-0.52, 36.1) * mm});
            skLineSegment(sketch, "E2526", {"start": v(-0.52, 36.1) * mm, "end": v(-0.67, 35.68) * mm});
            skLineSegment(sketch, "E2527", {"start": v(-0.67, 35.68) * mm, "end": v(-0.82, 35.26) * mm});
            skLineSegment(sketch, "E2528", {"start": v(-0.82, 35.26) * mm, "end": v(-0.97, 34.83) * mm});
            skLineSegment(sketch, "E2529", {"start": v(-0.97, 34.83) * mm, "end": v(-1.12, 34.41) * mm});
            skLineSegment(sketch, "E2530", {"start": v(-1.12, 34.41) * mm, "end": v(-1.27, 33.99) * mm});
            skLineSegment(sketch, "E2531", {"start": v(-1.27, 33.99) * mm, "end": v(-1.42, 33.57) * mm});
            skLineSegment(sketch, "E2532", {"start": v(-1.42, 33.57) * mm, "end": v(-1.58, 33.14) * mm});
            skLineSegment(sketch, "E2533", {"start": v(-1.58, 33.14) * mm, "end": v(-1.73, 32.72) * mm});
            skLineSegment(sketch, "E2534", {"start": v(-1.73, 32.72) * mm, "end": v(-1.88, 32.3) * mm});
            skLineSegment(sketch, "E2535", {"start": v(-1.88, 32.3) * mm, "end": v(-2.03, 31.87) * mm});
            skLineSegment(sketch, "E2536", {"start": v(-2.03, 31.87) * mm, "end": v(-2.18, 31.45) * mm});
            skLineSegment(sketch, "E2537", {"start": v(-2.18, 31.45) * mm, "end": v(-2.33, 31.03) * mm});
            skLineSegment(sketch, "E2538", {"start": v(-2.33, 31.03) * mm, "end": v(-2.48, 30.6) * mm});
            skLineSegment(sketch, "E2539", {"start": v(-2.48, 30.6) * mm, "end": v(-2.63, 30.18) * mm});
            skLineSegment(sketch, "E2540", {"start": v(-2.63, 30.18) * mm, "end": v(-2.78, 29.76) * mm});
            skLineSegment(sketch, "E2541", {"start": v(-2.78, 29.76) * mm, "end": v(-2.94, 29.34) * mm});
            skLineSegment(sketch, "E2542", {"start": v(-2.94, 29.34) * mm, "end": v(-3.09, 28.92) * mm});
            skLineSegment(sketch, "E2543", {"start": v(-3.09, 28.92) * mm, "end": v(-3.24, 28.5) * mm});
            skLineSegment(sketch, "E2544", {"start": v(-3.24, 28.5) * mm, "end": v(-3.39, 28.07) * mm});
            skLineSegment(sketch, "E2545", {"start": v(-3.39, 28.07) * mm, "end": v(-3.54, 27.65) * mm});
            skLineSegment(sketch, "E2546", {"start": v(-3.54, 27.65) * mm, "end": v(-3.7, 27.22) * mm});
            skLineSegment(sketch, "E2547", {"start": v(-3.7, 27.22) * mm, "end": v(-3.84, 26.8) * mm});
            skLineSegment(sketch, "E2548", {"start": v(-3.84, 26.8) * mm, "end": v(-4, 26.38) * mm});
            skLineSegment(sketch, "E2549", {"start": v(-4, 26.38) * mm, "end": v(-4.14, 25.95) * mm});
            skLineSegment(sketch, "E2550", {"start": v(-4.14, 25.95) * mm, "end": v(-4.3, 25.53) * mm});
            skLineSegment(sketch, "E2551", {"start": v(-4.3, 25.53) * mm, "end": v(-4.45, 25.1) * mm});
            skLineSegment(sketch, "E2552", {"start": v(-5.66, 22.05) * mm, "end": v(-5.7, 21.96) * mm});
            skLineSegment(sketch, "E2553", {"start": v(-5.7, 21.96) * mm, "end": v(-5.72, 21.87) * mm});
            skLineSegment(sketch, "E2554", {"start": v(-5.72, 21.87) * mm, "end": v(-5.75, 21.78) * mm});
            skLineSegment(sketch, "E2555", {"start": v(-5.75, 21.78) * mm, "end": v(-5.78, 21.69) * mm});
            skLineSegment(sketch, "E2556", {"start": v(-5.78, 21.69) * mm, "end": v(-5.81, 21.6) * mm});
            skLineSegment(sketch, "E2557", {"start": v(-5.81, 21.6) * mm, "end": v(-5.84, 21.5) * mm});
            skLineSegment(sketch, "E2558", {"start": v(-5.84, 21.5) * mm, "end": v(-5.87, 21.42) * mm});
            skLineSegment(sketch, "E2559", {"start": v(-5.87, 21.42) * mm, "end": v(-5.9, 21.33) * mm});
            skLineSegment(sketch, "E2560", {"start": v(-5.9, 21.33) * mm, "end": v(-5.93, 21.24) * mm});
            skLineSegment(sketch, "E2561", {"start": v(-5.93, 21.24) * mm, "end": v(-5.96, 21.15) * mm});
            skLineSegment(sketch, "E2562", {"start": v(-5.96, 21.15) * mm, "end": v(-5.98, 21.07) * mm});
            skLineSegment(sketch, "E2563", {"start": v(-5.98, 21.07) * mm, "end": v(-6.01, 20.98) * mm});
            skLineSegment(sketch, "E2564", {"start": v(-6.01, 20.98) * mm, "end": v(-6.04, 20.9) * mm});
            skLineSegment(sketch, "E2565", {"start": v(-6.04, 20.9) * mm, "end": v(-6.07, 20.8) * mm});
            skLineSegment(sketch, "E2566", {"start": v(-6.07, 20.8) * mm, "end": v(-6.1, 20.72) * mm});
            skLineSegment(sketch, "E2567", {"start": v(-6.1, 20.72) * mm, "end": v(-6.12, 20.64) * mm});
            skLineSegment(sketch, "E2568", {"start": v(-6.12, 20.64) * mm, "end": v(-6.15, 20.55) * mm});
            skLineSegment(sketch, "E2569", {"start": v(-6.15, 20.55) * mm, "end": v(-6.18, 20.47) * mm});
            skLineSegment(sketch, "E2570", {"start": v(-6.18, 20.47) * mm, "end": v(-6.2, 20.38) * mm});
            skLineSegment(sketch, "E2571", {"start": v(-6.2, 20.38) * mm, "end": v(-6.23, 20.3) * mm});
            skLineSegment(sketch, "E2572", {"start": v(-6.23, 20.3) * mm, "end": v(-6.26, 20.21) * mm});
            skLineSegment(sketch, "E2573", {"start": v(-6.26, 20.21) * mm, "end": v(-6.29, 20.13) * mm});
            skLineSegment(sketch, "E2574", {"start": v(-6.29, 20.13) * mm, "end": v(-6.32, 20.05) * mm});
            skLineSegment(sketch, "E2575", {"start": v(-6.32, 20.05) * mm, "end": v(-6.34, 19.96) * mm});
            skLineSegment(sketch, "E2576", {"start": v(-6.34, 19.96) * mm, "end": v(-6.37, 19.88) * mm});
            skLineSegment(sketch, "E2577", {"start": v(-6.37, 19.88) * mm, "end": v(-6.4, 19.8) * mm});
            skLineSegment(sketch, "E2578", {"start": v(-6.4, 19.8) * mm, "end": v(-6.43, 19.71) * mm});
            skLineSegment(sketch, "E2579", {"start": v(-6.43, 19.71) * mm, "end": v(-6.46, 19.63) * mm});
            skLineSegment(sketch, "E2580", {"start": v(-6.46, 19.63) * mm, "end": v(-6.49, 19.55) * mm});
            skLineSegment(sketch, "E2581", {"start": v(-6.49, 19.55) * mm, "end": v(-6.51, 19.46) * mm});
            skLineSegment(sketch, "E2582", {"start": v(-6.51, 19.46) * mm, "end": v(-6.54, 19.38) * mm});
            skLineSegment(sketch, "E2583", {"start": v(-6.54, 19.38) * mm, "end": v(-6.57, 19.3) * mm});
            skLineSegment(sketch, "E2584", {"start": v(-6.57, 19.3) * mm, "end": v(-6.59, 19.25) * mm});
            skLineSegment(sketch, "E2585", {"start": v(-6.59, 19.25) * mm, "end": v(-6.6, 19.2) * mm});
            skLineSegment(sketch, "E2586", {"start": v(-6.6, 19.2) * mm, "end": v(-6.62, 19.16) * mm});
            skLineSegment(sketch, "E2587", {"start": v(-6.62, 19.16) * mm, "end": v(-6.64, 19.12) * mm});
            skLineSegment(sketch, "E2588", {"start": v(-6.64, 19.12) * mm, "end": v(-6.66, 19.07) * mm});
            skLineSegment(sketch, "E2589", {"start": v(-6.66, 19.07) * mm, "end": v(-6.67, 19.02) * mm});
            skLineSegment(sketch, "E2590", {"start": v(-6.67, 19.02) * mm, "end": v(-6.7, 18.98) * mm});
            skLineSegment(sketch, "E2591", {"start": v(-6.7, 18.98) * mm, "end": v(-6.7, 18.93) * mm});
            skLineSegment(sketch, "E2592", {"start": v(-6.7, 18.93) * mm, "end": v(-6.73, 18.89) * mm});
            skLineSegment(sketch, "E2593", {"start": v(-6.73, 18.89) * mm, "end": v(-6.74, 18.84) * mm});
            skLineSegment(sketch, "E2594", {"start": v(-6.74, 18.84) * mm, "end": v(-6.76, 18.8) * mm});
            skLineSegment(sketch, "E2595", {"start": v(-6.76, 18.8) * mm, "end": v(-6.78, 18.75) * mm});
            skLineSegment(sketch, "E2596", {"start": v(-6.78, 18.75) * mm, "end": v(-6.8, 18.7) * mm});
            skLineSegment(sketch, "E2597", {"start": v(-6.8, 18.7) * mm, "end": v(-6.82, 18.66) * mm});
            skLineSegment(sketch, "E2598", {"start": v(-6.82, 18.66) * mm, "end": v(-6.84, 18.62) * mm});
            skLineSegment(sketch, "E2599", {"start": v(-6.84, 18.62) * mm, "end": v(-6.86, 18.57) * mm});
            skLineSegment(sketch, "E2600", {"start": v(-6.86, 18.57) * mm, "end": v(-6.88, 18.53) * mm});
            skLineSegment(sketch, "E2601", {"start": v(-6.88, 18.53) * mm, "end": v(-6.9, 18.48) * mm});
            skLineSegment(sketch, "E2602", {"start": v(-6.9, 18.48) * mm, "end": v(-6.92, 18.44) * mm});
            skLineSegment(sketch, "E2603", {"start": v(-6.92, 18.44) * mm, "end": v(-6.94, 18.4) * mm});
            skLineSegment(sketch, "E2604", {"start": v(-6.94, 18.4) * mm, "end": v(-6.96, 18.35) * mm});
            skLineSegment(sketch, "E2605", {"start": v(-6.96, 18.35) * mm, "end": v(-6.98, 18.3) * mm});
            skLineSegment(sketch, "E2606", {"start": v(-6.98, 18.3) * mm, "end": v(-7, 18.26) * mm});
            skLineSegment(sketch, "E2607", {"start": v(-7, 18.26) * mm, "end": v(-7.02, 18.22) * mm});
            skLineSegment(sketch, "E2608", {"start": v(-7.02, 18.22) * mm, "end": v(-7.04, 18.17) * mm});
            skLineSegment(sketch, "E2609", {"start": v(-7.04, 18.17) * mm, "end": v(-7.06, 18.13) * mm});
            skLineSegment(sketch, "E2610", {"start": v(-7.06, 18.13) * mm, "end": v(-7.08, 18.08) * mm});
            skLineSegment(sketch, "E2611", {"start": v(-7.08, 18.08) * mm, "end": v(-7.1, 18.04) * mm});
            skLineSegment(sketch, "E2612", {"start": v(-7.1, 18.04) * mm, "end": v(-7.12, 18) * mm});
            skLineSegment(sketch, "E2613", {"start": v(-7.12, 18) * mm, "end": v(-7.15, 17.95) * mm});
            skLineSegment(sketch, "E2614", {"start": v(-7.15, 17.95) * mm, "end": v(-7.17, 17.9) * mm});
            skLineSegment(sketch, "E2615", {"start": v(-7.17, 17.9) * mm, "end": v(-7.19, 17.87) * mm});
            skLineSegment(sketch, "E2616", {"start": v(-7.19, 17.87) * mm, "end": v(-7.23, 17.79) * mm});
            skLineSegment(sketch, "E2617", {"start": v(-7.23, 17.79) * mm, "end": v(-7.27, 17.71) * mm});
            skLineSegment(sketch, "E2618", {"start": v(-7.27, 17.71) * mm, "end": v(-7.32, 17.64) * mm});
            skLineSegment(sketch, "E2619", {"start": v(-7.32, 17.64) * mm, "end": v(-7.36, 17.58) * mm});
            skLineSegment(sketch, "E2620", {"start": v(-7.36, 17.58) * mm, "end": v(-7.4, 17.51) * mm});
            skLineSegment(sketch, "E2621", {"start": v(-7.4, 17.51) * mm, "end": v(-7.45, 17.46) * mm});
            skLineSegment(sketch, "E2622", {"start": v(-7.45, 17.46) * mm, "end": v(-7.5, 17.4) * mm});
            skLineSegment(sketch, "E2623", {"start": v(-7.5, 17.4) * mm, "end": v(-7.54, 17.35) * mm});
            skLineSegment(sketch, "E2624", {"start": v(-7.54, 17.35) * mm, "end": v(-7.58, 17.3) * mm});
            skLineSegment(sketch, "E2625", {"start": v(-7.58, 17.3) * mm, "end": v(-7.63, 17.26) * mm});
            skLineSegment(sketch, "E2626", {"start": v(-7.63, 17.26) * mm, "end": v(-7.68, 17.22) * mm});
            skLineSegment(sketch, "E2627", {"start": v(-7.68, 17.22) * mm, "end": v(-7.73, 17.18) * mm});
            skLineSegment(sketch, "E2628", {"start": v(-7.73, 17.18) * mm, "end": v(-7.78, 17.15) * mm});
            skLineSegment(sketch, "E2629", {"start": v(-7.78, 17.15) * mm, "end": v(-7.84, 17.12) * mm});
            skLineSegment(sketch, "E2630", {"start": v(-7.84, 17.12) * mm, "end": v(-7.9, 17.1) * mm});
            skLineSegment(sketch, "E2631", {"start": v(-7.9, 17.1) * mm, "end": v(-7.95, 17.08) * mm});
            skLineSegment(sketch, "E2632", {"start": v(-7.95, 17.08) * mm, "end": v(-8, 17.06) * mm});
            skLineSegment(sketch, "E2633", {"start": v(-8, 17.06) * mm, "end": v(-8.06, 17.05) * mm});
            skLineSegment(sketch, "E2634", {"start": v(-8.06, 17.05) * mm, "end": v(-8.12, 17.04) * mm});
            skLineSegment(sketch, "E2635", {"start": v(-8.12, 17.04) * mm, "end": v(-8.19, 17.03) * mm});
            skLineSegment(sketch, "E2636", {"start": v(-8.19, 17.03) * mm, "end": v(-8.25, 17.03) * mm});
            skLineSegment(sketch, "E2637", {"start": v(-8.25, 17.03) * mm, "end": v(-8.32, 17.03) * mm});
            skLineSegment(sketch, "E2638", {"start": v(-8.32, 17.03) * mm, "end": v(-8.38, 17.04) * mm});
            skLineSegment(sketch, "E2639", {"start": v(-8.38, 17.04) * mm, "end": v(-8.45, 17.04) * mm});
            skLineSegment(sketch, "E2640", {"start": v(-8.45, 17.04) * mm, "end": v(-8.53, 17.06) * mm});
            skLineSegment(sketch, "E2641", {"start": v(-8.53, 17.06) * mm, "end": v(-8.6, 17.07) * mm});
            skLineSegment(sketch, "E2642", {"start": v(-8.6, 17.07) * mm, "end": v(-8.68, 17.1) * mm});
            skLineSegment(sketch, "E2643", {"start": v(-8.68, 17.1) * mm, "end": v(-8.76, 17.11) * mm});
            skLineSegment(sketch, "E2644", {"start": v(-8.76, 17.11) * mm, "end": v(-8.84, 17.14) * mm});
            skLineSegment(sketch, "E2645", {"start": v(-8.84, 17.14) * mm, "end": v(-8.93, 17.17) * mm});
            skLineSegment(sketch, "E2646", {"start": v(-8.93, 17.17) * mm, "end": v(-9.02, 17.2) * mm});
            skLineSegment(sketch, "E2647", {"start": v(-9.02, 17.2) * mm, "end": v(-9.1, 17.24) * mm});
            skLineSegment(sketch, "E2648", {"start": v(-9.1, 17.24) * mm, "end": v(-9.28, 17.32) * mm});
            skLineSegment(sketch, "E2649", {"start": v(-9.28, 17.32) * mm, "end": v(-9.46, 17.4) * mm});
            skLineSegment(sketch, "E2650", {"start": v(-9.46, 17.4) * mm, "end": v(-9.63, 17.48) * mm});
            skLineSegment(sketch, "E2651", {"start": v(-9.63, 17.48) * mm, "end": v(-9.8, 17.57) * mm});
            skLineSegment(sketch, "E2652", {"start": v(-9.8, 17.57) * mm, "end": v(-9.96, 17.67) * mm});
            skLineSegment(sketch, "E2653", {"start": v(-9.96, 17.67) * mm, "end": v(-10.12, 17.76) * mm});
            skLineSegment(sketch, "E2654", {"start": v(-10.12, 17.76) * mm, "end": v(-10.27, 17.86) * mm});
            skLineSegment(sketch, "E2655", {"start": v(-10.27, 17.86) * mm, "end": v(-10.43, 17.97) * mm});
            skLineSegment(sketch, "E2656", {"start": v(-10.43, 17.97) * mm, "end": v(-10.58, 18.08) * mm});
            skLineSegment(sketch, "E2657", {"start": v(-10.58, 18.08) * mm, "end": v(-10.73, 18.19) * mm});
            skLineSegment(sketch, "E2658", {"start": v(-10.73, 18.19) * mm, "end": v(-10.87, 18.3) * mm});
            skLineSegment(sketch, "E2659", {"start": v(-10.87, 18.3) * mm, "end": v(-11.01, 18.42) * mm});
            skLineSegment(sketch, "E2660", {"start": v(-11.01, 18.42) * mm, "end": v(-11.15, 18.54) * mm});
            skLineSegment(sketch, "E2661", {"start": v(-11.15, 18.54) * mm, "end": v(-11.3, 18.66) * mm});
            skLineSegment(sketch, "E2662", {"start": v(-11.3, 18.66) * mm, "end": v(-11.43, 18.79) * mm});
            skLineSegment(sketch, "E2663", {"start": v(-11.43, 18.79) * mm, "end": v(-11.56, 18.92) * mm});
            skLineSegment(sketch, "E2664", {"start": v(-11.56, 18.92) * mm, "end": v(-11.69, 19.05) * mm});
            skLineSegment(sketch, "E2665", {"start": v(-11.69, 19.05) * mm, "end": v(-11.82, 19.18) * mm});
            skLineSegment(sketch, "E2666", {"start": v(-11.82, 19.18) * mm, "end": v(-11.94, 19.32) * mm});
            skLineSegment(sketch, "E2667", {"start": v(-11.94, 19.32) * mm, "end": v(-12.07, 19.45) * mm});
            skLineSegment(sketch, "E2668", {"start": v(-12.07, 19.45) * mm, "end": v(-12.19, 19.6) * mm});
            skLineSegment(sketch, "E2669", {"start": v(-12.19, 19.6) * mm, "end": v(-12.3, 19.74) * mm});
            skLineSegment(sketch, "E2670", {"start": v(-12.3, 19.74) * mm, "end": v(-12.43, 19.88) * mm});
            skLineSegment(sketch, "E2671", {"start": v(-12.43, 19.88) * mm, "end": v(-12.54, 20.03) * mm});
            skLineSegment(sketch, "E2672", {"start": v(-12.54, 20.03) * mm, "end": v(-12.66, 20.17) * mm});
            skLineSegment(sketch, "E2673", {"start": v(-12.66, 20.17) * mm, "end": v(-12.77, 20.32) * mm});
            skLineSegment(sketch, "E2674", {"start": v(-12.77, 20.32) * mm, "end": v(-12.89, 20.47) * mm});
            skLineSegment(sketch, "E2675", {"start": v(-12.89, 20.47) * mm, "end": v(-13, 20.62) * mm});
            skLineSegment(sketch, "E2676", {"start": v(-13, 20.62) * mm, "end": v(-13.1, 20.77) * mm});
            skLineSegment(sketch, "E2677", {"start": v(-13.1, 20.77) * mm, "end": v(-13.22, 20.92) * mm});
            skLineSegment(sketch, "E2678", {"start": v(-13.22, 20.92) * mm, "end": v(-13.32, 21.08) * mm});
            skLineSegment(sketch, "E2679", {"start": v(-13.32, 21.08) * mm, "end": v(-13.43, 21.23) * mm});
            skLineSegment(sketch, "E2680", {"start": v(-13.43, 21.23) * mm, "end": v(-13.54, 21.4) * mm});
            skLineSegment(sketch, "E2681", {"start": v(-13.54, 21.4) * mm, "end": v(-13.65, 21.55) * mm});
            skLineSegment(sketch, "E2682", {"start": v(-13.65, 21.55) * mm, "end": v(-13.75, 21.71) * mm});
            skLineSegment(sketch, "E2683", {"start": v(-13.75, 21.71) * mm, "end": v(-13.86, 21.87) * mm});
            skLineSegment(sketch, "E2684", {"start": v(-13.86, 21.87) * mm, "end": v(-13.96, 22.03) * mm});
            skLineSegment(sketch, "E2685", {"start": v(-13.96, 22.03) * mm, "end": v(-14.06, 22.2) * mm});
            skLineSegment(sketch, "E2686", {"start": v(-14.06, 22.2) * mm, "end": v(-14.16, 22.36) * mm});
            skLineSegment(sketch, "E2687", {"start": v(-14.16, 22.36) * mm, "end": v(-14.26, 22.52) * mm});
            skLineSegment(sketch, "E2688", {"start": v(-14.26, 22.52) * mm, "end": v(-14.36, 22.69) * mm});
            skLineSegment(sketch, "E2689", {"start": v(-14.36, 22.69) * mm, "end": v(-14.45, 22.85) * mm});
            skLineSegment(sketch, "E2690", {"start": v(-14.45, 22.85) * mm, "end": v(-14.55, 23.02) * mm});
            skLineSegment(sketch, "E2691", {"start": v(-14.55, 23.02) * mm, "end": v(-14.64, 23.19) * mm});
            skLineSegment(sketch, "E2692", {"start": v(-14.64, 23.19) * mm, "end": v(-14.73, 23.36) * mm});
            skLineSegment(sketch, "E2693", {"start": v(-14.73, 23.36) * mm, "end": v(-14.81, 23.53) * mm});
            skLineSegment(sketch, "E2694", {"start": v(-14.81, 23.53) * mm, "end": v(-14.9, 23.7) * mm});
            skLineSegment(sketch, "E2695", {"start": v(-14.9, 23.7) * mm, "end": v(-14.98, 23.87) * mm});
            skLineSegment(sketch, "E2696", {"start": v(-14.98, 23.87) * mm, "end": v(-15.07, 24.04) * mm});
            skLineSegment(sketch, "E2697", {"start": v(-15.07, 24.04) * mm, "end": v(-15.15, 24.21) * mm});
            skLineSegment(sketch, "E2698", {"start": v(-15.15, 24.21) * mm, "end": v(-15.23, 24.39) * mm});
            skLineSegment(sketch, "E2699", {"start": v(-15.23, 24.39) * mm, "end": v(-15.3, 24.56) * mm});
            skLineSegment(sketch, "E2700", {"start": v(-15.3, 24.56) * mm, "end": v(-15.38, 24.74) * mm});
            skLineSegment(sketch, "E2701", {"start": v(-15.38, 24.74) * mm, "end": v(-15.45, 24.91) * mm});
            skLineSegment(sketch, "E2702", {"start": v(-15.45, 24.91) * mm, "end": v(-15.52, 25.1) * mm});
            skLineSegment(sketch, "E2703", {"start": v(-15.52, 25.1) * mm, "end": v(-15.59, 25.27) * mm});
            skLineSegment(sketch, "E2704", {"start": v(-15.59, 25.27) * mm, "end": v(-15.65, 25.45) * mm});
            skLineSegment(sketch, "E2705", {"start": v(-15.65, 25.45) * mm, "end": v(-15.72, 25.63) * mm});
            skLineSegment(sketch, "E2706", {"start": v(-15.72, 25.63) * mm, "end": v(-15.78, 25.81) * mm});
            skLineSegment(sketch, "E2707", {"start": v(-15.78, 25.81) * mm, "end": v(-15.84, 26) * mm});
            skLineSegment(sketch, "E2708", {"start": v(-15.84, 26) * mm, "end": v(-15.9, 26.18) * mm});
            skLineSegment(sketch, "E2709", {"start": v(-15.9, 26.18) * mm, "end": v(-15.95, 26.37) * mm});
            skLineSegment(sketch, "E2710", {"start": v(-15.95, 26.37) * mm, "end": v(-16, 26.55) * mm});
            skLineSegment(sketch, "E2711", {"start": v(-16, 26.55) * mm, "end": v(-16.05, 26.74) * mm});
            skLineSegment(sketch, "E2712", {"start": v(-16.05, 26.74) * mm, "end": v(-16.07, 26.81) * mm});
            skLineSegment(sketch, "E2713", {"start": v(-16.07, 26.81) * mm, "end": v(-16.08, 26.89) * mm});
            skLineSegment(sketch, "E2714", {"start": v(-16.08, 26.89) * mm, "end": v(-16.1, 26.96) * mm});
            skLineSegment(sketch, "E2715", {"start": v(-16.1, 26.96) * mm, "end": v(-16.12, 27.04) * mm});
            skLineSegment(sketch, "E2716", {"start": v(-16.12, 27.04) * mm, "end": v(-16.14, 27.11) * mm});
            skLineSegment(sketch, "E2717", {"start": v(-16.14, 27.11) * mm, "end": v(-16.16, 27.19) * mm});
            skLineSegment(sketch, "E2718", {"start": v(-16.16, 27.19) * mm, "end": v(-16.17, 27.26) * mm});
            skLineSegment(sketch, "E2719", {"start": v(-16.17, 27.26) * mm, "end": v(-16.19, 27.34) * mm});
            skLineSegment(sketch, "E2720", {"start": v(-16.19, 27.34) * mm, "end": v(-16.2, 27.41) * mm});
            skLineSegment(sketch, "E2721", {"start": v(-16.2, 27.41) * mm, "end": v(-16.22, 27.49) * mm});
            skLineSegment(sketch, "E2722", {"start": v(-16.22, 27.49) * mm, "end": v(-16.24, 27.56) * mm});
            skLineSegment(sketch, "E2723", {"start": v(-16.24, 27.56) * mm, "end": v(-16.25, 27.64) * mm});
            skLineSegment(sketch, "E2724", {"start": v(-16.25, 27.64) * mm, "end": v(-16.27, 27.72) * mm});
            skLineSegment(sketch, "E2725", {"start": v(-16.27, 27.72) * mm, "end": v(-16.28, 27.8) * mm});
            skLineSegment(sketch, "E2726", {"start": v(-16.28, 27.8) * mm, "end": v(-16.3, 27.87) * mm});
            skLineSegment(sketch, "E2727", {"start": v(-16.3, 27.87) * mm, "end": v(-16.31, 27.94) * mm});
            skLineSegment(sketch, "E2728", {"start": v(-16.31, 27.94) * mm, "end": v(-16.33, 28.02) * mm});
            skLineSegment(sketch, "E2729", {"start": v(-16.33, 28.02) * mm, "end": v(-16.34, 28.1) * mm});
            skLineSegment(sketch, "E2730", {"start": v(-16.34, 28.1) * mm, "end": v(-16.36, 28.18) * mm});
            skLineSegment(sketch, "E2731", {"start": v(-16.36, 28.18) * mm, "end": v(-16.37, 28.25) * mm});
            skLineSegment(sketch, "E2732", {"start": v(-16.37, 28.25) * mm, "end": v(-16.38, 28.33) * mm});
            skLineSegment(sketch, "E2733", {"start": v(-16.38, 28.33) * mm, "end": v(-16.4, 28.4) * mm});
            skLineSegment(sketch, "E2734", {"start": v(-16.4, 28.4) * mm, "end": v(-16.4, 28.49) * mm});
            skLineSegment(sketch, "E2735", {"start": v(-16.4, 28.49) * mm, "end": v(-16.42, 28.56) * mm});
            skLineSegment(sketch, "E2736", {"start": v(-16.42, 28.56) * mm, "end": v(-16.43, 28.64) * mm});
            skLineSegment(sketch, "E2737", {"start": v(-16.43, 28.64) * mm, "end": v(-16.45, 28.72) * mm});
            skLineSegment(sketch, "E2738", {"start": v(-16.45, 28.72) * mm, "end": v(-16.46, 28.8) * mm});
            skLineSegment(sketch, "E2739", {"start": v(-16.46, 28.8) * mm, "end": v(-16.47, 28.88) * mm});
            skLineSegment(sketch, "E2740", {"start": v(-16.47, 28.88) * mm, "end": v(-16.48, 28.96) * mm});
            skLineSegment(sketch, "E2741", {"start": v(-16.48, 28.96) * mm, "end": v(-16.5, 29.04) * mm});
            skLineSegment(sketch, "E2742", {"start": v(-16.5, 29.04) * mm, "end": v(-16.5, 29.12) * mm});
            skLineSegment(sketch, "E2743", {"start": v(-16.5, 29.12) * mm, "end": v(-16.51, 29.2) * mm});
            skLineSegment(sketch, "E2744", {"start": v(-16.51, 29.2) * mm, "end": v(-16.28, 28.81) * mm});
            skLineSegment(sketch, "E2745", {"start": v(-16.28, 28.81) * mm, "end": v(-16.05, 28.43) * mm});
            skLineSegment(sketch, "E2746", {"start": v(-16.05, 28.43) * mm, "end": v(-15.8, 28.07) * mm});
            skLineSegment(sketch, "E2747", {"start": v(-15.8, 28.07) * mm, "end": v(-15.54, 27.72) * mm});
            skLineSegment(sketch, "E2748", {"start": v(-15.54, 27.72) * mm, "end": v(-15.27, 27.39) * mm});
            skLineSegment(sketch, "E2749", {"start": v(-15.27, 27.39) * mm, "end": v(-15, 27.07) * mm});
            skLineSegment(sketch, "E2750", {"start": v(-15, 27.07) * mm, "end": v(-14.72, 26.76) * mm});
            skLineSegment(sketch, "E2751", {"start": v(-14.72, 26.76) * mm, "end": v(-14.42, 26.46) * mm});
            skLineSegment(sketch, "E2752", {"start": v(-14.42, 26.46) * mm, "end": v(-14.13, 26.18) * mm});
            skLineSegment(sketch, "E2753", {"start": v(-14.13, 26.18) * mm, "end": v(-13.82, 25.9) * mm});
            skLineSegment(sketch, "E2754", {"start": v(-13.82, 25.9) * mm, "end": v(-13.5, 25.64) * mm});
            skLineSegment(sketch, "E2755", {"start": v(-13.5, 25.64) * mm, "end": v(-13.18, 25.4) * mm});
            skLineSegment(sketch, "E2756", {"start": v(-13.18, 25.4) * mm, "end": v(-12.86, 25.15) * mm});
            skLineSegment(sketch, "E2757", {"start": v(-12.86, 25.15) * mm, "end": v(-12.52, 24.92) * mm});
            skLineSegment(sketch, "E2758", {"start": v(-12.52, 24.92) * mm, "end": v(-12.18, 24.7) * mm});
            skLineSegment(sketch, "E2759", {"start": v(-12.18, 24.7) * mm, "end": v(-11.83, 24.49) * mm});
            skLineSegment(sketch, "E2760", {"start": v(-11.83, 24.49) * mm, "end": v(-11.48, 24.29) * mm});
            skLineSegment(sketch, "E2761", {"start": v(-11.48, 24.29) * mm, "end": v(-11.12, 24.1) * mm});
            skLineSegment(sketch, "E2762", {"start": v(-11.12, 24.1) * mm, "end": v(-10.76, 23.9) * mm});
            skLineSegment(sketch, "E2763", {"start": v(-10.76, 23.9) * mm, "end": v(-10.39, 23.73) * mm});
            skLineSegment(sketch, "E2764", {"start": v(-10.39, 23.73) * mm, "end": v(-10.02, 23.56) * mm});
            skLineSegment(sketch, "E2765", {"start": v(-10.02, 23.56) * mm, "end": v(-9.64, 23.4) * mm});
            skLineSegment(sketch, "E2766", {"start": v(-9.64, 23.4) * mm, "end": v(-9.26, 23.24) * mm});
            skLineSegment(sketch, "E2767", {"start": v(-9.26, 23.24) * mm, "end": v(-8.87, 23.09) * mm});
            skLineSegment(sketch, "E2768", {"start": v(-8.87, 23.09) * mm, "end": v(-8.48, 22.94) * mm});
            skLineSegment(sketch, "E2769", {"start": v(-8.48, 22.94) * mm, "end": v(-8.09, 22.8) * mm});
            skLineSegment(sketch, "E2770", {"start": v(-8.09, 22.8) * mm, "end": v(-7.69, 22.67) * mm});
            skLineSegment(sketch, "E2771", {"start": v(-7.69, 22.67) * mm, "end": v(-7.29, 22.54) * mm});
            skLineSegment(sketch, "E2772", {"start": v(-7.29, 22.54) * mm, "end": v(-6.89, 22.4) * mm});
            skLineSegment(sketch, "E2773", {"start": v(-6.89, 22.4) * mm, "end": v(-6.48, 22.29) * mm});
            skLineSegment(sketch, "E2774", {"start": v(-6.48, 22.29) * mm, "end": v(-6.07, 22.17) * mm});
            skLineSegment(sketch, "E2775", {"start": v(-6.07, 22.17) * mm, "end": v(-5.66, 22.05) * mm});
            skLineSegment(sketch, "E2776", {"start": v(6, 40.03) * mm, "end": v(6.05, 40.15) * mm});
            skLineSegment(sketch, "E2777", {"start": v(6.05, 40.15) * mm, "end": v(6.1, 40.26) * mm});
            skLineSegment(sketch, "E2778", {"start": v(6.1, 40.26) * mm, "end": v(6.14, 40.38) * mm});
            skLineSegment(sketch, "E2779", {"start": v(6.14, 40.38) * mm, "end": v(6.2, 40.5) * mm});
            skLineSegment(sketch, "E2780", {"start": v(6.2, 40.5) * mm, "end": v(6.24, 40.62) * mm});
            skLineSegment(sketch, "E2781", {"start": v(6.24, 40.62) * mm, "end": v(6.3, 40.73) * mm});
            skLineSegment(sketch, "E2782", {"start": v(6.3, 40.73) * mm, "end": v(6.34, 40.85) * mm});
            skLineSegment(sketch, "E2783", {"start": v(6.34, 40.85) * mm, "end": v(6.39, 40.97) * mm});
            skLineSegment(sketch, "E2784", {"start": v(6.39, 40.97) * mm, "end": v(6.43, 41.09) * mm});
            skLineSegment(sketch, "E2785", {"start": v(6.43, 41.09) * mm, "end": v(6.48, 41.2) * mm});
            skLineSegment(sketch, "E2786", {"start": v(6.48, 41.2) * mm, "end": v(6.53, 41.32) * mm});
            skLineSegment(sketch, "E2787", {"start": v(6.53, 41.32) * mm, "end": v(6.58, 41.44) * mm});
            skLineSegment(sketch, "E2788", {"start": v(6.58, 41.44) * mm, "end": v(6.62, 41.56) * mm});
            skLineSegment(sketch, "E2789", {"start": v(6.62, 41.56) * mm, "end": v(6.67, 41.67) * mm});
            skLineSegment(sketch, "E2790", {"start": v(6.67, 41.67) * mm, "end": v(6.72, 41.8) * mm});
            skLineSegment(sketch, "E2791", {"start": v(6.72, 41.8) * mm, "end": v(6.77, 41.9) * mm});
            skLineSegment(sketch, "E2792", {"start": v(6.77, 41.9) * mm, "end": v(6.82, 42.02) * mm});
            skLineSegment(sketch, "E2793", {"start": v(6.82, 42.02) * mm, "end": v(6.86, 42.14) * mm});
            skLineSegment(sketch, "E2794", {"start": v(6.86, 42.14) * mm, "end": v(6.91, 42.26) * mm});
            skLineSegment(sketch, "E2795", {"start": v(6.91, 42.26) * mm, "end": v(6.96, 42.37) * mm});
            skLineSegment(sketch, "E2796", {"start": v(6.96, 42.37) * mm, "end": v(7.01, 42.49) * mm});
            skLineSegment(sketch, "E2797", {"start": v(7.01, 42.49) * mm, "end": v(7.07, 42.6) * mm});
            skLineSegment(sketch, "E2798", {"start": v(7.07, 42.6) * mm, "end": v(7.12, 42.72) * mm});
            skLineSegment(sketch, "E2799", {"start": v(7.12, 42.72) * mm, "end": v(7.17, 42.83) * mm});
            skLineSegment(sketch, "E2800", {"start": v(7.17, 42.83) * mm, "end": v(7.22, 42.94) * mm});
            skLineSegment(sketch, "E2801", {"start": v(7.22, 42.94) * mm, "end": v(7.28, 43.06) * mm});
            skLineSegment(sketch, "E2802", {"start": v(7.28, 43.06) * mm, "end": v(7.33, 43.17) * mm});
            skLineSegment(sketch, "E2803", {"start": v(7.33, 43.17) * mm, "end": v(7.4, 43.28) * mm});
            skLineSegment(sketch, "E2804", {"start": v(7.4, 43.28) * mm, "end": v(7.45, 43.39) * mm});
            skLineSegment(sketch, "E2805", {"start": v(7.45, 43.39) * mm, "end": v(7.5, 43.5) * mm});
            skLineSegment(sketch, "E2806", {"start": v(7.5, 43.5) * mm, "end": v(7.57, 43.6) * mm});
            skLineSegment(sketch, "E2807", {"start": v(7.57, 43.6) * mm, "end": v(7.63, 43.72) * mm});
            skLineSegment(sketch, "E2808", {"start": v(7.63, 43.72) * mm, "end": v(7.71, 43.86) * mm});
            skLineSegment(sketch, "E2809", {"start": v(7.71, 43.86) * mm, "end": v(7.8, 43.99) * mm});
            skLineSegment(sketch, "E2810", {"start": v(7.8, 43.99) * mm, "end": v(7.88, 44.1) * mm});
            skLineSegment(sketch, "E2811", {"start": v(7.88, 44.1) * mm, "end": v(7.97, 44.22) * mm});
            skLineSegment(sketch, "E2812", {"start": v(7.97, 44.22) * mm, "end": v(8.05, 44.32) * mm});
            skLineSegment(sketch, "E2813", {"start": v(8.05, 44.32) * mm, "end": v(8.14, 44.4) * mm});
            skLineSegment(sketch, "E2814", {"start": v(8.14, 44.4) * mm, "end": v(8.23, 44.5) * mm});
            skLineSegment(sketch, "E2815", {"start": v(8.23, 44.5) * mm, "end": v(8.32, 44.56) * mm});
            skLineSegment(sketch, "E2816", {"start": v(8.32, 44.56) * mm, "end": v(8.4, 44.63) * mm});
            skLineSegment(sketch, "E2817", {"start": v(8.4, 44.63) * mm, "end": v(8.5, 44.68) * mm});
            skLineSegment(sketch, "E2818", {"start": v(8.5, 44.68) * mm, "end": v(8.58, 44.72) * mm});
            skLineSegment(sketch, "E2819", {"start": v(8.58, 44.72) * mm, "end": v(8.67, 44.76) * mm});
            skLineSegment(sketch, "E2820", {"start": v(8.67, 44.76) * mm, "end": v(8.77, 44.8) * mm});
            skLineSegment(sketch, "E2821", {"start": v(8.77, 44.8) * mm, "end": v(8.86, 44.81) * mm});
            skLineSegment(sketch, "E2822", {"start": v(8.86, 44.81) * mm, "end": v(8.95, 44.83) * mm});
            skLineSegment(sketch, "E2823", {"start": v(8.95, 44.83) * mm, "end": v(9.04, 44.83) * mm});
            skLineSegment(sketch, "E2824", {"start": v(9.04, 44.83) * mm, "end": v(9.14, 44.83) * mm});
            skLineSegment(sketch, "E2825", {"start": v(9.14, 44.83) * mm, "end": v(9.23, 44.82) * mm});
            skLineSegment(sketch, "E2826", {"start": v(9.23, 44.82) * mm, "end": v(9.32, 44.8) * mm});
            skLineSegment(sketch, "E2827", {"start": v(9.32, 44.8) * mm, "end": v(9.42, 44.78) * mm});
            skLineSegment(sketch, "E2828", {"start": v(9.42, 44.78) * mm, "end": v(9.51, 44.76) * mm});
            skLineSegment(sketch, "E2829", {"start": v(9.51, 44.76) * mm, "end": v(9.61, 44.72) * mm});
            skLineSegment(sketch, "E2830", {"start": v(9.61, 44.72) * mm, "end": v(9.7, 44.68) * mm});
            skLineSegment(sketch, "E2831", {"start": v(9.7, 44.68) * mm, "end": v(9.8, 44.64) * mm});
            skLineSegment(sketch, "E2832", {"start": v(9.8, 44.64) * mm, "end": v(9.9, 44.58) * mm});
            skLineSegment(sketch, "E2833", {"start": v(9.9, 44.58) * mm, "end": v(10, 44.53) * mm});
            skLineSegment(sketch, "E2834", {"start": v(10, 44.53) * mm, "end": v(10.1, 44.47) * mm});
            skLineSegment(sketch, "E2835", {"start": v(10.1, 44.47) * mm, "end": v(10.2, 44.4) * mm});
            skLineSegment(sketch, "E2836", {"start": v(10.2, 44.4) * mm, "end": v(10.29, 44.33) * mm});
            skLineSegment(sketch, "E2837", {"start": v(10.29, 44.33) * mm, "end": v(10.39, 44.25) * mm});
            skLineSegment(sketch, "E2838", {"start": v(10.39, 44.25) * mm, "end": v(10.49, 44.17) * mm});
            skLineSegment(sketch, "E2839", {"start": v(10.49, 44.17) * mm, "end": v(10.58, 44.09) * mm});
            skLineSegment(sketch, "E2840", {"start": v(10.58, 44.09) * mm, "end": v(10.83, 43.88) * mm});
            skLineSegment(sketch, "E2841", {"start": v(10.83, 43.88) * mm, "end": v(11.07, 43.66) * mm});
            skLineSegment(sketch, "E2842", {"start": v(11.07, 43.66) * mm, "end": v(11.3, 43.44) * mm});
            skLineSegment(sketch, "E2843", {"start": v(11.3, 43.44) * mm, "end": v(11.53, 43.22) * mm});
            skLineSegment(sketch, "E2844", {"start": v(11.53, 43.22) * mm, "end": v(11.76, 43) * mm});
            skLineSegment(sketch, "E2845", {"start": v(11.76, 43) * mm, "end": v(11.98, 42.76) * mm});
            skLineSegment(sketch, "E2846", {"start": v(11.98, 42.76) * mm, "end": v(12.2, 42.53) * mm});
            skLineSegment(sketch, "E2847", {"start": v(12.2, 42.53) * mm, "end": v(12.42, 42.3) * mm});
            skLineSegment(sketch, "E2848", {"start": v(12.42, 42.3) * mm, "end": v(12.63, 42.06) * mm});
            skLineSegment(sketch, "E2849", {"start": v(12.63, 42.06) * mm, "end": v(12.83, 41.82) * mm});
            skLineSegment(sketch, "E2850", {"start": v(12.83, 41.82) * mm, "end": v(13.03, 41.57) * mm});
            skLineSegment(sketch, "E2851", {"start": v(13.03, 41.57) * mm, "end": v(13.23, 41.33) * mm});
            skLineSegment(sketch, "E2852", {"start": v(13.23, 41.33) * mm, "end": v(13.42, 41.08) * mm});
            skLineSegment(sketch, "E2853", {"start": v(13.42, 41.08) * mm, "end": v(13.6, 40.82) * mm});
            skLineSegment(sketch, "E2854", {"start": v(13.6, 40.82) * mm, "end": v(13.8, 40.57) * mm});
            skLineSegment(sketch, "E2855", {"start": v(13.8, 40.57) * mm, "end": v(13.97, 40.3) * mm});
            skLineSegment(sketch, "E2856", {"start": v(13.97, 40.3) * mm, "end": v(14.14, 40.04) * mm});
            skLineSegment(sketch, "E2857", {"start": v(14.14, 40.04) * mm, "end": v(14.3, 39.78) * mm});
            skLineSegment(sketch, "E2858", {"start": v(14.3, 39.78) * mm, "end": v(14.47, 39.5) * mm});
            skLineSegment(sketch, "E2859", {"start": v(14.47, 39.5) * mm, "end": v(14.63, 39.24) * mm});
            skLineSegment(sketch, "E2860", {"start": v(14.63, 39.24) * mm, "end": v(14.78, 38.96) * mm});
            skLineSegment(sketch, "E2861", {"start": v(14.78, 38.96) * mm, "end": v(14.93, 38.68) * mm});
            skLineSegment(sketch, "E2862", {"start": v(14.93, 38.68) * mm, "end": v(15.07, 38.4) * mm});
            skLineSegment(sketch, "E2863", {"start": v(15.07, 38.4) * mm, "end": v(15.21, 38.11) * mm});
            skLineSegment(sketch, "E2864", {"start": v(15.21, 38.11) * mm, "end": v(15.34, 37.82) * mm});
            skLineSegment(sketch, "E2865", {"start": v(15.34, 37.82) * mm, "end": v(15.47, 37.53) * mm});
            skLineSegment(sketch, "E2866", {"start": v(15.47, 37.53) * mm, "end": v(15.59, 37.23) * mm});
            skLineSegment(sketch, "E2867", {"start": v(15.59, 37.23) * mm, "end": v(15.7, 36.93) * mm});
            skLineSegment(sketch, "E2868", {"start": v(15.7, 36.93) * mm, "end": v(15.81, 36.63) * mm});
            skLineSegment(sketch, "E2869", {"start": v(15.81, 36.63) * mm, "end": v(15.92, 36.32) * mm});
            skLineSegment(sketch, "E2870", {"start": v(15.92, 36.32) * mm, "end": v(16.02, 36) * mm});
            skLineSegment(sketch, "E2871", {"start": v(16.02, 36) * mm, "end": v(16.1, 35.7) * mm});
            skLineSegment(sketch, "E2872", {"start": v(16.1, 35.7) * mm, "end": v(16.13, 35.62) * mm});
            skLineSegment(sketch, "E2873", {"start": v(16.13, 35.62) * mm, "end": v(16.15, 35.55) * mm});
            skLineSegment(sketch, "E2874", {"start": v(16.15, 35.55) * mm, "end": v(16.17, 35.47) * mm});
            skLineSegment(sketch, "E2875", {"start": v(16.17, 35.47) * mm, "end": v(16.19, 35.4) * mm});
            skLineSegment(sketch, "E2876", {"start": v(16.19, 35.4) * mm, "end": v(16.2, 35.32) * mm});
            skLineSegment(sketch, "E2877", {"start": v(16.2, 35.32) * mm, "end": v(16.23, 35.25) * mm});
            skLineSegment(sketch, "E2878", {"start": v(16.23, 35.25) * mm, "end": v(16.24, 35.17) * mm});
            skLineSegment(sketch, "E2879", {"start": v(16.24, 35.17) * mm, "end": v(16.26, 35.1) * mm});
            skLineSegment(sketch, "E2880", {"start": v(16.26, 35.1) * mm, "end": v(16.28, 35.02) * mm});
            skLineSegment(sketch, "E2881", {"start": v(16.28, 35.02) * mm, "end": v(16.3, 34.94) * mm});
            skLineSegment(sketch, "E2882", {"start": v(16.3, 34.94) * mm, "end": v(16.32, 34.87) * mm});
            skLineSegment(sketch, "E2883", {"start": v(16.32, 34.87) * mm, "end": v(16.33, 34.8) * mm});
            skLineSegment(sketch, "E2884", {"start": v(16.33, 34.8) * mm, "end": v(16.35, 34.71) * mm});
            skLineSegment(sketch, "E2885", {"start": v(16.35, 34.71) * mm, "end": v(16.37, 34.63) * mm});
            skLineSegment(sketch, "E2886", {"start": v(16.37, 34.63) * mm, "end": v(16.38, 34.56) * mm});
            skLineSegment(sketch, "E2887", {"start": v(16.38, 34.56) * mm, "end": v(16.4, 34.48) * mm});
            skLineSegment(sketch, "E2888", {"start": v(16.4, 34.48) * mm, "end": v(16.42, 34.4) * mm});
            skLineSegment(sketch, "E2889", {"start": v(16.42, 34.4) * mm, "end": v(16.43, 34.32) * mm});
            skLineSegment(sketch, "E2890", {"start": v(16.43, 34.32) * mm, "end": v(16.45, 34.23) * mm});
            skLineSegment(sketch, "E2891", {"start": v(16.45, 34.23) * mm, "end": v(16.47, 34.15) * mm});
            skLineSegment(sketch, "E2892", {"start": v(16.47, 34.15) * mm, "end": v(16.48, 34.07) * mm});
            skLineSegment(sketch, "E2893", {"start": v(16.48, 34.07) * mm, "end": v(16.5, 33.99) * mm});
            skLineSegment(sketch, "E2894", {"start": v(16.5, 33.99) * mm, "end": v(16.52, 33.9) * mm});
            skLineSegment(sketch, "E2895", {"start": v(16.52, 33.9) * mm, "end": v(16.54, 33.82) * mm});
            skLineSegment(sketch, "E2896", {"start": v(16.54, 33.82) * mm, "end": v(16.55, 33.73) * mm});
            skLineSegment(sketch, "E2897", {"start": v(16.55, 33.73) * mm, "end": v(16.57, 33.65) * mm});
            skLineSegment(sketch, "E2898", {"start": v(16.57, 33.65) * mm, "end": v(16.59, 33.56) * mm});
            skLineSegment(sketch, "E2899", {"start": v(16.59, 33.56) * mm, "end": v(16.6, 33.47) * mm});
            skLineSegment(sketch, "E2900", {"start": v(16.6, 33.47) * mm, "end": v(16.63, 33.38) * mm});
            skLineSegment(sketch, "E2901", {"start": v(16.63, 33.38) * mm, "end": v(16.65, 33.3) * mm});
            skLineSegment(sketch, "E2902", {"start": v(16.65, 33.3) * mm, "end": v(16.67, 33.2) * mm});
            skLineSegment(sketch, "E2903", {"start": v(16.67, 33.2) * mm, "end": v(16.69, 33.1) * mm});
            skLineSegment(sketch, "E2904", {"start": v(16.69, 33.1) * mm, "end": v(16.45, 33.5) * mm});
            skLineSegment(sketch, "E2905", {"start": v(16.45, 33.5) * mm, "end": v(16.21, 33.86) * mm});
            skLineSegment(sketch, "E2906", {"start": v(16.21, 33.86) * mm, "end": v(15.96, 34.22) * mm});
            skLineSegment(sketch, "E2907", {"start": v(15.96, 34.22) * mm, "end": v(15.7, 34.56) * mm});
            skLineSegment(sketch, "E2908", {"start": v(15.7, 34.56) * mm, "end": v(15.44, 34.88) * mm});
            skLineSegment(sketch, "E2909", {"start": v(15.44, 34.88) * mm, "end": v(15.16, 35.2) * mm});
            skLineSegment(sketch, "E2910", {"start": v(15.16, 35.2) * mm, "end": v(14.88, 35.5) * mm});
            skLineSegment(sketch, "E2911", {"start": v(14.88, 35.5) * mm, "end": v(14.6, 35.78) * mm});
            skLineSegment(sketch, "E2912", {"start": v(14.6, 35.78) * mm, "end": v(14.3, 36.06) * mm});
            skLineSegment(sketch, "E2913", {"start": v(14.3, 36.06) * mm, "end": v(14, 36.32) * mm});
            skLineSegment(sketch, "E2914", {"start": v(14, 36.32) * mm, "end": v(13.68, 36.57) * mm});
            skLineSegment(sketch, "E2915", {"start": v(13.68, 36.57) * mm, "end": v(13.37, 36.81) * mm});
            skLineSegment(sketch, "E2916", {"start": v(13.37, 36.81) * mm, "end": v(13.04, 37.05) * mm});
            skLineSegment(sketch, "E2917", {"start": v(13.04, 37.05) * mm, "end": v(12.72, 37.27) * mm});
            skLineSegment(sketch, "E2918", {"start": v(12.72, 37.27) * mm, "end": v(12.38, 37.48) * mm});
            skLineSegment(sketch, "E2919", {"start": v(12.38, 37.48) * mm, "end": v(12.04, 37.68) * mm});
            skLineSegment(sketch, "E2920", {"start": v(12.04, 37.68) * mm, "end": v(11.7, 37.87) * mm});
            skLineSegment(sketch, "E2921", {"start": v(11.7, 37.87) * mm, "end": v(11.34, 38.06) * mm});
            skLineSegment(sketch, "E2922", {"start": v(11.34, 38.06) * mm, "end": v(10.99, 38.23) * mm});
            skLineSegment(sketch, "E2923", {"start": v(10.99, 38.23) * mm, "end": v(10.63, 38.4) * mm});
            skLineSegment(sketch, "E2924", {"start": v(10.63, 38.4) * mm, "end": v(10.26, 38.57) * mm});
            skLineSegment(sketch, "E2925", {"start": v(10.26, 38.57) * mm, "end": v(9.9, 38.72) * mm});
            skLineSegment(sketch, "E2926", {"start": v(9.9, 38.72) * mm, "end": v(9.52, 38.87) * mm});
            skLineSegment(sketch, "E2927", {"start": v(9.52, 38.87) * mm, "end": v(9.14, 39.02) * mm});
            skLineSegment(sketch, "E2928", {"start": v(9.14, 39.02) * mm, "end": v(8.76, 39.16) * mm});
            skLineSegment(sketch, "E2929", {"start": v(8.76, 39.16) * mm, "end": v(8.37, 39.3) * mm});
            skLineSegment(sketch, "E2930", {"start": v(8.37, 39.3) * mm, "end": v(7.98, 39.42) * mm});
            skLineSegment(sketch, "E2931", {"start": v(7.98, 39.42) * mm, "end": v(7.6, 39.55) * mm});
            skLineSegment(sketch, "E2932", {"start": v(7.6, 39.55) * mm, "end": v(7.2, 39.67) * mm});
            skLineSegment(sketch, "E2933", {"start": v(7.2, 39.67) * mm, "end": v(6.8, 39.8) * mm});
            skLineSegment(sketch, "E2934", {"start": v(6.8, 39.8) * mm, "end": v(6.4, 39.91) * mm});
            skLineSegment(sketch, "E2935", {"start": v(6.4, 39.91) * mm, "end": v(6, 40.03) * mm});
            skEllipse(sketch, "E2936.0", {"center": v(0, 53.7) * mm, "majorRadius": 35.1 * mm, "minorRadius": 5.5 * mm, "majorAxis": v(1, 0), "construction": true});
            skLineSegment(sketch, "E2937", {"start": v(0, 57.1) * mm, "end": v(45.2, 57.1) * mm, "construction": true});
            skSolve(sketch);
        }
        {
            var Q0;
            Q0 = qSketchRegion(id + "F9", true);
            var Q1;
            Q1=makeQuery(id+"F1.opRevolve","SWEPT_FACE",FACE,{"disambiguationData":[OSD([sQuery(id+"F0.wireOp",EDGE,"E3.0")])]});
            extrude(context, id + "F10", {"entities" : qUnion([Q0]), "operationType" : NewBodyOperationType.ADD, "endBound" : BoundingType.UP_TO_SURFACE, "endBoundEntityFace" : qUnion([Q1]), "depth" : 25 * mm, "hasSecondDirection" : true, "secondDirectionOppositeDirection" : true, "secondDirectionDepth" : 1 * mm});
        }
        {
            var Q0;
            Q0=qCreatedBy(makeId("Right.planeOp"),FACE);
            var sketch = newSketch(context, id + "F11", { "sketchPlane" : qUnion([Q0])});
            skLineSegment(sketch, "E2938.0", {"start": v(-32.5, 54) * mm, "end": v(32.5, 54) * mm, "construction": true});
            skLineSegment(sketch, "E2939.0", {"start": v(-27.58, 7.16) * mm, "end": v(27.58, 7.16) * mm, "construction": true});
            skLineSegment(sketch, "E2940", {"start": v(-32.5, 54) * mm, "end": v(-27.58, 7.16) * mm, "construction": true});
            skLineSegment(sketch, "E2941.0", {"start": v(-33.5, 53.9) * mm, "end": v(-28.57, 7.04) * mm});
            skLineSegment(sketch, "E2942", {"start": v(-33.5, 53.9) * mm, "end": v(-42.45, 52.95) * mm});
            skLineSegment(sketch, "E2943", {"start": v(-42.45, 52.95) * mm, "end": v(-37.62, 7.04) * mm});
            skLineSegment(sketch, "E2944", {"start": v(-37.62, 7.04) * mm, "end": v(-28.57, 7.04) * mm});
            skSolve(sketch);
        }
        {
            var Q0;
            Q0 = qSketchRegion(id + "F11", true);
            var Q1;
            Q1=makeQuery(id+"F1.opRevolve","SWEPT_EDGE",EDGE,{"disambiguationData":[OSD([sQuery(id+"F0.wireOp",EDGE,"E2"),sQuery(id+"F0.wireOp",EDGE,"E4")])]});
            revolve(context, id + "F12", {"operationType" : NewBodyOperationType.REMOVE, "entities" : qUnion([Q0]), "axis" : qUnion([Q1]), "revolveType" : RevolveType.FULL, "oppositeDirection" : true});
        }
    });
